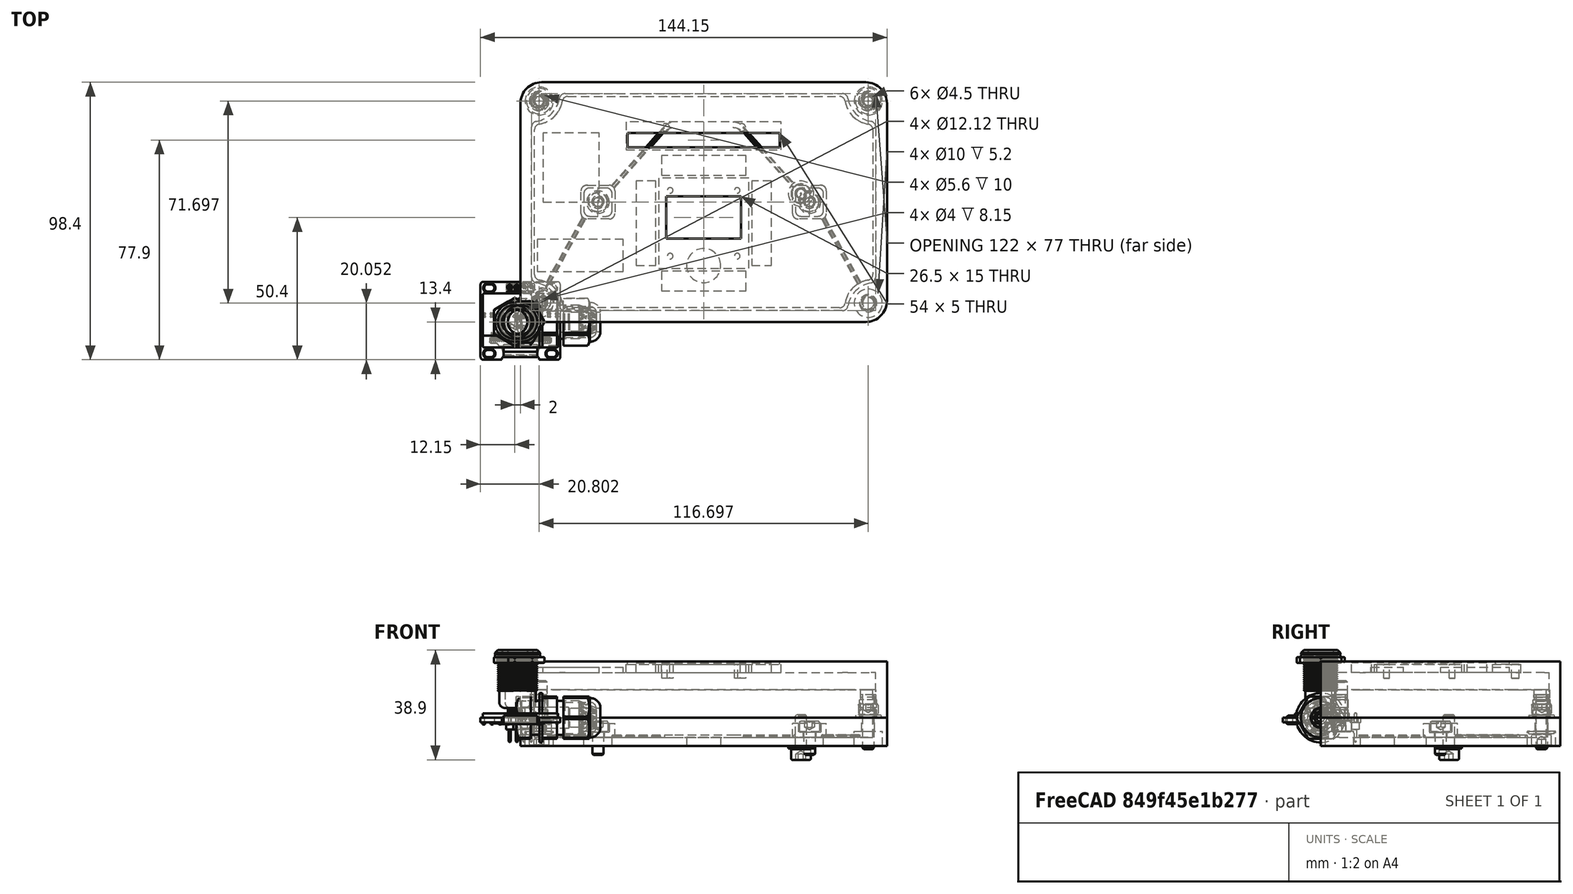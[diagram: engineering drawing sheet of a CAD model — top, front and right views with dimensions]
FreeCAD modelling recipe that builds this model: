
FCSTD DOCUMENT  (FreeCAD 0.20R27319 (Git))
Label: FirstDraft_backup
License: All rights reserved
LicenseURL: http://en.wikipedia.org/wiki/All_rights_reserved
objects: Part::Feature×54, Sketcher::SketchObject×53, PartDesign::Pocket×22, PartDesign::Pad×15, Part::FeaturePython×15, App::Part×11, PartDesign::Line×10, PartDesign::Hole×9, PartDesign::CoordinateSystem×4, App::DocumentObjectGroup×4, PartDesign::AdditiveBox×3, PartDesign::Fillet×3, PartDesign::ShapeBinder×3, App::Link×2, PartDesign::Body×2, PartDesign::AdditivePipe×2, Mesh::Feature×1, App::FeaturePython×1, PartDesign::Plane×1, PartDesign::Mirrored×1
note: 251 computed .brp shape members not serialized (recipe doc carries the construction recipe); baked Part::Feature solids carry a one-line shape summary decoded from their .brp

FEATURE [PartDesign::AdditiveBox] Box002
  AttacherType = Attacher::AttachEngine3D
  Height = 20
  Length = 130
  Width = 85
FEATURE [Sketcher::SketchObject] Sketch001
  ExternalGeometry = -> [Box002]
  FullyConstrained = true
  MapMode = 5
  Placement = pos=(0,0,0) rot=(1,0,0;3.14159rad)
  Support = -> [Box002]
  sketch-geometry (23):
    g0: LineSegment StartX=15.8322 StartY=-4 StartZ=0 EndX=114.168 EndY=-4 EndZ=0
    g1: LineSegment StartX=126 StartY=-15.8322 StartZ=0 EndX=126 EndY=-69.1678 EndZ=0
    g2: LineSegment StartX=114.168 StartY=-81 StartZ=0 EndX=15.8322 EndY=-81 EndZ=0
    g3: LineSegment StartX=4 StartY=-69.1678 StartZ=0 EndX=4 EndY=-15.8322 EndZ=0
    g4: GeomPoint X=4 Y=-4 Z=0
    g5: GeomPoint X=126 Y=-81 Z=0
    g6: GeomPoint X=65 Y=-42.5 Z=0
    g7: ArcOfCircle CenterX=4 CenterY=-81 CenterZ=0 NormalX=0 NormalY=0 NormalZ=1 AngleXU=0 Radius=10 StartAngle=0.167448 EndAngle=1.40335
    g8: ArcOfCircle CenterX=6 CenterY=-69.1678 CenterZ=0 NormalX=0 NormalY=0 NormalZ=1 AngleXU=0 Radius=2 StartAngle=3.14159 EndAngle=4.54494
    g9: ArcOfCircle CenterX=15.8322 CenterY=-79 CenterZ=0 NormalX=0 NormalY=0 NormalZ=1 AngleXU=0 Radius=2 StartAngle=3.30904 EndAngle=4.71239
    g10: ArcOfCircle CenterX=4 CenterY=-4 CenterZ=0 NormalX=0 NormalY=0 NormalZ=1 AngleXU=0 Radius=10 StartAngle=4.87984 EndAngle=6.11574
    g11: ArcOfCircle CenterX=126 CenterY=-4 CenterZ=0 NormalX=0 NormalY=0 NormalZ=1 AngleXU=0 Radius=10 StartAngle=3.30904 EndAngle=4.54494
    g12: ArcOfCircle CenterX=126 CenterY=-81 CenterZ=0 NormalX=0 NormalY=0 NormalZ=1 AngleXU=0 Radius=10 StartAngle=1.73824 EndAngle=2.97414
    g13: LineSegment StartX=4 StartY=-81 StartZ=0 EndX=126 EndY=-81 EndZ=0
    g14: LineSegment StartX=126 StartY=-81 StartZ=0 EndX=126 EndY=-4 EndZ=0
    g15: LineSegment StartX=126 StartY=-4 StartZ=0 EndX=4 EndY=-4 EndZ=0
    g16: LineSegment StartX=4 StartY=-4 StartZ=0 EndX=4 EndY=-81 EndZ=0
    g17: ArcOfCircle CenterX=6 CenterY=-15.8322 CenterZ=0 NormalX=0 NormalY=0 NormalZ=1 AngleXU=0 Radius=2 StartAngle=1.73824 EndAngle=3.14159
    g18: ArcOfCircle CenterX=124 CenterY=-15.8322 CenterZ=0 NormalX=0 NormalY=0 NormalZ=1 AngleXU=0 Radius=2 StartAngle=0 EndAngle=1.40335
    g19: ArcOfCircle CenterX=15.8322 CenterY=-6 CenterZ=0 NormalX=0 NormalY=0 NormalZ=1 AngleXU=0 Radius=2 StartAngle=1.5708 EndAngle=2.97414
    g20: ArcOfCircle CenterX=114.168 CenterY=-6 CenterZ=0 NormalX=0 NormalY=0 NormalZ=1 AngleXU=0 Radius=2 StartAngle=0.167448 EndAngle=1.5708
    g21: ArcOfCircle CenterX=124 CenterY=-69.1678 CenterZ=0 NormalX=0 NormalY=0 NormalZ=1 AngleXU=0 Radius=2 StartAngle=4.87984 EndAngle=6.28319
    g22: ArcOfCircle CenterX=114.168 CenterY=-79 CenterZ=0 NormalX=0 NormalY=0 NormalZ=1 AngleXU=0 Radius=2 StartAngle=4.71239 EndAngle=6.11574
  constraints (56):
    c: Horizontal(g0)
    c: Horizontal(g2)
    c: Vertical(g1)
    c: Vertical(g3)
    c: PointOnObject(g4,g0)
    c: PointOnObject(g4,g3)
    c: PointOnObject(g5,g1)
    c: PointOnObject(g5,g2)
    c: Symmetric(g-6,g-4,g6)
    c: Tangent(g7,g8) = 1.5708
    c: Tangent(g3,g8) = 1.5708
    c: Tangent(g2,g9) = 1.5708
    c: Tangent(g7,g9) = 1.5708
    c: Coincident(g12,g5)
    c: Coincident(g13,g14)
    c: Coincident(g14,g15)
    c: Coincident(g15,g16)
    c: Coincident(g16,g13)
    c: Horizontal(g13)
    c: Horizontal(g15)
    c: Vertical(g14)
    c: Vertical(g16)
    c: Coincident(g13,g7)
    c: Coincident(g14,g11)
    c: Coincident(g4,g10)
    c: Symmetric(g7,g11,g6)
    c: Tangent(g3,g17) = 1.5708
    c: Tangent(g10,g17) = 1.5708
    c: Tangent(g1,g18) = 1.5708
    c: Tangent(g11,g18) = 1.5708
    c: Tangent(g10,g19) = 1.5708
    c: Tangent(g0,g19) = 1.5708
    c: Tangent(g11,g20) = 1.5708
    c: Tangent(g0,g20) = 1.5708
    c: Tangent(g1,g21) = 1.5708
    c: Tangent(g12,g21) = 1.5708
    c: Tangent(g2,g22) = 1.5708
    c: Tangent(g12,g22) = 1.5708
    c: PointOnObject(g0,g15)
    c: PointOnObject(g3,g16)
    c: PointOnObject(g1,g14)
    c: DistanceX(g-6,g7) = 4
    c: DistanceY(g-6,g7) = 4
    c: PointOnObject(g2,g13)
    c: Equal(g7,g10)
    c: Equal(g10,g11)
    c: Equal(g11,g12)
    c: Radius(g7) = 10
    c: Equal(g9,g8)
    c: Equal(g8,g19)
    c: Equal(g19,g17)
    c: Equal(g17,g20)
    c: Equal(g20,g18)
    c: Equal(g18,g21)
    c: Equal(g21,g22)
    c: Radius(g9) = 2
FEATURE [PartDesign::Pocket] Pocket001
  BaseFeature = -> Box002
  Direction = (0,0,1)
  Length = 16
  Length2 = 100
  Profile = -> Sketch001
  ReferenceAxis = -> Sketch001 [N_Axis]
  Type = 0
  expr: Length = <<Box002>>.Height - 4mm
FEATURE [Sketcher::SketchObject] Sketch002
  ExternalGeometry = -> [Pocket001]
  FullyConstrained = true
  MapMode = 5
  Placement = pos=(0,0,16) rot=(1,0,0;3.14159rad)
  Support = -> [Pocket001]
  sketch-geometry (11):
    g0: LineSegment StartX=49 StartY=-19 StartZ=0 EndX=81 EndY=-19 EndZ=0
    g1: LineSegment StartX=81 StartY=-19 StartZ=0 EndX=81 EndY=-51 EndZ=0
    g2: LineSegment StartX=81 StartY=-51 StartZ=0 EndX=49 EndY=-51 EndZ=0
    g3: LineSegment StartX=49 StartY=-51 StartZ=0 EndX=49 EndY=-19 EndZ=0
    g4: GeomPoint X=65 Y=-4 Z=0
    g5: LineSegment StartX=65 StartY=-4 StartZ=0 EndX=65 EndY=-19 EndZ=0
    g6: LineSegment StartX=37.5 StartY=-61 StartZ=0 EndX=92.5 EndY=-61 EndZ=0
    g7: LineSegment StartX=92.5 StartY=-61 StartZ=0 EndX=92.5 EndY=-71 EndZ=0
    g8: LineSegment StartX=92.5 StartY=-71 StartZ=0 EndX=37.5 EndY=-71 EndZ=0
    g9: LineSegment StartX=37.5 StartY=-71 StartZ=0 EndX=37.5 EndY=-61 EndZ=0
    g10: LineSegment StartX=65 StartY=-19 StartZ=0 EndX=65 EndY=-61 EndZ=0
  constraints (29):
    c: Coincident(g0,g1)
    c: Coincident(g1,g2)
    c: Coincident(g2,g3)
    c: Coincident(g3,g0)
    c: Horizontal(g0)
    c: Horizontal(g2)
    c: Vertical(g1)
    c: Vertical(g3)
    c: Coincident(g5,g4)
    c: Vertical(g5)
    c: Symmetric(g0,g0,g5)
    c: DistanceY(g5,g5) = 15
    c: DistanceY(g1,g1) = 32
    c: Equal(g1,g0)
    c: Coincident(g6,g7)
    c: Coincident(g7,g8)
    c: Coincident(g8,g9)
    c: Coincident(g9,g6)
    c: Horizontal(g6)
    c: Horizontal(g8)
    c: Vertical(g7)
    c: Vertical(g9)
    c: DistanceX(g6,g6) = 55
    c: DistanceY(g7,g7) = 10
    c: Coincident(g10,g5)
    c: Vertical(g10)
    c: Symmetric(g6,g6,g10)
    c: DistanceY(g6,g1) = 10
    c: Symmetric(g-3,g-3,g4)
FEATURE [PartDesign::Pocket] Pocket002  label="Platz OLED und LED-Strip"
  BaseFeature = -> Pocket001
  Direction = (0,0,1)
  Length = 3
  Length2 = 100
  Profile = -> Sketch002
  Type = 0
FEATURE [Sketcher::SketchObject] Sketch003
  ExternalGeometry = -> [Sketch002,Pocket002]
  FullyConstrained = true
  MapMode = 5
  Placement = pos=(0,0,16) rot=(1,0,0;3.14159rad)
  Support = -> [Pocket002]
  sketch-geometry (10):
    g0: LineSegment StartX=51.75 StartY=-29.5 StartZ=0 EndX=78.25 EndY=-29.5 EndZ=0
    g1: LineSegment StartX=78.25 StartY=-29.5 StartZ=0 EndX=78.25 EndY=-44.5 EndZ=0
    g2: LineSegment StartX=78.25 StartY=-44.5 StartZ=0 EndX=51.75 EndY=-44.5 EndZ=0
    g3: LineSegment StartX=51.75 StartY=-44.5 StartZ=0 EndX=51.75 EndY=-29.5 EndZ=0
    g4: LineSegment StartX=38 StartY=-62 StartZ=0 EndX=92 EndY=-62 EndZ=0
    g5: LineSegment StartX=92 StartY=-62 StartZ=0 EndX=92 EndY=-67 EndZ=0
    g6: LineSegment StartX=92 StartY=-67 StartZ=0 EndX=38 EndY=-67 EndZ=0
    g7: LineSegment StartX=38 StartY=-67 StartZ=0 EndX=38 EndY=-62 EndZ=0
    g8: LineSegment StartX=65 StartY=-62 StartZ=0 EndX=65 EndY=-61 EndZ=0
    g9: LineSegment StartX=65 StartY=-29.5 StartZ=0 EndX=65 EndY=-19 EndZ=0
  constraints (28):
    c: Coincident(g0,g1)
    c: Coincident(g1,g2)
    c: Coincident(g2,g3)
    c: Coincident(g3,g0)
    c: Horizontal(g0)
    c: Horizontal(g2)
    c: Vertical(g1)
    c: Vertical(g3)
    c: DistanceX(g0,g0) = 26.5
    c: DistanceY(g1,g1) = 15
    c: Coincident(g4,g5)
    c: Coincident(g5,g6)
    c: Coincident(g6,g7)
    c: Coincident(g7,g4)
    c: Horizontal(g4)
    c: Horizontal(g6)
    c: Vertical(g5)
    c: Vertical(g7)
    c: DistanceX(g4,g-3) = 0.5
    c: Vertical(g8)
    c: Symmetric(g4,g4,g8)
    c: Symmetric(g-3,g-4,g8)
    c: DistanceY(g5,g5) = 5
    c: DistanceY(g4,g-3) = 1
    c: Vertical(g9)
    c: Symmetric(g0,g0,g9)
    c: DistanceY(g9,g9) = 10.5
    c: Symmetric(g-5,g-5,g9)
FEATURE [PartDesign::Pocket] Pocket003  label="Sichtausschnitt"
  BaseFeature = -> Pocket002
  Direction = (0,0,1)
  Length = 1.01
  Length2 = 100
  Profile = -> Sketch003
  ReferenceAxis = -> Sketch003 [N_Axis]
  Type = 1
FEATURE [Sketcher::SketchObject] Sketch004  label="Sketch Halter OLED"
  ExternalGeometry = -> [Sketch002]
  FullyConstrained = true
  MapMode = 5
  Placement = pos=(0,0,19) rot=(1,0,0;3.14159rad)
  Support = -> [Pocket003]
  sketch-geometry (9):
    g0: Circle CenterX=53.1 CenterY=-23.35 CenterZ=0 NormalX=0 NormalY=0 NormalZ=1 AngleXU=0 Radius=1
    g1: Circle CenterX=76.9 CenterY=-23.35 CenterZ=0 NormalX=0 NormalY=0 NormalZ=1 AngleXU=0 Radius=1
    g2: Circle CenterX=76.9 CenterY=-46.65 CenterZ=0 NormalX=0 NormalY=0 NormalZ=1 AngleXU=0 Radius=1
    g3: Circle CenterX=53.1 CenterY=-46.65 CenterZ=0 NormalX=0 NormalY=0 NormalZ=1 AngleXU=0 Radius=1
    g4: LineSegment StartX=53.1 StartY=-23.35 StartZ=0 EndX=76.9 EndY=-23.35 EndZ=0
    g5: LineSegment StartX=76.9 StartY=-23.35 StartZ=0 EndX=76.9 EndY=-46.65 EndZ=0
    g6: LineSegment StartX=76.9 StartY=-46.65 StartZ=0 EndX=53.1 EndY=-46.65 EndZ=0
    g7: LineSegment StartX=53.1 StartY=-46.65 StartZ=0 EndX=53.1 EndY=-23.35 EndZ=0
    g8: GeomPoint X=65 Y=-35 Z=0
  constraints (20):
    c: Coincident(g4,g5)
    c: Coincident(g5,g6)
    c: Coincident(g6,g7)
    c: Coincident(g7,g4)
    c: Horizontal(g4)
    c: Horizontal(g6)
    c: Vertical(g5)
    c: Vertical(g7)
    c: Coincident(g4,g0)
    c: Coincident(g5,g2)
    c: Coincident(g1,g4)
    c: Coincident(g3,g6)
    c: Equal(g0,g1)
    c: Equal(g1,g2)
    c: Equal(g2,g3)
    c: Diameter(g1) = 2
    c: DistanceX(g4,g4) = 23.8
    c: DistanceY(g5,g5) = 23.3
    c: Symmetric(g-4,g-6,g8)
    c: Symmetric(g3,g1,g8)
FEATURE [PartDesign::Pad] Pad  label="Halter OLED"
  BaseFeature = -> Pocket003
  Direction = (0,0,-1)
  Length = 5
  Length2 = 100
  Profile = -> Sketch004
  ReferenceAxis = -> Sketch004 [N_Axis]
  Type = 0
FEATURE [Sketcher::SketchObject] Sketch005
  ExternalGeometry = -> [Sketch002]
  FullyConstrained = true
  MapMode = 5
  Placement = pos=(0,0,16) rot=(1,0,0;3.14159rad)
  Support = -> [Pad]
  sketch-geometry (26):
    g0: LineSegment StartX=50 StartY=-11 StartZ=0 EndX=80 EndY=-11 EndZ=0
    g1: LineSegment StartX=80 StartY=-11 StartZ=0 EndX=80 EndY=-18 EndZ=0
    g2: LineSegment StartX=80 StartY=-18 StartZ=0 EndX=50 EndY=-18 EndZ=0
    g3: LineSegment StartX=50 StartY=-18 StartZ=0 EndX=50 EndY=-11 EndZ=0
    g4: LineSegment StartX=82 StartY=-20 StartZ=0 EndX=89 EndY=-20 EndZ=0
    g5: LineSegment StartX=89 StartY=-20 StartZ=0 EndX=89 EndY=-50 EndZ=0
    g6: LineSegment StartX=89 StartY=-50 StartZ=0 EndX=82 EndY=-50 EndZ=0
    g7: LineSegment StartX=82 StartY=-50 StartZ=0 EndX=82 EndY=-20 EndZ=0
    g8: LineSegment StartX=41 StartY=-20 StartZ=0 EndX=48 EndY=-20 EndZ=0
    g9: LineSegment StartX=48 StartY=-20 StartZ=0 EndX=48 EndY=-50 EndZ=0
    g10: LineSegment StartX=48 StartY=-50 StartZ=0 EndX=41 EndY=-50 EndZ=0
    g11: LineSegment StartX=41 StartY=-50 StartZ=0 EndX=41 EndY=-20 EndZ=0
    g12: LineSegment StartX=50 StartY=-52 StartZ=0 EndX=80 EndY=-52 EndZ=0
    g13: LineSegment StartX=80 StartY=-52 StartZ=0 EndX=80 EndY=-59 EndZ=0
    g14: LineSegment StartX=80 StartY=-59 StartZ=0 EndX=50 EndY=-59 EndZ=0
    g15: LineSegment StartX=50 StartY=-59 StartZ=0 EndX=50 EndY=-52 EndZ=0
    g16: LineSegment StartX=48 StartY=-18 StartZ=0 EndX=82 EndY=-18 EndZ=0
    g17: LineSegment StartX=82 StartY=-18 StartZ=0 EndX=82 EndY=-52 EndZ=0
    g18: LineSegment StartX=82 StartY=-52 StartZ=0 EndX=48 EndY=-52 EndZ=0
    g19: LineSegment StartX=48 StartY=-52 StartZ=0 EndX=48 EndY=-18 EndZ=0
    g20: GeomPoint X=65 Y=-35 Z=0
    g21: GeomPoint X=48 Y=-35 Z=0
    g22: GeomPoint X=116 Y=-18 Z=0
    g23: GeomPoint X=82 Y=-35 Z=0
    g24: GeomPoint X=65 Y=-52 Z=0
    g25: GeomPoint X=65 Y=-18 Z=0
  constraints (61):
    c: Coincident(g0,g1)
    c: Coincident(g1,g2)
    c: Coincident(g2,g3)
    c: Coincident(g3,g0)
    c: Horizontal(g0)
    c: Horizontal(g2)
    c: Vertical(g1)
    c: Vertical(g3)
    c: Coincident(g4,g5)
    c: Coincident(g5,g6)
    c: Coincident(g6,g7)
    c: Coincident(g7,g4)
    c: Horizontal(g4)
    c: Horizontal(g6)
    c: Vertical(g5)
    c: Vertical(g7)
    c: Coincident(g8,g9)
    c: Coincident(g9,g10)
    c: Coincident(g10,g11)
    c: Coincident(g11,g8)
    c: Horizontal(g8)
    c: Horizontal(g10)
    c: Vertical(g9)
    c: Vertical(g11)
    c: Coincident(g12,g13)
    c: Coincident(g13,g14)
    c: Coincident(g14,g15)
    c: Coincident(g15,g12)
    c: Horizontal(g12)
    c: Horizontal(g14)
    c: Vertical(g13)
    c: Vertical(g15)
    c: Equal(g4,g1)
    c: Equal(g1,g8)
    c: Equal(g8,g13)
    c: Coincident(g16,g17)
    c: Coincident(g17,g18)
    c: Coincident(g18,g19)
    c: Coincident(g19,g16)
    c: DistanceX(g-4,g16) = 1
    c: DistanceY(g-4,g16) = 1
    c: Symmetric(g16,g18,g20)
    c: Symmetric(g-6,g-4,g20)
    c: DistanceY(g15,g15) = 7
    c: Vertical(g19)
    c: Horizontal(g16)
    c: PointOnObject(g12,g18)
    c: Vertical(g17)
    c: Equal(g0,g11)
    c: Equal(g11,g5)
    c: Equal(g5,g14)
    c: DistanceY(g11,g11) = 30
    c: Symmetric(g18,g17,g24)
    c: Symmetric(g6,g4,g23)
    c: Symmetric(g16,g22,g16)
    c: Symmetric(g16,g18,g21)
    c: Symmetric(g8,g9,g21)
    c: Symmetric(g17,g16,g23)
    c: Symmetric(g12,g12,g24)
    c: Symmetric(g2,g1,g25)
    c: Symmetric(g16,g16,g25)
FEATURE [PartDesign::Pocket] Pocket004  label="Ausschnitte  Touch"
  BaseFeature = -> Pad
  Direction = (0,0,1)
  Length = 3.5
  Length2 = 100
  Profile = -> Sketch005
  Type = 0
FEATURE [Part::Feature] Part__Feature  label="Pantalla"
  Placement = pos=(4e-15,0.525,-1e-15) rot=(0,0,1;0rad)
  shape: bbox 26.68 x 19.2 x 1.6 mm, 12 faces (baked)
FEATURE [Part::Feature] Part__Feature001  label="PADS"
  shape: bbox 0.4 x 3 x 0.1 mm, 6 faces (baked)
FEATURE [Part::Feature] Part__Feature002  label="PADS001"
  shape: bbox 0.4 x 3 x 0.1 mm, 6 faces (baked)
FEATURE [Part::Feature] Part__Feature003  label="PADS002"
  shape: bbox 0.4 x 3 x 0.1 mm, 6 faces (baked)
FEATURE [Part::Feature] Part__Feature004  label="PADS003"
  shape: bbox 0.4 x 3 x 0.1 mm, 6 faces (baked)
FEATURE [Part::Feature] Part__Feature005  label="PADS004"
  shape: bbox 0.4 x 3 x 0.1 mm, 6 faces (baked)
FEATURE [Part::Feature] Part__Feature006  label="PADS005"
  shape: bbox 0.4 x 3 x 0.1 mm, 6 faces (baked)
FEATURE [Part::Feature] Part__Feature007  label="PADS006"
  shape: bbox 0.4 x 3 x 0.1 mm, 6 faces (baked)
FEATURE [Part::Feature] Part__Feature008  label="PADS007"
  shape: bbox 0.4 x 3 x 0.1 mm, 6 faces (baked)
FEATURE [Part::Feature] Part__Feature009  label="PADS008"
  shape: bbox 0.4 x 3 x 0.1 mm, 6 faces (baked)
FEATURE [Part::Feature] Part__Feature010  label="PADS009"
  shape: bbox 0.4 x 3 x 0.1 mm, 6 faces (baked)
FEATURE [Part::Feature] Part__Feature011  label="PADS010"
  shape: bbox 0.4 x 3 x 0.1 mm, 6 faces (baked)
FEATURE [Part::Feature] Part__Feature012  label="PADS011"
  shape: bbox 0.4 x 3 x 0.1 mm, 6 faces (baked)
FEATURE [Part::Feature] Part__Feature013  label="PADS012"
  shape: bbox 0.4 x 3 x 0.1 mm, 6 faces (baked)
FEATURE [Part::Feature] Part__Feature014  label="PADS013"
  shape: bbox 0.4 x 3 x 0.1 mm, 6 faces (baked)
FEATURE [Part::Feature] Part__Feature015  label="PADS014"
  shape: bbox 0.4 x 3 x 0.1 mm, 6 faces (baked)
FEATURE [Part::Feature] Part__Feature016  label="PADS015"
  shape: bbox 0.4 x 3 x 0.1 mm, 6 faces (baked)
FEATURE [Part::Feature] Part__Feature017  label="PADS016"
  shape: bbox 0.4 x 3 x 0.1 mm, 6 faces (baked)
FEATURE [Part::Feature] Part__Feature018  label="PADS017"
  shape: bbox 0.4 x 3 x 0.1 mm, 6 faces (baked)
FEATURE [Part::Feature] Part__Feature019  label="PADS018"
  shape: bbox 0.4 x 3 x 0.1 mm, 6 faces (baked)
FEATURE [Part::Feature] Part__Feature020  label="PADS019"
  shape: bbox 0.4 x 3 x 0.1 mm, 6 faces (baked)
FEATURE [Part::Feature] Part__Feature021  label="PADS020"
  shape: bbox 0.4 x 3 x 0.1 mm, 6 faces (baked)
FEATURE [Part::Feature] Part__Feature022  label="PADS021"
  shape: bbox 0.4 x 3 x 0.1 mm, 6 faces (baked)
FEATURE [Part::Feature] Part__Feature023  label="PADS022"
  shape: bbox 0.4 x 3 x 0.1 mm, 6 faces (baked)
FEATURE [Part::Feature] Part__Feature024  label="PADS023"
  shape: bbox 0.4 x 3 x 0.1 mm, 6 faces (baked)
FEATURE [Part::Feature] Part__Feature025  label="PADS024"
  shape: bbox 0.4 x 3 x 0.1 mm, 6 faces (baked)
FEATURE [Part::Feature] Part__Feature026  label="PADS025"
  shape: bbox 0.4 x 3 x 0.1 mm, 6 faces (baked)
FEATURE [Part::Feature] Part__Feature027  label="PADS026"
  shape: bbox 0.4 x 3 x 0.1 mm, 6 faces (baked)
FEATURE [Part::Feature] Part__Feature028  label="PADS027"
  shape: bbox 0.4 x 3 x 0.1 mm, 6 faces (baked)
FEATURE [Part::Feature] Part__Feature029  label="PADS028"
  shape: bbox 0.4 x 3 x 0.1 mm, 6 faces (baked)
FEATURE [Part::Feature] Part__Feature030  label="PADS029"
  shape: bbox 0.4 x 3 x 0.1 mm, 6 faces (baked)
FEATURE [App::Part] PADS  label="PADS030"
  Group = -> [Part__Feature001,Part__Feature002,Part__Feature003,Part__Feature004,Part__Feature005,Part__Feature006,Part__Feature007,Part__Feature008,Part__Feature009,Part__Feature010,Part__Feature011,Part__Feature012,Part__Feature013,Part__Feature014,Part__Feature015,Part__Feature016,Part__Feature017,Part__Feature018,Part__Feature019,Part__Feature020,Part__Feature021,Part__Feature022,Part__Feature023,+7 more]
  Origin = -> Origin005
FEATURE [Part::Feature] Part__Feature031  label="Base PCB"
  shape: bbox 28.3 x 27.65 x 1.7 mm, 324 faces (baked)
FEATURE [App::Part] Base_PCB  label="Base PCB001"
  Group = -> [PADS,Part__Feature031]
  Origin = -> Origin006
FEATURE [Part::Feature] Part__Feature032  label="PINOS"
  shape: bbox 2.54 x 2.54 x 10.4 mm, 28 faces (baked)
FEATURE [Part::Feature] Part__Feature033  label="PINOS001"
  shape: bbox 2.54 x 2.54 x 10.4 mm, 28 faces (baked)
FEATURE [Part::Feature] Part__Feature034  label="PINOS002"
  shape: bbox 2.54 x 2.54 x 10.4 mm, 28 faces (baked)
FEATURE [Part::Feature] Part__Feature035  label="PINOS003"
  shape: bbox 2.54 x 2.54 x 10.4 mm, 28 faces (baked)
FEATURE [App::Part] PINOS  label="PINOS004"
  Group = -> [Part__Feature032,Part__Feature033,Part__Feature034,Part__Feature035]
  Origin = -> Origin007
FEATURE [Part::Feature] Part__Feature036  label="fLEX"
  Placement = pos=(4e-15,1.525,-0.1) rot=(0,0,1;0rad)
  shape: bbox 39.56 x 36.02 x 13.34 mm, 31 faces (baked)
FEATURE [Part::Feature] Part__Feature037  label="res"
  Placement = pos=(13,2.425,-4) rot=(1,0,0;3.14159rad)
  shape: bbox 1.02 x 1.65 x 0.81 mm, 37 faces (baked)
FEATURE [Part::Feature] Part__Feature038  label="res001"
  Placement = pos=(10.1111,2.425,-4) rot=(1,0,0;3.14159rad)
  shape: bbox 1.02 x 1.65 x 0.81 mm, 37 faces (baked)
FEATURE [Part::Feature] Part__Feature039  label="res002"
  Placement = pos=(7.22222,2.425,-4) rot=(1,0,0;3.14159rad)
  shape: bbox 1.02 x 1.65 x 0.81 mm, 37 faces (baked)
FEATURE [Part::Feature] Part__Feature040  label="res003"
  Placement = pos=(4.33333,2.425,-4) rot=(1,0,0;3.14159rad)
  shape: bbox 1.02 x 1.65 x 0.81 mm, 37 faces (baked)
FEATURE [Part::Feature] Part__Feature041  label="res004"
  Placement = pos=(1.44444,2.425,-4) rot=(1,0,0;3.14159rad)
  shape: bbox 1.02 x 1.65 x 0.81 mm, 37 faces (baked)
FEATURE [Part::Feature] Part__Feature042  label="res005"
  Placement = pos=(-1.44444,2.425,-4) rot=(1,0,0;3.14159rad)
  shape: bbox 1.02 x 1.65 x 0.81 mm, 37 faces (baked)
FEATURE [Part::Feature] Part__Feature043  label="res006"
  Placement = pos=(-4.33333,2.425,-4) rot=(1,0,0;3.14159rad)
  shape: bbox 1.02 x 1.65 x 0.81 mm, 37 faces (baked)
FEATURE [Part::Feature] Part__Feature044  label="res007"
  Placement = pos=(-7.22222,2.425,-4) rot=(1,0,0;3.14159rad)
  shape: bbox 1.02 x 1.65 x 0.81 mm, 37 faces (baked)
FEATURE [Part::Feature] Part__Feature045  label="res008"
  Placement = pos=(-10.1111,2.425,-4) rot=(1,0,0;3.14159rad)
  shape: bbox 1.02 x 1.65 x 0.81 mm, 37 faces (baked)
FEATURE [Part::Feature] Part__Feature046  label="res009"
  Placement = pos=(-13,2.425,-4) rot=(1,0,0;3.14159rad)
  shape: bbox 1.02 x 1.65 x 0.81 mm, 37 faces (baked)
FEATURE [Part::Feature] Part__Feature047  label="res010"
  Placement = pos=(0,-1.575,-4) rot=(0.707107,-0.707107,0;3.14159rad)
  shape: bbox 1.65 x 1.02 x 0.81 mm, 37 faces (baked)
FEATURE [App::Part] Resistores_SMD  label="Resistores SMD"
  Group = -> [Part__Feature037,Part__Feature038,Part__Feature039,Part__Feature040,Part__Feature041,Part__Feature042,Part__Feature043,Part__Feature044,Part__Feature045,Part__Feature046,Part__Feature047]
  Origin = -> Origin008
FEATURE [App::Part] Tela_OLed_128x64_v15  label="Tela OLed 128x64 v15"
  Group = -> [Part__Feature,Base_PCB,PINOS,Part__Feature036,Resistores_SMD]
  Origin = -> Origin009
  Placement = pos=(60,29.5,22.5) rot=(0,0,1;0rad)
FEATURE [Sketcher::SketchObject] Sketch007
  ExternalGeometry = -> [Pocket004,Sketch003]
  FullyConstrained = true
  MapMode = 5
  Placement = pos=(0,0,19) rot=(1,0,0;3.14159rad)
  Support = -> [Pocket004]
  sketch-geometry (5):
    g0: Circle CenterX=51.5 CenterY=-69 CenterZ=0 NormalX=0 NormalY=0 NormalZ=1 AngleXU=0 Radius=1.35
    g1: Circle CenterX=78.5 CenterY=-69 CenterZ=0 NormalX=0 NormalY=0 NormalZ=1 AngleXU=0 Radius=1.35
    g2: LineSegment StartX=51.5 StartY=-69 StartZ=0 EndX=78.5 EndY=-69 EndZ=0
    g3: LineSegment StartX=65 StartY=-71 StartZ=0 EndX=65 EndY=-67 EndZ=0
    g4: GeomPoint X=65 Y=-69 Z=0
  constraints (11):
    c: Coincident(g2,g0)
    c: Coincident(g2,g1)
    c: Horizontal(g2)
    c: Equal(g1,g0)
    c: Diameter(g0) = 2.7
    c: DistanceX(g2,g2) = 27
    c: Vertical(g3)
    c: Symmetric(g0,g1,g4)
    c: Symmetric(g3,g3,g4)
    c: Symmetric(g-5,g-5,g3)
    c: PointOnObject(g3,g-6)
FEATURE [PartDesign::Pad] Pad001  label="Halter LED Strip"
  BaseFeature = -> Pocket004
  Direction = (0,0,-1)
  Length = 5
  Length2 = 10
  Profile = -> Sketch007
  ReferenceAxis = -> Sketch007 [N_Axis]
  Type = 0
FEATURE [Mesh::Feature] DuinoPeak_WS2812_RGB_Pixel
FEATURE [Part::Feature] Part__Feature086  label="12mm Switch"
  shape: bbox 17.01 x 15.16 x 24 mm, 165 faces, 3 solids (baked)
FEATURE [App::Part] _2mm_Switch_v5  label="12mm Switch v5"
  Group = -> [Part__Feature086]
  Origin = -> Origin012
  Placement = pos=(15,0,0) rot=(1,0,0;0rad)
FEATURE [Part::FeaturePython] Clone  label="12mm Switch v006"  # Draft clone (typed FeaturePython)
  AttacherType = Attacher::AttachEngine3D
  Fuse = false
  Objects = -> [_2mm_Switch_v5]
  Placement = pos=(-2,-1e-15,0) rot=(0,0,-1;0.523599rad)
  Scale = (1,1,1)
FEATURE [PartDesign::CoordinateSystem] LCS_Origin
  AttacherType = Attacher::AttachEngine3D
  MapMode = 2
  Support = -> [X_Axis013]
FEATURE [App::FeaturePython] Variables  # WARN: FeaturePython — macro-defined, semantics opaque (R4)
  Type = App::PropertyContainer
FEATURE [App::DocumentObjectGroup] Constraints
FEATURE [App::DocumentObjectGroup] Configurations
FEATURE [App::Part] Part  label="Double-Switch"
  Group = -> [Clone,_2mm_Switch_v5]
  Origin = -> Origin014
FEATURE [App::Part] Part001  label="LED-Strip"
  Group = -> [DuinoPeak_WS2812_RGB_Pixel]
  Origin = -> Origin015
  Placement = pos=(34,56,20.6) rot=(0,0,1;0rad)
FEATURE [App::Link] Base  label="Base001"
  AssemblyType = Part::Link
  AttachedBy = #LCS_1
  AttachedTo = Parent Assembly#LCS_Origin
  LinkedObject = -> Body
  SolverId = Asm4EE
  expr: Placement = LCS_Origin.Placement * AttachmentOffset * LCS_1.Placement ^ -1
FEATURE [Part::FeaturePython] HeatSet  label="Auto-HeatSet"  # WARN: FeaturePython — macro-defined, semantics opaque (R4)
  Placement = pos=(123.349,78.3485,0) rot=(-1,0,0;3.14159rad)
  baseObject = -> Body002 [Edge48]
  diameter = 0
  invert = false
  offset = 0
FEATURE [Part::FeaturePython] HeatSet001  label="Auto-HeatSet001"  # WARN: FeaturePython — macro-defined, semantics opaque (R4)
  Placement = pos=(6.65146,78.3485,0) rot=(-1,0,0;3.14159rad)
  baseObject = -> Body002 [Edge31]
  diameter = 0
  invert = false
  offset = 0
FEATURE [Part::FeaturePython] HeatSet002  label="Auto-HeatSet002"  # WARN: FeaturePython — macro-defined, semantics opaque (R4)
  Placement = pos=(6.65146,6.65148,0) rot=(-1,0,0;3.14159rad)
  baseObject = -> Body002 [Edge29]
  diameter = 0
  invert = false
  offset = 0
FEATURE [Part::FeaturePython] HeatSet003  label="Auto-HeatSet003"  # WARN: FeaturePython — macro-defined, semantics opaque (R4)
  Placement = pos=(123.349,6.65148,0) rot=(-1,0,0;3.14159rad)
  baseObject = -> Body002 [Edge30]
  diameter = 0
  invert = false
  offset = 0
FEATURE [App::Link] Front_inkl__Fasteners  label="Front inkl. Fasteners001"
  AssemblyType = Part::Link
  AttachedBy = #LCS_3
  AttachedTo = Base#LCS_1
  LinkedObject = -> Part002
  SolverId = Asm4EE
  expr: Placement = Base.Placement * LCS_1.Placement * AttachmentOffset * LCS_3.Placement ^ -1
FEATURE [Part::FeaturePython] Washer  label="M4-Washer"  # Fasteners workbench fastener (typed FeaturePython)
  Placement = pos=(99.5,45.5,-10) rot=(-1,0,0;3.14159rad)
  baseObject = -> Body [Edge50]
  diameter = 5
  invert = false
  matchOuter = true
  offset = 0
  type = 3
FEATURE [Part::FeaturePython] Washer001  label="M4-Washer424"  # Fasteners workbench fastener (typed FeaturePython)
  Placement = pos=(123.349,78.3485,0) rot=(0,0,1;0rad)
  baseObject = -> Body [Edge52]
  diameter = 5
  invert = false
  matchOuter = true
  offset = 0
  type = 3
FEATURE [Part::FeaturePython] Washer002  label="M4-Washer425"  # Fasteners workbench fastener (typed FeaturePython)
  Placement = pos=(6.65146,78.3485,-4.8) rot=(-1,0,0;3.14159rad)
  baseObject = -> Body [Edge88]
  diameter = 5
  invert = false
  matchOuter = true
  offset = 0
  type = 3
FEATURE [Part::FeaturePython] Washer003  label="M4-Washer426"  # Fasteners workbench fastener (typed FeaturePython)
  Placement = pos=(7.5,7.5,0) rot=(-1,0,0;3.14159rad)
  baseObject = -> Body [Edge54]
  diameter = 5
  invert = false
  matchOuter = true
  offset = 0
  type = 3
FEATURE [Part::FeaturePython] Screw  label="M4x14-Screw"  # Fasteners workbench fastener (typed FeaturePython)
  Placement = pos=(7.5,7.5,-0.9) rot=(-1,0,0;3.14159rad)
  baseObject = -> Washer003 [Edge1]
  diameter = 5
  invert = false
  length = 4
  lengthCustom = 14
  matchOuter = false
  offset = 0
  thread = false
  type = 34
FEATURE [Part::FeaturePython] Screw001  label="M4x12-Screw"  # Fasteners workbench fastener (typed FeaturePython)
  Placement = pos=(99.5,45.5,-10.9) rot=(-1,0,0;3.14159rad)
  baseObject = -> Washer [Edge1]
  diameter = 5
  invert = false
  length = 3
  lengthCustom = 12
  matchOuter = false
  offset = 0
  thread = false
  type = 34
FEATURE [Part::FeaturePython] Screw002  label="M4x12-Screw281"  # Fasteners workbench fastener (typed FeaturePython)
  Placement = pos=(123.349,78.3485,0.9) rot=(0,0,1;0rad)
  baseObject = -> Washer001 [Edge1]
  diameter = 5
  invert = false
  length = 3
  lengthCustom = 12
  matchOuter = false
  offset = 0
  thread = false
  type = 34
FEATURE [Part::FeaturePython] Screw003  label="M4x12-Screw282"  # Fasteners workbench fastener (typed FeaturePython)
  Placement = pos=(6.65146,78.3485,-5.7) rot=(-1,0,0;3.14159rad)
  baseObject = -> Washer002 [Edge1]
  diameter = 5
  invert = false
  length = 3
  lengthCustom = 12
  matchOuter = false
  offset = 0
  thread = false
  type = 34
FEATURE [App::DocumentObjectGroup] Fasteners
  Group = -> [Washer,Washer001,Washer002,Washer003,Screw,Screw001,Screw002,Screw003]
FEATURE [App::Part] Assembly
  AssemblyType = Part::Link
  Group = -> [LCS_Origin,Variables,Constraints,Configurations,Base,Front_inkl__Fasteners,Fasteners,Washer,Washer001,Washer002,Washer003,Screw,Screw001,Screw002,Screw003]
  Origin = -> Origin013
  Type = Assembly
FEATURE [PartDesign::Fillet] Fillet
  Base = -> Pad001 [Edge3,Edge19,Edge1,Edge6]
  BaseFeature = -> Pad001
  Radius = 7.5
  SupportTransform = false
FEATURE [Sketcher::SketchObject] Sketch
  ExternalGeometry = -> [Fillet]
  FullyConstrained = true
  MapMode = 5
  Placement = pos=(0,0,0) rot=(1,0,0;3.14159rad)
  Support = -> [Fillet]
  sketch-geometry (17):
    g0: LineSegment StartX=6.65146 StartY=-6.65148 StartZ=0 EndX=123.349 EndY=-6.65148 EndZ=0
    g1: LineSegment StartX=123.349 StartY=-6.65148 StartZ=0 EndX=123.349 EndY=-78.3485 EndZ=0
    g2: LineSegment StartX=123.349 StartY=-78.3485 StartZ=0 EndX=6.65146 EndY=-78.3485 EndZ=0
    g3: LineSegment StartX=6.65146 StartY=-78.3485 StartZ=0 EndX=6.65146 EndY=-6.65148 EndZ=0
    g4: GeomPoint X=65 Y=-42.5 Z=0
    g5: Circle CenterX=123.349 CenterY=-6.65148 CenterZ=0 NormalX=0 NormalY=0 NormalZ=1 AngleXU=0 Radius=2.8
    g6: Circle CenterX=123.349 CenterY=-78.3485 CenterZ=0 NormalX=0 NormalY=0 NormalZ=1 AngleXU=0 Radius=2.8
    g7: Circle CenterX=6.65146 CenterY=-78.3485 CenterZ=0 NormalX=0 NormalY=0 NormalZ=1 AngleXU=0 Radius=2.8
    g8: Circle CenterX=6.65146 CenterY=-6.65148 CenterZ=0 NormalX=0 NormalY=0 NormalZ=1 AngleXU=0 Radius=2.8
    g9: LineSegment StartX=3.85146 StartY=-5.49168 StartZ=0 EndX=3.85146 EndY=-6.65148 EndZ=0
    g10: LineSegment StartX=3.85146 StartY=-5.49168 StartZ=0 EndX=9.34315 EndY=0 EndZ=0
    g11: LineSegment StartX=0 StartY=-4.3934 StartZ=0 EndX=4.3934 EndY=0 EndZ=0
    g12: LineSegment StartX=4.67157 StartY=-4.67157 StartZ=0 EndX=2.1967 EndY=-2.1967 EndZ=0
    g13: GeomPoint X=4.67157 Y=-4.67157 Z=0
    g14: GeomPoint X=2.1967 Y=-2.1967 Z=0
    g15: LineSegment StartX=11.0711 StartY=-11.0711 StartZ=0 EndX=22.1421 EndY=0 EndZ=0
    g16: LineSegment StartX=8.63137 StartY=-8.63137 StartZ=0 EndX=17.2627 EndY=0 EndZ=0
  constraints (45):
    c: Coincident(g0,g1)
    c: Coincident(g1,g2)
    c: Coincident(g2,g3)
    c: Coincident(g3,g0)
    c: Horizontal(g0)
    c: Horizontal(g2)
    c: Vertical(g1)
    c: Vertical(g3)
    c: Symmetric(g-3,g-4,g4)
    c: Symmetric(g2,g0,g4)
    c: Coincident(g5,g0)
    c: Coincident(g6,g1)
    c: Coincident(g7,g2)
    c: Diameter(g7) = 5.6
    c: Coincident(g8,g0)
    c: Equal(g5,g6)
    c: Equal(g6,g7)
    c: Equal(g7,g8)
    c: Vertical(g9)
    c: DistanceX(g-4,g9) = 3.85146
    c: Coincident(g10,g9)
    c: PointOnObject(g11,g-1)
    c: Parallel(g10,g11)
    c: Tangent(g-5,g11)
    c: Angle(g9,g10) = 2.35619
    c: PointOnObject(g11,g-2)
    c: Tangent(g10,g8)
    c: PointOnObject(g12,g10)
    c: PointOnObject(g12,g11)
    c: Perpendicular(g10,g12)
    c: Distance(g12) = 3.5
    c: PointOnObject(g10,g-1)
    c: PointOnObject(g13,g8)
    c: Coincident(g13,g12)
    c: PointOnObject(g14,g-5)
    c: Coincident(g12,g14)
    c: Tangent(g9,g8) = -1.5708
    c: PointOnObject(g15,g-1)
    c: Parallel(g15,g10)
    c: PointOnObject(g16,g8)
    c: PointOnObject(g16,g-1)
    c: Tangent(g16,g8)
    c: Parallel(g15,g16)
    c: Distance(g16,g15) = 3.45025
    c: Tangent(g15,g-6) = -1.5708
FEATURE [PartDesign::Pocket] Pocket
  BaseFeature = -> Fillet
  Direction = (0,0,1)
  Length = 10
  Length2 = 5
  Profile = -> Sketch
  ReferenceAxis = -> Sketch [N_Axis]
  Type = 0
FEATURE [PartDesign::ShapeBinder] ShapeBinder
  Support = -> [Pocket]
  TraceSupport = true
FEATURE [Sketcher::SketchObject] Sketch010
  ExternalGeometry = -> [ShapeBinder]
  FullyConstrained = true
  MapMode = 5
  Placement = pos=(0,0,0) rot=(1,0,0;3.14159rad)
  Support = -> [ShapeBinder]
  sketch-geometry (23):
    g0: GeomPoint X=5 Y=-5 Z=0
    g1: GeomPoint X=125 Y=-80 Z=0
    g2: GeomPoint X=65 Y=-42.5 Z=0
    g3: ArcOfCircle CenterX=5 CenterY=-80 CenterZ=0 NormalX=0 NormalY=0 NormalZ=1 AngleXU=0 Radius=10 StartAngle=0.167448 EndAngle=1.40335
    g4: ArcOfCircle CenterX=7 CenterY=-68.1678 CenterZ=0 NormalX=0 NormalY=0 NormalZ=1 AngleXU=0 Radius=2 StartAngle=3.14159 EndAngle=4.54494
    g5: ArcOfCircle CenterX=5 CenterY=-5 CenterZ=0 NormalX=0 NormalY=0 NormalZ=1 AngleXU=0 Radius=10 StartAngle=4.87984 EndAngle=6.11574
    g6: ArcOfCircle CenterX=125 CenterY=-5 CenterZ=0 NormalX=0 NormalY=0 NormalZ=1 AngleXU=0 Radius=10 StartAngle=3.30904 EndAngle=4.54494
    g7: ArcOfCircle CenterX=125 CenterY=-80 CenterZ=0 NormalX=0 NormalY=0 NormalZ=1 AngleXU=0 Radius=10 StartAngle=1.73824 EndAngle=2.97414
    g8: LineSegment StartX=5 StartY=-80 StartZ=0 EndX=125 EndY=-80 EndZ=0
    g9: LineSegment StartX=125 StartY=-80 StartZ=0 EndX=125 EndY=-5 EndZ=0
    g10: LineSegment StartX=5 StartY=-5 StartZ=0 EndX=5 EndY=-80 EndZ=0
    g11: ArcOfCircle CenterX=7 CenterY=-16.8322 CenterZ=0 NormalX=0 NormalY=0 NormalZ=1 AngleXU=0 Radius=2 StartAngle=1.73824 EndAngle=3.14159
    g12: ArcOfCircle CenterX=123 CenterY=-16.8322 CenterZ=0 NormalX=0 NormalY=0 NormalZ=1 AngleXU=0 Radius=2 StartAngle=9e-16 EndAngle=1.40335
    g13: ArcOfCircle CenterX=16.8322 CenterY=-7 CenterZ=0 NormalX=0 NormalY=0 NormalZ=1 AngleXU=0 Radius=2 StartAngle=1.5708 EndAngle=2.97414
    g14: ArcOfCircle CenterX=113.168 CenterY=-7 CenterZ=0 NormalX=0 NormalY=0 NormalZ=1 AngleXU=0 Radius=2 StartAngle=0.167448 EndAngle=1.5708
    g15: ArcOfCircle CenterX=123 CenterY=-68.1678 CenterZ=0 NormalX=0 NormalY=0 NormalZ=1 AngleXU=0 Radius=2 StartAngle=4.87984 EndAngle=6.28319
    g16: ArcOfCircle CenterX=113.168 CenterY=-78 CenterZ=0 NormalX=0 NormalY=0 NormalZ=1 AngleXU=0 Radius=2 StartAngle=4.71239 EndAngle=6.11574
    g17: ArcOfCircle CenterX=16.8322 CenterY=-78 CenterZ=0 NormalX=0 NormalY=0 NormalZ=1 AngleXU=0 Radius=2 StartAngle=3.30904 EndAngle=4.71239
    g18: LineSegment StartX=5 StartY=-5 StartZ=0 EndX=125 EndY=-5 EndZ=0
    g19: LineSegment StartX=5 StartY=-16.8322 StartZ=0 EndX=5 EndY=-68.1678 EndZ=0
    g20: LineSegment StartX=125 StartY=-68.1678 StartZ=0 EndX=125 EndY=-16.8322 EndZ=0
    g21: LineSegment StartX=113.168 StartY=-5 StartZ=0 EndX=16.8322 EndY=-5 EndZ=0
    g22: LineSegment StartX=16.8322 StartY=-80 StartZ=0 EndX=113.168 EndY=-80 EndZ=0
  constraints (54):
    c: Tangent(g3,g4) = 1.5708
    c: Coincident(g7,g1)
    c: Coincident(g8,g9)
    c: Coincident(g10,g8)
    c: Horizontal(g8)
    c: Vertical(g9)
    c: Vertical(g10)
    c: Coincident(g8,g3)
    c: Coincident(g9,g6)
    c: Coincident(g0,g5)
    c: Symmetric(g3,g6,g2)
    c: Tangent(g5,g11) = 1.5708
    c: Tangent(g6,g12) = 1.5708
    c: Tangent(g5,g13) = 1.5708
    c: Tangent(g6,g14) = 1.5708
    c: Tangent(g7,g15) = 1.5708
    c: Tangent(g7,g16) = 1.5708
    c: Equal(g3,g5)
    c: Equal(g5,g6)
    c: Equal(g6,g7)
    c: Radius(g3) = 10
    c: Equal(g4,g13)
    c: Equal(g13,g11)
    c: Equal(g11,g14)
    c: Equal(g12,g15)
    c: Tangent(g16,g8) = -1.5708
    c: Tangent(g4,g10) = -1.5708
    c: Coincident(g8,g7)
    c: Tangent(g17,g8) = -1.5708
    c: Tangent(g17,g3) = 1.5708
    c: Radius(g17) = 2
    c: Tangent(g12,g9) = -1.5708
    c: Tangent(g15,g9) = -1.5708
    c: Tangent(g11,g10) = -1.5708
    c: Coincident(g18,g5)
    c: Horizontal(g18)
    c: Coincident(g18,g6)
    c: Coincident(g10,g5)
    c: Tangent(g13,g18) = 1.5708
    c: Tangent(g14,g18) = 1.5708
    c: Equal(g11,g12)
    c: Equal(g14,g17)
    c: Equal(g17,g16)
    c: Symmetric(g-3,g-5,g2)
    c: Coincident(g19,g11)
    c: Coincident(g19,g4)
    c: Coincident(g20,g15)
    c: Coincident(g20,g12)
    c: Coincident(g21,g14)
    c: Coincident(g21,g13)
    c: DistanceY(g5,g-4) = 1
    c: DistanceX(g-5,g11) = 1
    c: Coincident(g22,g17)
    c: Coincident(g22,g16)
FEATURE [Sketcher::SketchObject] Sketch011
  ExternalGeometry = -> [ShapeBinder]
  FullyConstrained = true
  MapMode = 5
  Placement = pos=(0,0,0) rot=(1,0,0;3.14159rad)
  Support = -> [ShapeBinder]
  sketch-geometry (12):
    g0: LineSegment StartX=7.5 StartY=0 StartZ=0 EndX=122.5 EndY=0 EndZ=0
    g1: LineSegment StartX=130 StartY=-7.5 StartZ=0 EndX=130 EndY=-77.5 EndZ=0
    g2: LineSegment StartX=122.5 StartY=-85 StartZ=0 EndX=7.5 EndY=-85 EndZ=0
    g3: LineSegment StartX=0 StartY=-77.5 StartZ=0 EndX=0 EndY=-7.5 EndZ=0
    g4: ArcOfCircle CenterX=7.5 CenterY=-7.5 CenterZ=0 NormalX=0 NormalY=0 NormalZ=1 AngleXU=0 Radius=7.5 StartAngle=1.5708 EndAngle=3.14159
    g5: GeomPoint X=0 Y=0 Z=0
    g6: ArcOfCircle CenterX=122.5 CenterY=-7.5 CenterZ=0 NormalX=0 NormalY=0 NormalZ=1 AngleXU=0 Radius=7.5 StartAngle=0 EndAngle=1.5708
    g7: GeomPoint X=130 Y=0 Z=0
    g8: ArcOfCircle CenterX=122.5 CenterY=-77.5 CenterZ=0 NormalX=0 NormalY=0 NormalZ=1 AngleXU=0 Radius=7.5 StartAngle=4.71239 EndAngle=6.28319
    g9: GeomPoint X=130 Y=-85 Z=0
    g10: ArcOfCircle CenterX=7.5 CenterY=-77.5 CenterZ=0 NormalX=0 NormalY=0 NormalZ=1 AngleXU=0 Radius=7.5 StartAngle=3.14159 EndAngle=4.71239
    g11: GeomPoint X=0 Y=-85 Z=0
  constraints (23):
    c: Horizontal(g0)
    c: Vertical(g1)
    c: Vertical(g3)
    c: Coincident(g5,g-1)
    c: PointOnObject(g5,g3)
    c: Tangent(g0,g4) = 1.5708
    c: Tangent(g3,g4) = 1.5708
    c: PointOnObject(g7,g1)
    c: PointOnObject(g7,g0)
    c: Tangent(g1,g6) = 1.5708
    c: Tangent(g0,g6) = 1.5708
    c: PointOnObject(g9,g1)
    c: PointOnObject(g9,g2)
    c: Tangent(g1,g8) = 1.5708
    c: Tangent(g2,g8) = 1.5708
    c: PointOnObject(g11,g2)
    c: PointOnObject(g11,g3)
    c: Tangent(g2,g10) = 1.5708
    c: Tangent(g3,g10) = 1.5708
    c: Coincident(g2,g-4)
    c: Coincident(g2,g-4)
    c: Coincident(g-3,g1)
    c: Coincident(g0,g-5)
FEATURE [PartDesign::Pad] Pad003
  Direction = (0,0,-1)
  Length = 10
  Length2 = 10
  Profile = -> Sketch011
  ReferenceAxis = -> Sketch011 [N_Axis]
  Type = 0
FEATURE [PartDesign::Pocket] Pocket005
  BaseFeature = -> Pad003
  Direction = (0,0,1)
  Length = 7
  Length2 = 5
  Profile = -> Sketch010
  ReferenceAxis = -> Sketch010 [N_Axis]
  Reversed = true
  Type = 0
FEATURE [Sketcher::SketchObject] Sketch012
  ExternalGeometry = -> [ShapeBinder]
  FullyConstrained = true
  MapMode = 5
  Placement = pos=(0,0,-10) rot=(1,0,0;3.14159rad)
  Support = -> [Pocket005]
  sketch-geometry (4):
    g0: Circle CenterX=6.65146 CenterY=-6.65148 CenterZ=0 NormalX=0 NormalY=0 NormalZ=1 AngleXU=0 Radius=2.8
    g1: Circle CenterX=123.349 CenterY=-6.65148 CenterZ=0 NormalX=0 NormalY=0 NormalZ=1 AngleXU=0 Radius=2.8
    g2: Circle CenterX=123.349 CenterY=-78.3485 CenterZ=0 NormalX=0 NormalY=0 NormalZ=1 AngleXU=0 Radius=2.8
    g3: Circle CenterX=6.65146 CenterY=-78.3485 CenterZ=0 NormalX=0 NormalY=0 NormalZ=1 AngleXU=0 Radius=2.8
  constraints (8):
    c: Coincident(g1,g-4)
    c: Coincident(g2,g-5)
    c: Coincident(g3,g-6)
    c: Coincident(g0,g-3)
    c: Equal(g0,g-3)
    c: Equal(g0,g1)
    c: Equal(g1,g2)
    c: Equal(g2,g3)
FEATURE [PartDesign::Hole] Hole
  BaseFeature = -> Pocket005
  CustomThreadClearance = 0
  Depth = 314.401
  DepthType = 1
  Diameter = 4.5
  DrillForDepth = false
  DrillPoint = 1
  DrillPointAngle = 118
  HoleCutCountersinkAngle = 90
  HoleCutCustomValues = false
  HoleCutDepth = 5.2
  HoleCutDiameter = 10
  HoleCutType = 12
  ModelThread = false
  Profile = -> Sketch012
  Tapered = false
  TaperedAngle = 90
  ThreadClass = 0
  ThreadDepth = 314.401
  ThreadDepthType = 0
  ThreadDirection = 0
  ThreadFit = 0
  ThreadSize = 11
  ThreadType = 1
  Threaded = false
  UseCustomThreadClearance = false
FEATURE [Sketcher::SketchObject] Sketch013
  ExternalGeometry = -> [ShapeBinder]
  FullyConstrained = true
  MapMode = 5
  Placement = pos=(0,0,0) rot=(1,0,0;3.14159rad)
  Support = -> [ShapeBinder]
  sketch-geometry (46):
    g0: GeomPoint X=5 Y=-5 Z=0
    g1: GeomPoint X=125 Y=-80 Z=0
    g2: GeomPoint X=65 Y=-42.5 Z=0
    g3: ArcOfCircle CenterX=5 CenterY=-80 CenterZ=0 NormalX=0 NormalY=0 NormalZ=1 AngleXU=0 Radius=10 StartAngle=0.167448 EndAngle=1.40335
    g4: ArcOfCircle CenterX=7 CenterY=-68.1678 CenterZ=0 NormalX=0 NormalY=0 NormalZ=1 AngleXU=0 Radius=2 StartAngle=3.14159 EndAngle=4.54494
    g5: ArcOfCircle CenterX=5 CenterY=-5 CenterZ=0 NormalX=0 NormalY=0 NormalZ=1 AngleXU=0 Radius=10 StartAngle=4.87984 EndAngle=6.11574
    g6: ArcOfCircle CenterX=125 CenterY=-5 CenterZ=0 NormalX=0 NormalY=0 NormalZ=1 AngleXU=0 Radius=10 StartAngle=3.30904 EndAngle=4.54494
    g7: ArcOfCircle CenterX=125 CenterY=-80 CenterZ=0 NormalX=0 NormalY=0 NormalZ=1 AngleXU=0 Radius=10 StartAngle=1.73824 EndAngle=2.97414
    g8: LineSegment StartX=5 StartY=-80 StartZ=0 EndX=125 EndY=-80 EndZ=0
    g9: LineSegment StartX=125 StartY=-80 StartZ=0 EndX=125 EndY=-5 EndZ=0
    g10: LineSegment StartX=5 StartY=-5 StartZ=0 EndX=5 EndY=-80 EndZ=0
    g11: ArcOfCircle CenterX=7 CenterY=-16.8322 CenterZ=0 NormalX=0 NormalY=0 NormalZ=1 AngleXU=0 Radius=2 StartAngle=1.73824 EndAngle=3.14159
    g12: ArcOfCircle CenterX=123 CenterY=-16.8322 CenterZ=0 NormalX=0 NormalY=0 NormalZ=1 AngleXU=0 Radius=2 StartAngle=-9e-16 EndAngle=1.40335
    g13: ArcOfCircle CenterX=16.8322 CenterY=-7 CenterZ=0 NormalX=0 NormalY=0 NormalZ=1 AngleXU=0 Radius=2 StartAngle=1.5708 EndAngle=2.97414
    g14: ArcOfCircle CenterX=113.168 CenterY=-7 CenterZ=0 NormalX=0 NormalY=0 NormalZ=1 AngleXU=0 Radius=2 StartAngle=0.167448 EndAngle=1.5708
    g15: ArcOfCircle CenterX=123 CenterY=-68.1678 CenterZ=0 NormalX=0 NormalY=0 NormalZ=1 AngleXU=0 Radius=2 StartAngle=4.87984 EndAngle=6.28319
    g16: ArcOfCircle CenterX=113.168 CenterY=-78 CenterZ=0 NormalX=0 NormalY=0 NormalZ=1 AngleXU=0 Radius=2 StartAngle=4.71239 EndAngle=6.11574
    g17: ArcOfCircle CenterX=16.8322 CenterY=-78 CenterZ=0 NormalX=0 NormalY=0 NormalZ=1 AngleXU=0 Radius=2 StartAngle=3.30904 EndAngle=4.71239
    g18: LineSegment StartX=5 StartY=-5 StartZ=0 EndX=125 EndY=-5 EndZ=0
    g19: LineSegment StartX=5 StartY=-16.8322 StartZ=0 EndX=5 EndY=-68.1678 EndZ=0
    g20: LineSegment StartX=125 StartY=-68.1678 StartZ=0 EndX=125 EndY=-16.8322 EndZ=0
    g21: LineSegment StartX=113.168 StartY=-5 StartZ=0 EndX=16.8322 EndY=-5 EndZ=0
    g22: LineSegment StartX=16.8322 StartY=-80 StartZ=0 EndX=113.168 EndY=-80 EndZ=0
    g23: GeomPoint X=4 Y=-4 Z=0
    g24: GeomPoint X=126 Y=-81 Z=0
    g25: GeomPoint X=65 Y=-42.5 Z=0
    g26: ArcOfCircle CenterX=4 CenterY=-81 CenterZ=0 NormalX=0 NormalY=0 NormalZ=1 AngleXU=0 Radius=10 StartAngle=0.167448 EndAngle=1.40335
    g27: ArcOfCircle CenterX=6 CenterY=-69.1678 CenterZ=0 NormalX=0 NormalY=0 NormalZ=1 AngleXU=0 Radius=2 StartAngle=3.14159 EndAngle=4.54494
    g28: ArcOfCircle CenterX=4 CenterY=-4 CenterZ=0 NormalX=0 NormalY=0 NormalZ=1 AngleXU=0 Radius=10 StartAngle=4.87984 EndAngle=6.11574
    g29: ArcOfCircle CenterX=126 CenterY=-4 CenterZ=0 NormalX=0 NormalY=0 NormalZ=1 AngleXU=0 Radius=10 StartAngle=3.30904 EndAngle=4.54494
    g30: ArcOfCircle CenterX=126 CenterY=-81 CenterZ=0 NormalX=0 NormalY=0 NormalZ=1 AngleXU=0 Radius=10 StartAngle=1.73824 EndAngle=2.97414
    g31: LineSegment StartX=4 StartY=-81 StartZ=0 EndX=126 EndY=-81 EndZ=0
    g32: LineSegment StartX=126 StartY=-81 StartZ=0 EndX=126 EndY=-4 EndZ=0
    g33: LineSegment StartX=4 StartY=-4 StartZ=0 EndX=4 EndY=-81 EndZ=0
    g34: ArcOfCircle CenterX=6 CenterY=-15.8322 CenterZ=0 NormalX=0 NormalY=0 NormalZ=1 AngleXU=0 Radius=2 StartAngle=1.73824 EndAngle=3.14159
    g35: ArcOfCircle CenterX=124 CenterY=-15.8322 CenterZ=0 NormalX=0 NormalY=0 NormalZ=1 AngleXU=0 Radius=2 StartAngle=3e-16 EndAngle=1.40335
    g36: ArcOfCircle CenterX=15.8322 CenterY=-6 CenterZ=0 NormalX=0 NormalY=0 NormalZ=1 AngleXU=0 Radius=2 StartAngle=1.5708 EndAngle=2.97414
    g37: ArcOfCircle CenterX=114.168 CenterY=-6 CenterZ=0 NormalX=0 NormalY=0 NormalZ=1 AngleXU=0 Radius=2 StartAngle=0.167448 EndAngle=1.5708
    g38: ArcOfCircle CenterX=124 CenterY=-69.1678 CenterZ=0 NormalX=0 NormalY=0 NormalZ=1 AngleXU=0 Radius=2 StartAngle=4.87984 EndAngle=6.28319
    g39: ArcOfCircle CenterX=114.168 CenterY=-79 CenterZ=0 NormalX=0 NormalY=0 NormalZ=1 AngleXU=0 Radius=2 StartAngle=4.71239 EndAngle=6.11574
    g40: ArcOfCircle CenterX=15.8322 CenterY=-79 CenterZ=0 NormalX=0 NormalY=0 NormalZ=1 AngleXU=0 Radius=2 StartAngle=3.30904 EndAngle=4.71239
    g41: LineSegment StartX=4 StartY=-4 StartZ=0 EndX=126 EndY=-4 EndZ=0
    g42: LineSegment StartX=4 StartY=-15.8322 StartZ=0 EndX=4 EndY=-69.1678 EndZ=0
    g43: LineSegment StartX=126 StartY=-69.1678 StartZ=0 EndX=126 EndY=-15.8322 EndZ=0
    g44: LineSegment StartX=114.168 StartY=-4 StartZ=0 EndX=15.8322 EndY=-4 EndZ=0
    g45: LineSegment StartX=15.8322 StartY=-81 StartZ=0 EndX=114.168 EndY=-81 EndZ=0
  constraints (107):
    c: Tangent(g3,g4) = 1.5708
    c: Coincident(g7,g1)
    c: Coincident(g8,g9)
    c: Coincident(g10,g8)
    c: Horizontal(g8)
    c: Vertical(g9)
    c: Vertical(g10)
    c: Coincident(g8,g3)
    c: Coincident(g9,g6)
    c: Coincident(g0,g5)
    c: Symmetric(g3,g6,g2)
    c: Tangent(g5,g11) = 1.5708
    c: Tangent(g6,g12) = 1.5708
    c: Tangent(g5,g13) = 1.5708
    c: Tangent(g6,g14) = 1.5708
    c: Tangent(g7,g15) = 1.5708
    c: Tangent(g7,g16) = 1.5708
    c: Equal(g3,g5)
    c: Equal(g5,g6)
    c: Equal(g6,g7)
    c: Radius(g3) = 10
    c: Equal(g4,g13)
    c: Equal(g13,g11)
    c: Equal(g11,g14)
    c: Equal(g12,g15)
    c: Tangent(g16,g8) = -1.5708
    c: Tangent(g4,g10) = -1.5708
    c: Coincident(g8,g7)
    c: Tangent(g17,g8) = -1.5708
    c: Tangent(g17,g3) = 1.5708
    c: Radius(g17) = 2
    c: Tangent(g12,g9) = -1.5708
    c: Tangent(g15,g9) = -1.5708
    c: Tangent(g11,g10) = -1.5708
    c: Coincident(g18,g5)
    c: Horizontal(g18)
    c: Coincident(g18,g6)
    c: Coincident(g10,g5)
    c: Tangent(g13,g18) = 1.5708
    c: Tangent(g14,g18) = 1.5708
    c: Equal(g11,g12)
    c: Equal(g14,g17)
    c: Equal(g17,g16)
    c: Coincident(g19,g11)
    c: Coincident(g19,g4)
    c: Coincident(g20,g15)
    c: Coincident(g20,g12)
    c: Coincident(g21,g14)
    c: Coincident(g21,g13)
    c: Coincident(g22,g17)
    c: Coincident(g22,g16)
    c: Tangent(g26,g27) = 1.5708
    c: Coincident(g30,g24)
    c: Coincident(g31,g32)
    c: Coincident(g33,g31)
    c: Horizontal(g31)
    c: Vertical(g32)
    c: Vertical(g33)
    c: Coincident(g31,g26)
    c: Coincident(g32,g29)
    c: Coincident(g23,g28)
    c: Symmetric(g26,g29,g25)
    c: Tangent(g28,g34) = 1.5708
    c: Tangent(g29,g35) = 1.5708
    c: Tangent(g28,g36) = 1.5708
    c: Tangent(g29,g37) = 1.5708
    c: Tangent(g30,g38) = 1.5708
    c: Tangent(g30,g39) = 1.5708
    c: Equal(g26,g28)
    c: Equal(g28,g29)
    c: Equal(g29,g30)
    c: Radius(g26) = 10
    c: Equal(g27,g36)
    c: Equal(g36,g34)
    c: Equal(g34,g37)
    c: Equal(g35,g38)
    c: Tangent(g39,g31) = -1.5708
    c: Tangent(g27,g33) = -1.5708
    c: Coincident(g31,g30)
    c: Tangent(g40,g31) = -1.5708
    c: Tangent(g40,g26) = 1.5708
    c: Radius(g40) = 2
    c: Tangent(g35,g32) = -1.5708
    c: Tangent(g38,g32) = -1.5708
    c: Tangent(g34,g33) = -1.5708
    c: Coincident(g41,g28)
    c: Horizontal(g41)
    c: Coincident(g41,g29)
    c: Coincident(g33,g28)
    c: Tangent(g36,g41) = 1.5708
    c: Tangent(g37,g41) = 1.5708
    c: Equal(g34,g35)
    c: Equal(g37,g40)
    c: Equal(g40,g39)
    c: Coincident(g42,g34)
    c: Coincident(g42,g27)
    c: Coincident(g43,g38)
    c: Coincident(g43,g35)
    c: Coincident(g44,g37)
    c: Coincident(g44,g36)
    c: Coincident(g45,g40)
    c: Coincident(g45,g39)
    c: Symmetric(g28,g30,g2)
    c: Coincident(g34,g-3)
    c: Coincident(g38,g-4)
    c: DistanceX(g27,g4) = 1
    c: DistanceY(g40,g17) = 1
FEATURE [PartDesign::Pad] Pad004
  BaseFeature = -> Hole
  Direction = (0,0,-1)
  Length = 10
  Length2 = 10
  Profile = -> Sketch013
  ReferenceAxis = -> Sketch013 [N_Axis]
  Reversed = true
  Type = 0
FEATURE [PartDesign::CoordinateSystem] LCS_1
  AttacherType = Attacher::AttachEngine3D
  MapMode = 5
  Support = -> [Pad004]
FEATURE [PartDesign::CoordinateSystem] LCS_2
  AttacherType = Attacher::AttachEngine3D
  AttachmentOffset = pos=(0,0,0) rot=(1,0,0;3.14159rad)
  MapMode = 5
  Support = -> [Pocket]
FEATURE [PartDesign::CoordinateSystem] LCS_3
  AttacherType = Attacher::AttachEngine3D
  MapMode = 2
  Support = -> [Pocket]
FEATURE [PartDesign::Line] HoleAxis_1
  AttacherType = Attacher::AttachEngineLine
  Length = 4.79083
  MapMode = 19
  Placement = pos=(123.349,6.65148,-4.8) rot=(0,1,0;3.14159rad)
  ResizeMode = 1
  Support = -> [Pad004]
FEATURE [PartDesign::Line] HoleAxis_2
  AttacherType = Attacher::AttachEngineLine
  Length = 4.79083
  MapMode = 19
  Placement = pos=(123.349,78.3485,-4.8) rot=(0,1,0;3.14159rad)
  ResizeMode = 1
  Support = -> [Pad004]
FEATURE [PartDesign::Line] HoleAxis_3
  AttacherType = Attacher::AttachEngineLine
  Length = 4.79083
  MapMode = 19
  Placement = pos=(6.65146,78.3485,-4.8) rot=(0,1,0;3.14159rad)
  ResizeMode = 1
  Support = -> [Pad004]
FEATURE [PartDesign::Line] HoleAxis_4
  AttacherType = Attacher::AttachEngineLine
  Length = 4.79083
  MapMode = 19
  Placement = pos=(6.65146,6.65148,-4.8) rot=(0,1,0;3.14159rad)
  ResizeMode = 1
  Support = -> [Pad004]
FEATURE [Sketcher::SketchObject] Sketch008
  ExternalGeometry = -> [Pad001]
  FullyConstrained = true
  MapMode = 5
  Placement = pos=(0,0,16) rot=(1,0,0;3.14159rad)
  Support = -> [Pad001]
  sketch-geometry (11):
    g0: LineSegment StartX=8 StartY=-42.5 StartZ=0 EndX=28 EndY=-42.5 EndZ=0
    g1: LineSegment StartX=28 StartY=-42.5 StartZ=0 EndX=28 EndY=-67 EndZ=0
    g2: LineSegment StartX=28 StartY=-67 StartZ=0 EndX=8 EndY=-67 EndZ=0
    g3: LineSegment StartX=8 StartY=-67 StartZ=0 EndX=8 EndY=-42.5 EndZ=0
    g4: GeomPoint X=8 Y=-42.5 Z=0
    g5: GeomPoint X=4 Y=-42.5 Z=0
    g6: LineSegment StartX=4 StartY=-42.5 StartZ=0 EndX=8 EndY=-42.5 EndZ=0
    g7: LineSegment StartX=6 StartY=-17.8322 StartZ=0 EndX=36.5 EndY=-17.8322 EndZ=0
    g8: LineSegment StartX=36.5 StartY=-17.8322 StartZ=0 EndX=36.5 EndY=-29.3322 EndZ=0
    g9: LineSegment StartX=36.5 StartY=-29.3322 StartZ=0 EndX=6 EndY=-29.3322 EndZ=0
    g10: LineSegment StartX=6 StartY=-29.3322 StartZ=0 EndX=6 EndY=-17.8322 EndZ=0
  constraints (28):
    c: Coincident(g0,g1)
    c: Coincident(g1,g2)
    c: Coincident(g2,g3)
    c: Coincident(g3,g0)
    c: Horizontal(g0)
    c: Horizontal(g2)
    c: Vertical(g1)
    c: Vertical(g3)
    c: DistanceX(g0,g0) = 20
    c: Symmetric(g-3,g-3,g5)
    c: Coincident(g6,g5)
    c: Coincident(g6,g4)
    c: Horizontal(g6)
    c: DistanceX(g6,g6) = 4
    c: DistanceY(g3,g3) = 24.5
    c: Coincident(g0,g4)
    c: Coincident(g7,g8)
    c: Coincident(g8,g9)
    c: Coincident(g9,g10)
    c: Coincident(g10,g7)
    c: Horizontal(g7)
    c: Horizontal(g9)
    c: Vertical(g8)
    c: Vertical(g10)
    c: DistanceY(g8,g8) = 11.5
    c: DistanceX(g7,g7) = 30.5
    c: DistanceX(g-3,g7) = 2
    c: DistanceY(g7,g-3) = 2
FEATURE [PartDesign::Pocket] Pocket006
  BaseFeature = -> Pocket
  Direction = (0,0,1)
  Length = 2
  Length2 = 5
  Profile = -> Sketch008
  ReferenceAxis = -> Sketch008 [N_Axis]
  Refine = true
  Type = 0
FEATURE [PartDesign::Body] Body002  label="Front"
  Group = -> [Box002,Sketch001,Pocket001,Sketch002,Pocket002,Sketch003,Pocket003,Sketch004,Pad,Sketch005,Pocket004,Sketch007,Pad001,Sketch008,Fillet,Sketch,Pocket,LCS_2,Pocket006]
  Origin = -> Origin002
  Tip = -> Pocket006
FEATURE [App::Part] Part002  label="Front inkl. Fasteners"
  Group = -> [Body002,HeatSet,HeatSet001,HeatSet002,HeatSet003,LCS_3]
  Origin = -> Origin016
FEATURE [Part::Feature] Part__Feature087  label="PG7"
  shape: bbox 26.9 x 16.8 x 15 mm, 69 faces (baked)
FEATURE [Part::Feature] Part__Feature088  label="PG008"
  shape: bbox 6.1 x 9.4 x 9.4 mm, 6 faces (baked)
FEATURE [Part::Feature] Part__Feature089  label="PG009"
  shape: bbox 1 x 17.5 x 17.5 mm, 6 faces (baked)
FEATURE [Part::Feature] Part__Feature090  label="PG010"
  shape: bbox 13.2 x 22.56 x 16.8 mm, 27 faces (baked)
FEATURE [Part::Feature] Part__Feature091  label="PG011"
  Placement = pos=(-1,0,0) rot=(0,0,1;0rad)
  shape: bbox 5.2 x 16.8 x 16.8 mm, 23 faces (baked)
FEATURE [Sketcher::SketchObject] Sketch014
  ExternalGeometry = -> [Pad004]
  FullyConstrained = true
  MapMode = 5
  Placement = pos=(0,0,-7) rot=(0,0,1;0rad)
  Support = -> [Pad004]
  sketch-geometry (3):
    g0: Circle CenterX=65 CenterY=20 CenterZ=0 NormalX=0 NormalY=0 NormalZ=1 AngleXU=0 Radius=6
    g1: GeomPoint X=65 Y=0 Z=0
    g2: LineSegment StartX=65 StartY=0 StartZ=0 EndX=65 EndY=20 EndZ=0
  constraints (6):
    c: Diameter(g0) = 12
    c: Symmetric(g-3,g-3,g1)
    c: Coincident(g2,g1)
    c: Coincident(g2,g0)
    c: Vertical(g2)
    c: DistanceY(g2,g2) = 20
FEATURE [PartDesign::Hole] Hole001
  BaseFeature = -> Pad004
  CustomThreadClearance = 0
  Depth = 25
  DepthType = 0
  Diameter = 12.1
  DrillForDepth = false
  DrillPoint = 1
  DrillPointAngle = 118
  HoleCutCountersinkAngle = 90
  HoleCutCustomValues = false
  HoleCutDepth = 0
  HoleCutDiameter = 13.6
  HoleCutType = 0
  ModelThread = false
  Profile = -> Sketch014
  Refine = true
  Tapered = false
  TaperedAngle = 90
  ThreadClass = 0
  ThreadDepth = 25
  ThreadDepthType = 0
  ThreadDirection = 0
  ThreadFit = 0
  ThreadSize = 19
  ThreadType = 1
  Threaded = false
  UseCustomThreadClearance = false
FEATURE [Sketcher::SketchObject] Sketch015
  ExternalGeometry = -> [HoleAxis_2,HoleAxis_4]
  FullyConstrained = true
  MapMode = 5
  Placement = pos=(0,0,-7) rot=(0,0,1;0rad)
  Support = -> [Hole001]
  sketch-geometry (24):
    g0: ArcOfCircle CenterX=23.5 CenterY=46.5 CenterZ=0 NormalX=0 NormalY=0 NormalZ=1 AngleXU=0 Radius=2 StartAngle=1.5708 EndAngle=3.14159
    g1: LineSegment StartX=23.5 StartY=48.5 StartZ=0 EndX=31.5 EndY=48.5 EndZ=0
    g2: ArcOfCircle CenterX=31.5 CenterY=46.5 CenterZ=0 NormalX=0 NormalY=0 NormalZ=1 AngleXU=0 Radius=2 StartAngle=0 EndAngle=1.5708
    g3: LineSegment StartX=33.5 StartY=46.5 StartZ=0 EndX=33.5 EndY=38.5 EndZ=0
    g4: ArcOfCircle CenterX=31.5 CenterY=38.5 CenterZ=0 NormalX=0 NormalY=0 NormalZ=1 AngleXU=0 Radius=2 StartAngle=4.71239 EndAngle=6.28319
    g5: LineSegment StartX=31.5 StartY=36.5 StartZ=0 EndX=23.5 EndY=36.5 EndZ=0
    g6: ArcOfCircle CenterX=23.5 CenterY=38.5 CenterZ=0 NormalX=0 NormalY=0 NormalZ=1 AngleXU=0 Radius=2 StartAngle=3.14159 EndAngle=4.71239
    g7: LineSegment StartX=21.5 StartY=38.5 StartZ=0 EndX=21.5 EndY=46.5 EndZ=0
    g8: GeomPoint X=21.5 Y=48.5 Z=0
    g9: GeomPoint X=33.5 Y=36.5 Z=0
    g10: ArcOfCircle CenterX=98.5 CenterY=46.5 CenterZ=0 NormalX=0 NormalY=0 NormalZ=1 AngleXU=0 Radius=2 StartAngle=1.5708 EndAngle=3.14159
    g11: LineSegment StartX=98.5 StartY=48.5 StartZ=0 EndX=106.5 EndY=48.5 EndZ=0
    g12: ArcOfCircle CenterX=106.5 CenterY=46.5 CenterZ=0 NormalX=0 NormalY=0 NormalZ=1 AngleXU=0 Radius=2 StartAngle=6e-16 EndAngle=1.5708
    g13: LineSegment StartX=108.5 StartY=46.5 StartZ=0 EndX=108.5 EndY=38.5 EndZ=0
    g14: ArcOfCircle CenterX=106.5 CenterY=38.5 CenterZ=0 NormalX=0 NormalY=0 NormalZ=1 AngleXU=0 Radius=2 StartAngle=4.71239 EndAngle=6.28319
    g15: LineSegment StartX=106.5 StartY=36.5 StartZ=0 EndX=98.5 EndY=36.5 EndZ=0
    g16: ArcOfCircle CenterX=98.5 CenterY=38.5 CenterZ=0 NormalX=0 NormalY=0 NormalZ=1 AngleXU=0 Radius=2 StartAngle=3.14159 EndAngle=4.71239
    g17: LineSegment StartX=96.5 StartY=38.5 StartZ=0 EndX=96.5 EndY=46.5 EndZ=0
    g18: GeomPoint X=96.5 Y=48.5 Z=0
    g19: GeomPoint X=108.5 Y=36.5 Z=0
    g20: GeomPoint X=27.5 Y=42.5 Z=0
    g21: GeomPoint X=102.5 Y=42.5 Z=0
    g22: GeomPoint X=65 Y=42.5 Z=0
    g23: LineSegment StartX=27.5 StartY=42.5 StartZ=0 EndX=102.5 EndY=42.5 EndZ=0
  constraints (53):
    c: Tangent(g0,g1) = 1.5708
    c: Tangent(g1,g2) = 1.5708
    c: Tangent(g2,g3) = 1.5708
    c: Tangent(g3,g4) = 1.5708
    c: Tangent(g4,g5) = 1.5708
    c: Tangent(g5,g6) = 1.5708
    c: Tangent(g6,g7) = 1.5708
    c: Tangent(g7,g0) = 1.5708
    c: Horizontal(g1)
    c: Horizontal(g5)
    c: Vertical(g3)
    c: Vertical(g7)
    c: Equal(g2,g4)
    c: Equal(g4,g6)
    c: PointOnObject(g8,g1)
    c: PointOnObject(g8,g7)
    c: PointOnObject(g9,g3)
    c: PointOnObject(g9,g5)
    c: Tangent(g10,g11) = 1.5708
    c: Tangent(g11,g12) = 1.5708
    c: Tangent(g12,g13) = 1.5708
    c: Tangent(g13,g14) = 1.5708
    c: Tangent(g14,g15) = 1.5708
    c: Tangent(g15,g16) = 1.5708
    c: Tangent(g16,g17) = 1.5708
    c: Tangent(g17,g10) = 1.5708
    c: Horizontal(g11)
    c: Horizontal(g15)
    c: Vertical(g13)
    c: Vertical(g17)
    c: Equal(g10,g12)
    c: Equal(g12,g14)
    c: Equal(g14,g16)
    c: PointOnObject(g18,g11)
    c: PointOnObject(g18,g17)
    c: PointOnObject(g19,g13)
    c: PointOnObject(g19,g15)
    c: Symmetric(g16,g12,g21)
    c: Symmetric(g2,g6,g20)
    c: Equal(g1,g11)
    c: Equal(g3,g13)
    c: Symmetric(g-4,g-3,g22)
    c: Symmetric(g21,g20,g22)
    c: Coincident(g23,g20)
    c: Coincident(g23,g21)
    c: Horizontal(g23)
    c: Equal(g2,g0)
    c: Equal(g6,g16)
    c: Radius(g4) = 2
    c: DistanceX(g8,g9) = 12  'Breite Klickfixadapter'
    c: DistanceY(g9,g8) = 12
    c: DistanceX(g23,g23) = 75
    c: DistanceX(g8,g19) = 87
FEATURE [PartDesign::Pad] Pad005
  BaseFeature = -> Hole001
  Direction = (0,0,1)
  Length = 5
  Length2 = 10
  Profile = -> Sketch015
  ReferenceAxis = -> Sketch015 [N_Axis]
  Refine = true
  Type = 0
FEATURE [Sketcher::SketchObject] Sketch017
  ExternalGeometry = -> [Pad005]
  FullyConstrained = true
  MapMode = 5
  Placement = pos=(0,0,-10) rot=(1,0,0;3.14159rad)
  Support = -> [Pad005]
  sketch-geometry (22):
    g0: ArcOfCircle CenterX=24.5 CenterY=-39.5 CenterZ=0 NormalX=0 NormalY=0 NormalZ=1 AngleXU=0 Radius=2 StartAngle=1.5708 EndAngle=3.14159
    g1: LineSegment StartX=24.5 StartY=-37.5 StartZ=0 EndX=30.5 EndY=-37.5 EndZ=0
    g2: ArcOfCircle CenterX=30.5 CenterY=-39.5 CenterZ=0 NormalX=0 NormalY=0 NormalZ=1 AngleXU=0 Radius=2 StartAngle=-2.7e-15 EndAngle=1.5708
    g3: LineSegment StartX=32.5 StartY=-39.5 StartZ=0 EndX=32.5 EndY=-45.5 EndZ=0
    g4: ArcOfCircle CenterX=30.5 CenterY=-45.5 CenterZ=0 NormalX=0 NormalY=0 NormalZ=1 AngleXU=0 Radius=2 StartAngle=4.71239 EndAngle=6.28319
    g5: LineSegment StartX=30.5 StartY=-47.5 StartZ=0 EndX=24.5 EndY=-47.5 EndZ=0
    g6: ArcOfCircle CenterX=24.5 CenterY=-45.5 CenterZ=0 NormalX=0 NormalY=0 NormalZ=1 AngleXU=0 Radius=2 StartAngle=3.14159 EndAngle=4.71239
    g7: LineSegment StartX=22.5 StartY=-45.5 StartZ=0 EndX=22.5 EndY=-39.5 EndZ=0
    g8: GeomPoint X=22.5 Y=-37.5 Z=0
    g9: GeomPoint X=32.5 Y=-47.5 Z=0
    g10: ArcOfCircle CenterX=99.5 CenterY=-39.5 CenterZ=0 NormalX=0 NormalY=0 NormalZ=1 AngleXU=0 Radius=2 StartAngle=1.5708 EndAngle=3.14159
    g11: LineSegment StartX=99.5 StartY=-37.5 StartZ=0 EndX=105.5 EndY=-37.5 EndZ=0
    g12: ArcOfCircle CenterX=105.5 CenterY=-39.5 CenterZ=0 NormalX=0 NormalY=0 NormalZ=1 AngleXU=0 Radius=2 StartAngle=-7.1e-15 EndAngle=1.5708
    g13: LineSegment StartX=107.5 StartY=-39.5 StartZ=0 EndX=107.5 EndY=-45.5 EndZ=0
    g14: ArcOfCircle CenterX=105.5 CenterY=-45.5 CenterZ=0 NormalX=0 NormalY=0 NormalZ=1 AngleXU=0 Radius=2 StartAngle=4.71239 EndAngle=6.28319
    g15: LineSegment StartX=105.5 StartY=-47.5 StartZ=0 EndX=99.5 EndY=-47.5 EndZ=0
    g16: ArcOfCircle CenterX=99.5 CenterY=-45.5 CenterZ=0 NormalX=0 NormalY=0 NormalZ=1 AngleXU=0 Radius=2 StartAngle=3.14159 EndAngle=4.71239
    g17: LineSegment StartX=97.5 StartY=-45.5 StartZ=0 EndX=97.5 EndY=-39.5 EndZ=0
    g18: GeomPoint X=97.5 Y=-37.5 Z=0
    g19: GeomPoint X=107.5 Y=-47.5 Z=0
    g20: GeomPoint X=27.5 Y=-42.5 Z=0
    g21: GeomPoint X=102.5 Y=-42.5 Z=0
  constraints (49):
    c: Equal(g4,g6)
    c: PointOnObject(g8,g1)
    c: PointOnObject(g8,g7)
    c: PointOnObject(g9,g3)
    c: PointOnObject(g9,g5)
    c: Tangent(g10,g11) = 1.5708
    c: Tangent(g11,g12) = 1.5708
    c: Tangent(g12,g13) = 1.5708
    c: Tangent(g13,g14) = 1.5708
    c: Tangent(g14,g15) = 1.5708
    c: Tangent(g15,g16) = 1.5708
    c: Tangent(g16,g17) = 1.5708
    c: Tangent(g17,g10) = 1.5708
    c: Horizontal(g11)
    c: Horizontal(g15)
    c: Vertical(g13)
    c: Vertical(g17)
    c: Equal(g10,g12)
    c: Equal(g12,g14)
    c: Equal(g14,g16)
    c: PointOnObject(g18,g11)
    c: PointOnObject(g18,g17)
    c: PointOnObject(g19,g13)
    c: PointOnObject(g19,g15)
    c: Equal(g10,g4)
    c: Horizontal(g1)
    c: Vertical(g3)
    c: Vertical(g7)
    c: Horizontal(g5)
    c: Tangent(g6,g7) = 1.5708
    c: Tangent(g3,g4) = 1.5708
    c: Tangent(g1,g2) = 1.5708
    c: Tangent(g0,g7) = 1.5708
    c: Tangent(g0,g1) = 1.5708
    c: Tangent(g3,g2) = 1.5708
    c: Tangent(g5,g4) = 1.5708
    c: Tangent(g5,g6) = 1.5708
    c: Equal(g6,g0)
    c: Equal(g0,g2)
    c: Radius(g0) = 2
    c: DistanceX(g0,g2) = 10
    c: DistanceY(g4,g1) = 10
    c: Symmetric(g6,g2,g20)
    c: Symmetric(g-4,g-3,g20)
    c: Equal(g3,g13)
    c: Symmetric(g16,g12,g21)
    c: Symmetric(g-5,g-6,g21)
    c: Equal(g13,g11)
    c: DistanceX(g6,g13) = 85
FEATURE [PartDesign::Pocket] Pocket007
  BaseFeature = -> Pad005
  Direction = (0,0,1)
  Length = 3
  Length2 = 5
  Profile = -> Sketch017
  ReferenceAxis = -> Sketch017 [N_Axis]
  Refine = true
  Type = 0
FEATURE [Sketcher::SketchObject] Sketch016
  ExternalGeometry = -> [Pad005]
  FullyConstrained = true
  MapMode = 5
  Placement = pos=(0,0,-2) rot=(0,0,1;0rad)
  Support = -> [Pocket007]
  sketch-geometry (2):
    g0: Circle CenterX=27.5 CenterY=42.5 CenterZ=0 NormalX=0 NormalY=0 NormalZ=1 AngleXU=0 Radius=2
    g1: Circle CenterX=102.5 CenterY=42.5 CenterZ=0 NormalX=0 NormalY=0 NormalZ=1 AngleXU=0 Radius=2
  constraints (4):
    c: Equal(g0,g1)
    c: Symmetric(g-5,g-6,g0)
    c: Symmetric(g-4,g-3,g1)
    c: Diameter(g0) = 4
FEATURE [PartDesign::Hole] Hole002
  BaseFeature = -> Pocket007
  CustomThreadClearance = 0
  Depth = 8
  DepthType = 0
  Diameter = 4.5
  DrillForDepth = false
  DrillPoint = 1
  DrillPointAngle = 118
  HoleCutCountersinkAngle = 90
  HoleCutCustomValues = false
  HoleCutDepth = 3.2
  HoleCutDiameter = 8
  HoleCutType = 6
  ModelThread = false
  Profile = -> Sketch016
  Refine = true
  Tapered = false
  TaperedAngle = 90
  ThreadClass = 0
  ThreadDepth = 8
  ThreadDepthType = 0
  ThreadDirection = 0
  ThreadFit = 0
  ThreadSize = 11
  ThreadType = 1
  Threaded = false
  UseCustomThreadClearance = false
FEATURE [Part::FeaturePython] Screw004  label="M4x8-Screw"  # Fasteners workbench fastener (typed FeaturePython)
  Placement = pos=(27.5,42.5,-5.2) rot=(0,0,1;0rad)
  baseObject = -> Body [Edge249]
  diameter = 5
  invert = false
  length = 1
  lengthCustom = 8
  matchOuter = true
  offset = 0
  thread = false
  type = 34
FEATURE [Part::FeaturePython] Screw005  label="M4x8-Screw001"  # Fasteners workbench fastener (typed FeaturePython)
  Placement = pos=(102.5,42.5,-5.2) rot=(0,0,1;0rad)
  baseObject = -> AdditivePipe [Edge274]
  diameter = 5
  invert = false
  length = 1
  lengthCustom = 8
  matchOuter = true
  offset = 0
  thread = false
  type = 34
FEATURE [PartDesign::Line] HoleAxis_5  label="HoleAxis_PG7"
  AttacherType = Attacher::AttachEngineLine
  Length = 8.37306
  MapMode = 19
  Placement = pos=(0,0,0) rot=(-0.707107,0,0.707107;3.14159rad)
  ResizeMode = 1
  Support = -> [Part__Feature087]
FEATURE [App::Part] PG7  label="PG012"
  Group = -> [Part__Feature087,Part__Feature088,Part__Feature089,Part__Feature090,Part__Feature091,HoleAxis_5]
  Origin = -> Origin017
  Placement = pos=(65.009,20.454,-3.304) rot=(0,-1,0;4.71239rad)
FEATURE [Sketcher::SketchObject] Sketch020  label="Stabilisierung - Pfad"
  ExternalGeometry = -> [Hole002]
  FullyConstrained = true
  MapMode = 5
  Placement = pos=(0,0,-7) rot=(0,0,1;0rad)
  Support = -> [Hole002]
  sketch-geometry (13):
    g0: LineSegment StartX=14.6316 StartY=70.3684 StartZ=0 EndX=10.7634 EndY=74.2366 EndZ=0
    g1: LineSegment StartX=15.0973 StartY=69.6369 StartZ=0 EndX=22.9672 EndY=47.9672 EndZ=0
    g2: LineSegment StartX=12.0711 StartY=72.9289 StartZ=0 EndX=14.8601 EndY=78.3333 EndZ=0
    g3: LineSegment StartX=12.0711 StartY=72.9289 StartZ=0 EndX=6.66667 EndY=70.1399 EndZ=0
    g4: ArcOfCircle CenterX=13.2174 CenterY=68.9542 CenterZ=0 NormalX=0 NormalY=0 NormalZ=1 AngleXU=0 Radius=2 StartAngle=0.348363 EndAngle=0.785398
    g5: GeomPoint X=14.9457 Y=70.0543 Z=0
    g6: LineSegment StartX=10.7634 StartY=74.2366 StartZ=0 EndX=22.9672 EndY=47.9672 EndZ=0
    g7: LineSegment StartX=21.5 StartY=46.5 StartZ=0 EndX=23.5 EndY=48.5 EndZ=0
    g8: LineSegment StartX=6.66667 StartY=70.1399 StartZ=0 EndX=14.8601 EndY=78.3333 EndZ=0
    g9: LineSegment StartX=22.7885 StartY=37.2115 StartZ=0 EndX=9.10088 EndY=12.4259 EndZ=0
    g10: LineSegment StartX=6.66667 StartY=14.8601 StartZ=0 EndX=14.8601 EndY=6.66667 EndZ=0
    g11: LineSegment StartX=22.7885 StartY=37.2115 StartZ=0 EndX=22.9672 EndY=47.9672 EndZ=0
    g12: LineSegment StartX=21.5 StartY=38.5 StartZ=0 EndX=23.5 EndY=36.5 EndZ=0
  constraints (32):
    c: Perpendicular(g-4,g1)
    c: Coincident(g2,g-3)
    c: Coincident(g3,g-3)
    c: Equal(g3,g2)
    c: PointOnObject(g5,g0)
    c: PointOnObject(g5,g1)
    c: Tangent(g0,g4) = -1.5708
    c: Tangent(g1,g4) = 1.5708
    c: Radius(g4) = 2
    c: PointOnObject(g4,g6)
    c: Coincident(g6,g1)
    c: Coincident(g8,g3)
    c: Coincident(g8,g2)
    c: Coincident(g6,g0)
    c: PointOnObject(g0,g8)
    c: Coincident(g2,g3)
    c: PointOnObject(g2,g0)
    c: PointOnObject(g2,g-3)
    c: Perpendicular(g0,g-3,g2) = 4.71239
    c: PointOnObject(g1,g7)
    c: Coincident(g7,g-4)
    c: Coincident(g7,g-4)
    c: Coincident(g10,g-5)
    c: Coincident(g10,g-5)
    c: PointOnObject(g9,g10)
    c: Perpendicular(g-5,g9)
    c: Coincident(g11,g9)
    c: Coincident(g11,g1)
    c: Perpendicular(g-6,g9)
    c: Coincident(g12,g-6)
    c: Coincident(g12,g-6)
    c: PointOnObject(g9,g12)
FEATURE [Sketcher::SketchObject] Sketch019  label="Stabilisierung - Profil"
  FullyConstrained = true
  MapMode = 7
  Placement = pos=(15.0973,69.6369,-7) rot=(-0.123474,0.701696,0.701696;3.3873rad)
  Support = -> [Sketch020]
  sketch-geometry (7):
    g0: LineSegment StartX=-1 StartY=0 StartZ=0 EndX=1 EndY=0 EndZ=0
    g1: ArcOfCircle CenterX=0 CenterY=0.522986 CenterZ=0 NormalX=0 NormalY=0 NormalZ=1 AngleXU=0 Radius=0.477014 StartAngle=0.261799 EndAngle=2.87979
    g2: ArcOfCircle CenterX=1 CenterY=0.477014 CenterZ=0 NormalX=0 NormalY=0 NormalZ=1 AngleXU=0 Radius=0.477014 StartAngle=3.40339 EndAngle=4.71239
    g3: LineSegment StartX=0.53924 StartY=0.353553 StartZ=0 EndX=0.46076 EndY=0.646447 EndZ=0
    g4: LineSegment StartX=-0.53924 StartY=0.353553 StartZ=0 EndX=-0.46076 EndY=0.646447 EndZ=0
    g5: ArcOfCircle CenterX=-1 CenterY=0.477014 CenterZ=0 NormalX=0 NormalY=0 NormalZ=1 AngleXU=0 Radius=0.477014 StartAngle=4.71239 EndAngle=6.02139
    g6: GeomPoint X=0 Y=1 Z=0
  constraints (16):
    c: PointOnObject(g0,g-1)
    c: Symmetric(g0,g0,g-1)
    c: PointOnObject(g1,g-2)
    c: Tangent(g3,g1) = -1.5708
    c: Tangent(g3,g2) = 1.5708
    c: Tangent(g2,g0) = -1.5708
    c: Tangent(g4,g5) = -1.5708
    c: Tangent(g1,g4) = 1.5708
    c: Equal(g4,g3)
    c: PointOnObject(g6,g-2)
    c: PointOnObject(g6,g1)
    c: DistanceY(g-1,g6) = 1
    c: DistanceX(g0,g0) = 2
    c: Tangent(g0,g5) = -1.5708
    c: Angle(g-2,g3) = 0.261799
    c: Equal(g1,g5)
FEATURE [PartDesign::AdditivePipe] AdditivePipe
  AuxilleryCurvelinear = true
  AuxillerySpineTangent = false
  BaseFeature = -> Hole002
  Binormal = (0,0,0)
  Mode = 0
  Profile = -> Sketch019
  Refine = true
  Spine = -> Sketch020
  SpineTangent = false
  Transformation = 0
  Transition = 0
FEATURE [PartDesign::Line] DatumLine
  AttacherType = Attacher::AttachEngineLine
  Length = 20
  MapMode = 43
  Placement = pos=(65,0,0) rot=(0,0.707107,0.707107;3.14159rad)
  ResizeMode = 0
  Support = -> [Pad003]
FEATURE [PartDesign::Plane] DatumPlane
  Length = 64.8324
  MapMode = 4
  Placement = pos=(65,0,0) rot=(0,-1,0;1.5708rad)
  ResizeMode = 0
  Support = -> [DatumLine]
  Width = 124.832
FEATURE [PartDesign::Mirrored] Mirrored
  BaseFeature = -> AdditivePipe
  MirrorPlane = -> DatumPlane
  Originals = -> [AdditivePipe]
  Overlap = 1
  Refine = true
FEATURE [Sketcher::SketchObject] Sketch021
  ExternalGeometry = -> [Mirrored,DatumPlane]
  FullyConstrained = true
  MapMode = 5
  Placement = pos=(0,0,-7) rot=(0,0,1;0rad)
  Support = -> [Mirrored]
  sketch-geometry (21):
    g0: LineSegment StartX=31.5 StartY=46.5 StartZ=0 EndX=51.0091 EndY=68.3317 EndZ=0
    g1: LineSegment StartX=54.7374 StartY=70 StartZ=0 EndX=75.2626 EndY=70 EndZ=0
    g2: LineSegment StartX=78.9909 StartY=68.3317 StartZ=0 EndX=98.5 EndY=46.5 EndZ=0
    g3: LineSegment StartX=98.5 StartY=46.5 StartZ=0 EndX=98.5 EndY=38.5 EndZ=0
    g4: LineSegment StartX=98.5 StartY=38.5 StartZ=0 EndX=77.5 EndY=20 EndZ=0
    g5: LineSegment StartX=77.5 StartY=20 StartZ=0 EndX=52.5 EndY=20 EndZ=0
    g6: LineSegment StartX=52.5 StartY=20 StartZ=0 EndX=31.5 EndY=38.5 EndZ=0
    g7: LineSegment StartX=31.5 StartY=38.5 StartZ=0 EndX=31.5 EndY=46.5 EndZ=0
    g8-g12: Circle x5 (B-spline internal-alignment scaffolding for g13; pole/knot coordinates omitted)
    g13: BSplineCurve PolesCount=5 KnotsCount=3 Degree=3 IsPeriodic=0
    g14: GeomPoint X=31.5 Y=38.5 Z=0
    g15: GeomPoint X=65 Y=32.5 Z=0
    g16: GeomPoint X=98.5 Y=38.5 Z=0
    g17: ArcOfCircle CenterX=54.7374 CenterY=65 CenterZ=0 NormalX=0 NormalY=0 NormalZ=1 AngleXU=0 Radius=5 StartAngle=1.5708 EndAngle=2.41232
    g18: GeomPoint X=52.5 Y=70 Z=0
    g19: ArcOfCircle CenterX=75.2626 CenterY=65 CenterZ=0 NormalX=0 NormalY=0 NormalZ=1 AngleXU=0 Radius=5 StartAngle=0.729277 EndAngle=1.5708
    g20: GeomPoint X=77.5 Y=70 Z=0
  constraints (41):
    c: Coincident(g6,g5)
    c: Coincident(g7,g0)
    c: Coincident(g2,g-5)
    c: Coincident(g3,g2)
    c: Coincident(g3,g4)
    c: Coincident(g6,g7)
    c: Coincident(g6,g-4)
    c: Coincident(g0,g-3)
    c: Coincident(g5,g4)
    c: Symmetric(g20,g18,g-6)
    c: Symmetric(g5,g4,g-6)
    c: Coincident(g13,g7)
    c: Weight(g8) = 1
    c: Equal(g8,g9)
    c: Coincident(g9,g5)
    c: Equal(g8,g10)
    c: Equal(g8,g11)
    c: Equal(g8,g12)
    c: Coincident(g13,g3)
    c: InternalAlignment(g8-g12 -> g13) x5
    c: InternalAlignment(g14,g13)
    c: InternalAlignment(g15,g13)
    c: InternalAlignment(g16,g13)
    c: PointOnObject(g10,g-6)
    c: PointOnObject(g-7,g5)
    c: DistanceX(g18,g20) = 25
    c: DistanceY(g-7,g10) = 25
    c: Coincident(g3,g-8)
    c: Coincident(g11,g4)
    c: DistanceY(g10,g20) = 25
    c: PointOnObject(g18,g0)
    c: PointOnObject(g18,g1)
    c: Tangent(g0,g17) = 1.5708
    c: Tangent(g1,g17) = 1.5708
    c: PointOnObject(g20,g1)
    c: PointOnObject(g20,g2)
    c: Tangent(g1,g19) = 1.5708
    c: Tangent(g2,g19) = 1.5708
    c: Equal(g19,g17)
    c: Radius(g17) = 5
    c: DistanceX(g5,g5) = 25
FEATURE [PartDesign::AdditiveBox] Box003
  AttacherType = Attacher::AttachEngine3D
  Height = 20
  Length = 130
  Width = 85
FEATURE [Sketcher::SketchObject] Sketch022
  ExternalGeometry = -> [Box003]
  FullyConstrained = true
  MapMode = 5
  Placement = pos=(0,0,0) rot=(1,0,0;3.14159rad)
  Support = -> [Box003]
  sketch-geometry (23):
    g0: LineSegment StartX=15.8322 StartY=-4 StartZ=0 EndX=114.168 EndY=-4 EndZ=0
    g1: LineSegment StartX=126 StartY=-15.8322 StartZ=0 EndX=126 EndY=-69.1678 EndZ=0
    g2: LineSegment StartX=114.168 StartY=-81 StartZ=0 EndX=15.8322 EndY=-81 EndZ=0
    g3: LineSegment StartX=4 StartY=-69.1678 StartZ=0 EndX=4 EndY=-15.8322 EndZ=0
    g4: GeomPoint X=4 Y=-4 Z=0
    g5: GeomPoint X=126 Y=-81 Z=0
    g6: GeomPoint X=65 Y=-42.5 Z=0
    g7: ArcOfCircle CenterX=4 CenterY=-81 CenterZ=0 NormalX=0 NormalY=0 NormalZ=1 AngleXU=0 Radius=10 StartAngle=0.167448 EndAngle=1.40335
    g8: ArcOfCircle CenterX=6 CenterY=-69.1678 CenterZ=0 NormalX=0 NormalY=0 NormalZ=1 AngleXU=0 Radius=2 StartAngle=3.14159 EndAngle=4.54494
    g9: ArcOfCircle CenterX=15.8322 CenterY=-79 CenterZ=0 NormalX=0 NormalY=0 NormalZ=1 AngleXU=0 Radius=2 StartAngle=3.30904 EndAngle=4.71239
    g10: ArcOfCircle CenterX=4 CenterY=-4 CenterZ=0 NormalX=0 NormalY=0 NormalZ=1 AngleXU=0 Radius=10 StartAngle=4.87984 EndAngle=6.11574
    g11: ArcOfCircle CenterX=126 CenterY=-4 CenterZ=0 NormalX=0 NormalY=0 NormalZ=1 AngleXU=0 Radius=10 StartAngle=3.30904 EndAngle=4.54494
    g12: ArcOfCircle CenterX=126 CenterY=-81 CenterZ=0 NormalX=0 NormalY=0 NormalZ=1 AngleXU=0 Radius=10 StartAngle=1.73824 EndAngle=2.97414
    g13: LineSegment StartX=4 StartY=-81 StartZ=0 EndX=126 EndY=-81 EndZ=0
    g14: LineSegment StartX=126 StartY=-81 StartZ=0 EndX=126 EndY=-4 EndZ=0
    g15: LineSegment StartX=126 StartY=-4 StartZ=0 EndX=4 EndY=-4 EndZ=0
    g16: LineSegment StartX=4 StartY=-4 StartZ=0 EndX=4 EndY=-81 EndZ=0
    g17: ArcOfCircle CenterX=6 CenterY=-15.8322 CenterZ=0 NormalX=0 NormalY=0 NormalZ=1 AngleXU=0 Radius=2 StartAngle=1.73824 EndAngle=3.14159
    g18: ArcOfCircle CenterX=124 CenterY=-15.8322 CenterZ=0 NormalX=0 NormalY=0 NormalZ=1 AngleXU=0 Radius=2 StartAngle=0 EndAngle=1.40335
    g19: ArcOfCircle CenterX=15.8322 CenterY=-6 CenterZ=0 NormalX=0 NormalY=0 NormalZ=1 AngleXU=0 Radius=2 StartAngle=1.5708 EndAngle=2.97414
    g20: ArcOfCircle CenterX=114.168 CenterY=-6 CenterZ=0 NormalX=0 NormalY=0 NormalZ=1 AngleXU=0 Radius=2 StartAngle=0.167448 EndAngle=1.5708
    g21: ArcOfCircle CenterX=124 CenterY=-69.1678 CenterZ=0 NormalX=0 NormalY=0 NormalZ=1 AngleXU=0 Radius=2 StartAngle=4.87984 EndAngle=6.28319
    g22: ArcOfCircle CenterX=114.168 CenterY=-79 CenterZ=0 NormalX=0 NormalY=0 NormalZ=1 AngleXU=0 Radius=2 StartAngle=4.71239 EndAngle=6.11574
  constraints (56):
    c: Horizontal(g0)
    c: Horizontal(g2)
    c: Vertical(g1)
    c: Vertical(g3)
    c: PointOnObject(g4,g0)
    c: PointOnObject(g4,g3)
    c: PointOnObject(g5,g1)
    c: PointOnObject(g5,g2)
    c: Symmetric(g-6,g-4,g6)
    c: Tangent(g7,g8) = 1.5708
    c: Tangent(g3,g8) = 1.5708
    c: Tangent(g2,g9) = 1.5708
    c: Tangent(g7,g9) = 1.5708
    c: Coincident(g12,g5)
    c: Coincident(g13,g14)
    c: Coincident(g14,g15)
    c: Coincident(g15,g16)
    c: Coincident(g16,g13)
    c: Horizontal(g13)
    c: Horizontal(g15)
    c: Vertical(g14)
    c: Vertical(g16)
    c: Coincident(g13,g7)
    c: Coincident(g14,g11)
    c: Coincident(g4,g10)
    c: Symmetric(g7,g11,g6)
    c: Tangent(g3,g17) = 1.5708
    c: Tangent(g10,g17) = 1.5708
    c: Tangent(g1,g18) = 1.5708
    c: Tangent(g11,g18) = 1.5708
    c: Tangent(g10,g19) = 1.5708
    c: Tangent(g0,g19) = 1.5708
    c: Tangent(g11,g20) = 1.5708
    c: Tangent(g0,g20) = 1.5708
    c: Tangent(g1,g21) = 1.5708
    c: Tangent(g12,g21) = 1.5708
    c: Tangent(g2,g22) = 1.5708
    c: Tangent(g12,g22) = 1.5708
    c: PointOnObject(g0,g15)
    c: PointOnObject(g3,g16)
    c: PointOnObject(g1,g14)
    c: DistanceX(g-6,g7) = 4
    c: DistanceY(g-6,g7) = 4
    c: PointOnObject(g2,g13)
    c: Equal(g7,g10)
    c: Equal(g10,g11)
    c: Equal(g11,g12)
    c: Radius(g7) = 10
    c: Equal(g9,g8)
    c: Equal(g8,g19)
    c: Equal(g19,g17)
    c: Equal(g17,g20)
    c: Equal(g20,g18)
    c: Equal(g18,g21)
    c: Equal(g21,g22)
    c: Radius(g9) = 2
FEATURE [PartDesign::Pocket] Pocket009
  BaseFeature = -> Box003
  Direction = (0,0,1)
  Length = 16
  Length2 = 100
  Profile = -> Sketch022
  ReferenceAxis = -> Sketch022 [N_Axis]
  Type = 0
  expr: Length = <<Box003>>.Height - 4mm
FEATURE [Sketcher::SketchObject] Sketch025
  ExternalGeometry = -> [Pocket009]
  FullyConstrained = true
  MapMode = 5
  Placement = pos=(0,0,16) rot=(1,0,0;3.14159rad)
  Support = -> [Pocket009]
  sketch-geometry (11):
    g0: LineSegment StartX=49 StartY=-19 StartZ=0 EndX=81 EndY=-19 EndZ=0
    g1: LineSegment StartX=81 StartY=-19 StartZ=0 EndX=81 EndY=-51 EndZ=0
    g2: LineSegment StartX=81 StartY=-51 StartZ=0 EndX=49 EndY=-51 EndZ=0
    g3: LineSegment StartX=49 StartY=-51 StartZ=0 EndX=49 EndY=-19 EndZ=0
    g4: GeomPoint X=65 Y=-4 Z=0
    g5: LineSegment StartX=65 StartY=-4 StartZ=0 EndX=65 EndY=-19 EndZ=0
    g6: LineSegment StartX=37.5 StartY=-61 StartZ=0 EndX=92.5 EndY=-61 EndZ=0
    g7: LineSegment StartX=92.5 StartY=-61 StartZ=0 EndX=92.5 EndY=-71 EndZ=0
    g8: LineSegment StartX=92.5 StartY=-71 StartZ=0 EndX=37.5 EndY=-71 EndZ=0
    g9: LineSegment StartX=37.5 StartY=-71 StartZ=0 EndX=37.5 EndY=-61 EndZ=0
    g10: LineSegment StartX=65 StartY=-19 StartZ=0 EndX=65 EndY=-61 EndZ=0
  constraints (29):
    c: Coincident(g0,g1)
    c: Coincident(g1,g2)
    c: Coincident(g2,g3)
    c: Coincident(g3,g0)
    c: Horizontal(g0)
    c: Horizontal(g2)
    c: Vertical(g1)
    c: Vertical(g3)
    c: Coincident(g5,g4)
    c: Vertical(g5)
    c: Symmetric(g0,g0,g5)
    c: DistanceY(g5,g5) = 15
    c: DistanceY(g1,g1) = 32
    c: Equal(g1,g0)
    c: Coincident(g6,g7)
    c: Coincident(g7,g8)
    c: Coincident(g8,g9)
    c: Coincident(g9,g6)
    c: Horizontal(g6)
    c: Horizontal(g8)
    c: Vertical(g7)
    c: Vertical(g9)
    c: DistanceX(g6,g6) = 55
    c: DistanceY(g7,g7) = 10
    c: Coincident(g10,g5)
    c: Vertical(g10)
    c: Symmetric(g6,g6,g10)
    c: DistanceY(g6,g1) = 10
    c: Symmetric(g-3,g-3,g4)
FEATURE [PartDesign::Pocket] Pocket010  label="Platz OLED und LED-Strip001"
  BaseFeature = -> Pocket009
  Direction = (0,0,1)
  Length = 3
  Length2 = 100
  Profile = -> Sketch025
  Type = 0
FEATURE [Sketcher::SketchObject] Sketch024
  ExternalGeometry = -> [Sketch025,Pocket010]
  FullyConstrained = true
  MapMode = 5
  Placement = pos=(0,0,16) rot=(1,0,0;3.14159rad)
  Support = -> [Pocket010]
  sketch-geometry (10):
    g0: LineSegment StartX=51.75 StartY=-29.5 StartZ=0 EndX=78.25 EndY=-29.5 EndZ=0
    g1: LineSegment StartX=78.25 StartY=-29.5 StartZ=0 EndX=78.25 EndY=-44.5 EndZ=0
    g2: LineSegment StartX=78.25 StartY=-44.5 StartZ=0 EndX=51.75 EndY=-44.5 EndZ=0
    g3: LineSegment StartX=51.75 StartY=-44.5 StartZ=0 EndX=51.75 EndY=-29.5 EndZ=0
    g4: LineSegment StartX=38 StartY=-62 StartZ=0 EndX=92 EndY=-62 EndZ=0
    g5: LineSegment StartX=92 StartY=-62 StartZ=0 EndX=92 EndY=-67 EndZ=0
    g6: LineSegment StartX=92 StartY=-67 StartZ=0 EndX=38 EndY=-67 EndZ=0
    g7: LineSegment StartX=38 StartY=-67 StartZ=0 EndX=38 EndY=-62 EndZ=0
    g8: LineSegment StartX=65 StartY=-62 StartZ=0 EndX=65 EndY=-61 EndZ=0
    g9: LineSegment StartX=65 StartY=-29.5 StartZ=0 EndX=65 EndY=-19 EndZ=0
  constraints (28):
    c: Coincident(g0,g1)
    c: Coincident(g1,g2)
    c: Coincident(g2,g3)
    c: Coincident(g3,g0)
    c: Horizontal(g0)
    c: Horizontal(g2)
    c: Vertical(g1)
    c: Vertical(g3)
    c: DistanceX(g0,g0) = 26.5
    c: DistanceY(g1,g1) = 15
    c: Coincident(g4,g5)
    c: Coincident(g5,g6)
    c: Coincident(g6,g7)
    c: Coincident(g7,g4)
    c: Horizontal(g4)
    c: Horizontal(g6)
    c: Vertical(g5)
    c: Vertical(g7)
    c: DistanceX(g4,g-3) = 0.5
    c: Vertical(g8)
    c: Symmetric(g4,g4,g8)
    c: Symmetric(g-3,g-4,g8)
    c: DistanceY(g5,g5) = 5
    c: DistanceY(g4,g-3) = 1
    c: Vertical(g9)
    c: Symmetric(g0,g0,g9)
    c: DistanceY(g9,g9) = 10.5
    c: Symmetric(g-5,g-5,g9)
FEATURE [PartDesign::Pocket] Pocket011  label="Sichtausschnitt001"
  BaseFeature = -> Pocket010
  Direction = (0,0,1)
  Length = 1.01
  Length2 = 100
  Profile = -> Sketch024
  ReferenceAxis = -> Sketch024 [N_Axis]
  Type = 1
FEATURE [Sketcher::SketchObject] Sketch026  label="Sketch Halter OLED001"
  ExternalGeometry = -> [Sketch025]
  FullyConstrained = true
  MapMode = 5
  Placement = pos=(0,0,19) rot=(1,0,0;3.14159rad)
  Support = -> [Pocket011]
  sketch-geometry (9):
    g0: Circle CenterX=53.1 CenterY=-23.35 CenterZ=0 NormalX=0 NormalY=0 NormalZ=1 AngleXU=0 Radius=1
    g1: Circle CenterX=76.9 CenterY=-23.35 CenterZ=0 NormalX=0 NormalY=0 NormalZ=1 AngleXU=0 Radius=1
    g2: Circle CenterX=76.9 CenterY=-46.65 CenterZ=0 NormalX=0 NormalY=0 NormalZ=1 AngleXU=0 Radius=1
    g3: Circle CenterX=53.1 CenterY=-46.65 CenterZ=0 NormalX=0 NormalY=0 NormalZ=1 AngleXU=0 Radius=1
    g4: LineSegment StartX=53.1 StartY=-23.35 StartZ=0 EndX=76.9 EndY=-23.35 EndZ=0
    g5: LineSegment StartX=76.9 StartY=-23.35 StartZ=0 EndX=76.9 EndY=-46.65 EndZ=0
    g6: LineSegment StartX=76.9 StartY=-46.65 StartZ=0 EndX=53.1 EndY=-46.65 EndZ=0
    g7: LineSegment StartX=53.1 StartY=-46.65 StartZ=0 EndX=53.1 EndY=-23.35 EndZ=0
    g8: GeomPoint X=65 Y=-35 Z=0
  constraints (20):
    c: Coincident(g4,g5)
    c: Coincident(g5,g6)
    c: Coincident(g6,g7)
    c: Coincident(g7,g4)
    c: Horizontal(g4)
    c: Horizontal(g6)
    c: Vertical(g5)
    c: Vertical(g7)
    c: Coincident(g4,g0)
    c: Coincident(g5,g2)
    c: Coincident(g1,g4)
    c: Coincident(g3,g6)
    c: Equal(g0,g1)
    c: Equal(g1,g2)
    c: Equal(g2,g3)
    c: Diameter(g1) = 2
    c: DistanceX(g4,g4) = 23.8
    c: DistanceY(g5,g5) = 23.3
    c: Symmetric(g-4,g-6,g8)
    c: Symmetric(g3,g1,g8)
FEATURE [PartDesign::Pad] Pad006  label="Halter OLED001"
  BaseFeature = -> Pocket011
  Direction = (0,0,-1)
  Length = 5
  Length2 = 100
  Profile = -> Sketch026
  ReferenceAxis = -> Sketch026 [N_Axis]
  Type = 0
FEATURE [Sketcher::SketchObject] Sketch023
  ExternalGeometry = -> [Sketch025]
  FullyConstrained = true
  MapMode = 5
  Placement = pos=(0,0,16) rot=(1,0,0;3.14159rad)
  Support = -> [Pad006]
  sketch-geometry (26):
    g0: LineSegment StartX=50 StartY=-11 StartZ=0 EndX=80 EndY=-11 EndZ=0
    g1: LineSegment StartX=80 StartY=-11 StartZ=0 EndX=80 EndY=-18 EndZ=0
    g2: LineSegment StartX=80 StartY=-18 StartZ=0 EndX=50 EndY=-18 EndZ=0
    g3: LineSegment StartX=50 StartY=-18 StartZ=0 EndX=50 EndY=-11 EndZ=0
    g4: LineSegment StartX=82 StartY=-20 StartZ=0 EndX=89 EndY=-20 EndZ=0
    g5: LineSegment StartX=89 StartY=-20 StartZ=0 EndX=89 EndY=-50 EndZ=0
    g6: LineSegment StartX=89 StartY=-50 StartZ=0 EndX=82 EndY=-50 EndZ=0
    g7: LineSegment StartX=82 StartY=-50 StartZ=0 EndX=82 EndY=-20 EndZ=0
    g8: LineSegment StartX=41 StartY=-20 StartZ=0 EndX=48 EndY=-20 EndZ=0
    g9: LineSegment StartX=48 StartY=-20 StartZ=0 EndX=48 EndY=-50 EndZ=0
    g10: LineSegment StartX=48 StartY=-50 StartZ=0 EndX=41 EndY=-50 EndZ=0
    g11: LineSegment StartX=41 StartY=-50 StartZ=0 EndX=41 EndY=-20 EndZ=0
    g12: LineSegment StartX=50 StartY=-52 StartZ=0 EndX=80 EndY=-52 EndZ=0
    g13: LineSegment StartX=80 StartY=-52 StartZ=0 EndX=80 EndY=-59 EndZ=0
    g14: LineSegment StartX=80 StartY=-59 StartZ=0 EndX=50 EndY=-59 EndZ=0
    g15: LineSegment StartX=50 StartY=-59 StartZ=0 EndX=50 EndY=-52 EndZ=0
    g16: LineSegment StartX=48 StartY=-18 StartZ=0 EndX=82 EndY=-18 EndZ=0
    g17: LineSegment StartX=82 StartY=-18 StartZ=0 EndX=82 EndY=-52 EndZ=0
    g18: LineSegment StartX=82 StartY=-52 StartZ=0 EndX=48 EndY=-52 EndZ=0
    g19: LineSegment StartX=48 StartY=-52 StartZ=0 EndX=48 EndY=-18 EndZ=0
    g20: GeomPoint X=65 Y=-35 Z=0
    g21: GeomPoint X=48 Y=-35 Z=0
    g22: GeomPoint X=116 Y=-18 Z=0
    g23: GeomPoint X=82 Y=-35 Z=0
    g24: GeomPoint X=65 Y=-52 Z=0
    g25: GeomPoint X=65 Y=-18 Z=0
  constraints (61):
    c: Coincident(g0,g1)
    c: Coincident(g1,g2)
    c: Coincident(g2,g3)
    c: Coincident(g3,g0)
    c: Horizontal(g0)
    c: Horizontal(g2)
    c: Vertical(g1)
    c: Vertical(g3)
    c: Coincident(g4,g5)
    c: Coincident(g5,g6)
    c: Coincident(g6,g7)
    c: Coincident(g7,g4)
    c: Horizontal(g4)
    c: Horizontal(g6)
    c: Vertical(g5)
    c: Vertical(g7)
    c: Coincident(g8,g9)
    c: Coincident(g9,g10)
    c: Coincident(g10,g11)
    c: Coincident(g11,g8)
    c: Horizontal(g8)
    c: Horizontal(g10)
    c: Vertical(g9)
    c: Vertical(g11)
    c: Coincident(g12,g13)
    c: Coincident(g13,g14)
    c: Coincident(g14,g15)
    c: Coincident(g15,g12)
    c: Horizontal(g12)
    c: Horizontal(g14)
    c: Vertical(g13)
    c: Vertical(g15)
    c: Equal(g4,g1)
    c: Equal(g1,g8)
    c: Equal(g8,g13)
    c: Coincident(g16,g17)
    c: Coincident(g17,g18)
    c: Coincident(g18,g19)
    c: Coincident(g19,g16)
    c: DistanceX(g-4,g16) = 1
    c: DistanceY(g-4,g16) = 1
    c: Symmetric(g16,g18,g20)
    c: Symmetric(g-6,g-4,g20)
    c: DistanceY(g15,g15) = 7
    c: Vertical(g19)
    c: Horizontal(g16)
    c: PointOnObject(g12,g18)
    c: Vertical(g17)
    c: Equal(g0,g11)
    c: Equal(g11,g5)
    c: Equal(g5,g14)
    c: DistanceY(g11,g11) = 30
    c: Symmetric(g18,g17,g24)
    c: Symmetric(g6,g4,g23)
    c: Symmetric(g16,g22,g16)
    c: Symmetric(g16,g18,g21)
    c: Symmetric(g8,g9,g21)
    c: Symmetric(g17,g16,g23)
    c: Symmetric(g12,g12,g24)
    c: Symmetric(g2,g1,g25)
    c: Symmetric(g16,g16,g25)
FEATURE [PartDesign::Pocket] Pocket008  label="Ausschnitte  Touch001"
  BaseFeature = -> Pad006
  Direction = (0,0,1)
  Length = 3.5
  Length2 = 100
  Profile = -> Sketch023
  Type = 0
FEATURE [Sketcher::SketchObject] Sketch027
  ExternalGeometry = -> [Pocket008,Sketch024]
  FullyConstrained = true
  MapMode = 5
  Placement = pos=(0,0,19) rot=(1,0,0;3.14159rad)
  Support = -> [Pocket008]
  sketch-geometry (5):
    g0: Circle CenterX=51.5 CenterY=-69 CenterZ=0 NormalX=0 NormalY=0 NormalZ=1 AngleXU=0 Radius=1.35
    g1: Circle CenterX=78.5 CenterY=-69 CenterZ=0 NormalX=0 NormalY=0 NormalZ=1 AngleXU=0 Radius=1.35
    g2: LineSegment StartX=51.5 StartY=-69 StartZ=0 EndX=78.5 EndY=-69 EndZ=0
    g3: LineSegment StartX=65 StartY=-71 StartZ=0 EndX=65 EndY=-67 EndZ=0
    g4: GeomPoint X=65 Y=-69 Z=0
  constraints (11):
    c: Coincident(g2,g0)
    c: Coincident(g2,g1)
    c: Horizontal(g2)
    c: Equal(g1,g0)
    c: Diameter(g0) = 2.7
    c: DistanceX(g2,g2) = 27
    c: Vertical(g3)
    c: Symmetric(g0,g1,g4)
    c: Symmetric(g3,g3,g4)
    c: Symmetric(g-5,g-5,g3)
    c: PointOnObject(g3,g-6)
FEATURE [PartDesign::Pad] Pad007  label="Halter LED Strip001"
  BaseFeature = -> Pocket008
  Direction = (0,0,-1)
  Length = 5
  Length2 = 10
  Profile = -> Sketch027
  ReferenceAxis = -> Sketch027 [N_Axis]
  Type = 0
FEATURE [PartDesign::Fillet] Fillet001
  Base = -> Pad007 [Edge3,Edge19,Edge1,Edge6]
  BaseFeature = -> Pad007
  Radius = 7.5
  SupportTransform = false
FEATURE [Sketcher::SketchObject] Sketch028
  ExternalGeometry = -> [Fillet001]
  FullyConstrained = true
  MapMode = 5
  Placement = pos=(0,0,0) rot=(1,0,0;3.14159rad)
  Support = -> [Fillet001]
  sketch-geometry (17):
    g0: LineSegment StartX=6.65146 StartY=-6.65148 StartZ=0 EndX=123.349 EndY=-6.65148 EndZ=0
    g1: LineSegment StartX=123.349 StartY=-6.65148 StartZ=0 EndX=123.349 EndY=-78.3485 EndZ=0
    g2: LineSegment StartX=123.349 StartY=-78.3485 StartZ=0 EndX=6.65146 EndY=-78.3485 EndZ=0
    g3: LineSegment StartX=6.65146 StartY=-78.3485 StartZ=0 EndX=6.65146 EndY=-6.65148 EndZ=0
    g4: GeomPoint X=65 Y=-42.5 Z=0
    g5: Circle CenterX=123.349 CenterY=-6.65148 CenterZ=0 NormalX=0 NormalY=0 NormalZ=1 AngleXU=0 Radius=2.8
    g6: Circle CenterX=123.349 CenterY=-78.3485 CenterZ=0 NormalX=0 NormalY=0 NormalZ=1 AngleXU=0 Radius=2.8
    g7: Circle CenterX=6.65146 CenterY=-78.3485 CenterZ=0 NormalX=0 NormalY=0 NormalZ=1 AngleXU=0 Radius=2.8
    g8: Circle CenterX=6.65146 CenterY=-6.65148 CenterZ=0 NormalX=0 NormalY=0 NormalZ=1 AngleXU=0 Radius=2.8
    g9: LineSegment StartX=3.85146 StartY=-5.49168 StartZ=0 EndX=3.85146 EndY=-6.65148 EndZ=0
    g10: LineSegment StartX=3.85146 StartY=-5.49168 StartZ=0 EndX=9.34315 EndY=0 EndZ=0
    g11: LineSegment StartX=0 StartY=-4.3934 StartZ=0 EndX=4.3934 EndY=0 EndZ=0
    g12: LineSegment StartX=4.67157 StartY=-4.67157 StartZ=0 EndX=2.1967 EndY=-2.1967 EndZ=0
    g13: GeomPoint X=4.67157 Y=-4.67157 Z=0
    g14: GeomPoint X=2.1967 Y=-2.1967 Z=0
    g15: LineSegment StartX=11.0711 StartY=-11.0711 StartZ=0 EndX=22.1421 EndY=0 EndZ=0
    g16: LineSegment StartX=8.63137 StartY=-8.63137 StartZ=0 EndX=17.2627 EndY=0 EndZ=0
  constraints (45):
    c: Coincident(g0,g1)
    c: Coincident(g1,g2)
    c: Coincident(g2,g3)
    c: Coincident(g3,g0)
    c: Horizontal(g0)
    c: Horizontal(g2)
    c: Vertical(g1)
    c: Vertical(g3)
    c: Symmetric(g-3,g-4,g4)
    c: Symmetric(g2,g0,g4)
    c: Coincident(g5,g0)
    c: Coincident(g6,g1)
    c: Coincident(g7,g2)
    c: Diameter(g7) = 5.6
    c: Coincident(g8,g0)
    c: Equal(g5,g6)
    c: Equal(g6,g7)
    c: Equal(g7,g8)
    c: Vertical(g9)
    c: DistanceX(g-4,g9) = 3.85146
    c: Coincident(g10,g9)
    c: PointOnObject(g11,g-1)
    c: Parallel(g10,g11)
    c: Tangent(g-5,g11)
    c: Angle(g9,g10) = 2.35619
    c: PointOnObject(g11,g-2)
    c: Tangent(g10,g8)
    c: PointOnObject(g12,g10)
    c: PointOnObject(g12,g11)
    c: Perpendicular(g10,g12)
    c: Distance(g12) = 3.5
    c: PointOnObject(g10,g-1)
    c: PointOnObject(g13,g8)
    c: Coincident(g13,g12)
    c: PointOnObject(g14,g-5)
    c: Coincident(g12,g14)
    c: Tangent(g9,g8) = -1.5708
    c: PointOnObject(g15,g-1)
    c: Parallel(g15,g10)
    c: PointOnObject(g16,g8)
    c: PointOnObject(g16,g-1)
    c: Tangent(g16,g8)
    c: Parallel(g15,g16)
    c: Distance(g16,g15) = 3.45025
    c: Tangent(g15,g-6) = -1.5708
FEATURE [PartDesign::Pocket] Pocket013
  BaseFeature = -> Fillet001
  Direction = (0,0,1)
  Length = 10
  Length2 = 5
  Profile = -> Sketch028
  ReferenceAxis = -> Sketch028 [N_Axis]
  Type = 0
FEATURE [PartDesign::ShapeBinder] ShapeBinder001
  Support = -> [Pocket013]
  TraceSupport = true
FEATURE [Sketcher::SketchObject] Sketch029
  ExternalGeometry = -> [ShapeBinder001]
  FullyConstrained = true
  MapMode = 5
  Placement = pos=(0,0,0) rot=(1,0,0;3.14159rad)
  Support = -> [ShapeBinder001]
  sketch-geometry (23):
    g0: GeomPoint X=5 Y=-5 Z=0
    g1: GeomPoint X=125 Y=-80 Z=0
    g2: GeomPoint X=65 Y=-42.5 Z=0
    g3: ArcOfCircle CenterX=5 CenterY=-80 CenterZ=0 NormalX=0 NormalY=0 NormalZ=1 AngleXU=0 Radius=10 StartAngle=0.167448 EndAngle=1.40335
    g4: ArcOfCircle CenterX=7 CenterY=-68.1678 CenterZ=0 NormalX=0 NormalY=0 NormalZ=1 AngleXU=0 Radius=2 StartAngle=3.14159 EndAngle=4.54494
    g5: ArcOfCircle CenterX=5 CenterY=-5 CenterZ=0 NormalX=0 NormalY=0 NormalZ=1 AngleXU=0 Radius=10 StartAngle=4.87984 EndAngle=6.11574
    g6: ArcOfCircle CenterX=125 CenterY=-5 CenterZ=0 NormalX=0 NormalY=0 NormalZ=1 AngleXU=0 Radius=10 StartAngle=3.30904 EndAngle=4.54494
    g7: ArcOfCircle CenterX=125 CenterY=-80 CenterZ=0 NormalX=0 NormalY=0 NormalZ=1 AngleXU=0 Radius=10 StartAngle=1.73824 EndAngle=2.97414
    g8: LineSegment StartX=5 StartY=-80 StartZ=0 EndX=125 EndY=-80 EndZ=0
    g9: LineSegment StartX=125 StartY=-80 StartZ=0 EndX=125 EndY=-5 EndZ=0
    g10: LineSegment StartX=5 StartY=-5 StartZ=0 EndX=5 EndY=-80 EndZ=0
    g11: ArcOfCircle CenterX=7 CenterY=-16.8322 CenterZ=0 NormalX=0 NormalY=0 NormalZ=1 AngleXU=0 Radius=2 StartAngle=1.73824 EndAngle=3.14159
    g12: ArcOfCircle CenterX=123 CenterY=-16.8322 CenterZ=0 NormalX=0 NormalY=0 NormalZ=1 AngleXU=0 Radius=2 StartAngle=9e-16 EndAngle=1.40335
    g13: ArcOfCircle CenterX=16.8322 CenterY=-7 CenterZ=0 NormalX=0 NormalY=0 NormalZ=1 AngleXU=0 Radius=2 StartAngle=1.5708 EndAngle=2.97414
    g14: ArcOfCircle CenterX=113.168 CenterY=-7 CenterZ=0 NormalX=0 NormalY=0 NormalZ=1 AngleXU=0 Radius=2 StartAngle=0.167448 EndAngle=1.5708
    g15: ArcOfCircle CenterX=123 CenterY=-68.1678 CenterZ=0 NormalX=0 NormalY=0 NormalZ=1 AngleXU=0 Radius=2 StartAngle=4.87984 EndAngle=6.28319
    g16: ArcOfCircle CenterX=113.168 CenterY=-78 CenterZ=0 NormalX=0 NormalY=0 NormalZ=1 AngleXU=0 Radius=2 StartAngle=4.71239 EndAngle=6.11574
    g17: ArcOfCircle CenterX=16.8322 CenterY=-78 CenterZ=0 NormalX=0 NormalY=0 NormalZ=1 AngleXU=0 Radius=2 StartAngle=3.30904 EndAngle=4.71239
    g18: LineSegment StartX=5 StartY=-5 StartZ=0 EndX=125 EndY=-5 EndZ=0
    g19: LineSegment StartX=5 StartY=-16.8322 StartZ=0 EndX=5 EndY=-68.1678 EndZ=0
    g20: LineSegment StartX=125 StartY=-68.1678 StartZ=0 EndX=125 EndY=-16.8322 EndZ=0
    g21: LineSegment StartX=113.168 StartY=-5 StartZ=0 EndX=16.8322 EndY=-5 EndZ=0
    g22: LineSegment StartX=16.8322 StartY=-80 StartZ=0 EndX=113.168 EndY=-80 EndZ=0
  constraints (54):
    c: Tangent(g3,g4) = 1.5708
    c: Coincident(g7,g1)
    c: Coincident(g8,g9)
    c: Coincident(g10,g8)
    c: Horizontal(g8)
    c: Vertical(g9)
    c: Vertical(g10)
    c: Coincident(g8,g3)
    c: Coincident(g9,g6)
    c: Coincident(g0,g5)
    c: Symmetric(g3,g6,g2)
    c: Tangent(g5,g11) = 1.5708
    c: Tangent(g6,g12) = 1.5708
    c: Tangent(g5,g13) = 1.5708
    c: Tangent(g6,g14) = 1.5708
    c: Tangent(g7,g15) = 1.5708
    c: Tangent(g7,g16) = 1.5708
    c: Equal(g3,g5)
    c: Equal(g5,g6)
    c: Equal(g6,g7)
    c: Radius(g3) = 10
    c: Equal(g4,g13)
    c: Equal(g13,g11)
    c: Equal(g11,g14)
    c: Equal(g12,g15)
    c: Tangent(g16,g8) = -1.5708
    c: Tangent(g4,g10) = -1.5708
    c: Coincident(g8,g7)
    c: Tangent(g17,g8) = -1.5708
    c: Tangent(g17,g3) = 1.5708
    c: Radius(g17) = 2
    c: Tangent(g12,g9) = -1.5708
    c: Tangent(g15,g9) = -1.5708
    c: Tangent(g11,g10) = -1.5708
    c: Coincident(g18,g5)
    c: Horizontal(g18)
    c: Coincident(g18,g6)
    c: Coincident(g10,g5)
    c: Tangent(g13,g18) = 1.5708
    c: Tangent(g14,g18) = 1.5708
    c: Equal(g11,g12)
    c: Equal(g14,g17)
    c: Equal(g17,g16)
    c: Symmetric(g-3,g-5,g2)
    c: Coincident(g19,g11)
    c: Coincident(g19,g4)
    c: Coincident(g20,g15)
    c: Coincident(g20,g12)
    c: Coincident(g21,g14)
    c: Coincident(g21,g13)
    c: DistanceY(g5,g-4) = 1
    c: DistanceX(g-5,g11) = 1
    c: Coincident(g22,g17)
    c: Coincident(g22,g16)
FEATURE [Sketcher::SketchObject] Sketch030
  ExternalGeometry = -> [ShapeBinder001]
  FullyConstrained = true
  MapMode = 5
  Placement = pos=(0,0,0) rot=(1,0,0;3.14159rad)
  Support = -> [ShapeBinder001]
  sketch-geometry (12):
    g0: LineSegment StartX=7.5 StartY=0 StartZ=0 EndX=122.5 EndY=0 EndZ=0
    g1: LineSegment StartX=130 StartY=-7.5 StartZ=0 EndX=130 EndY=-77.5 EndZ=0
    g2: LineSegment StartX=122.5 StartY=-85 StartZ=0 EndX=7.5 EndY=-85 EndZ=0
    g3: LineSegment StartX=0 StartY=-77.5 StartZ=0 EndX=0 EndY=-7.5 EndZ=0
    g4: ArcOfCircle CenterX=7.5 CenterY=-7.5 CenterZ=0 NormalX=0 NormalY=0 NormalZ=1 AngleXU=0 Radius=7.5 StartAngle=1.5708 EndAngle=3.14159
    g5: GeomPoint X=0 Y=0 Z=0
    g6: ArcOfCircle CenterX=122.5 CenterY=-7.5 CenterZ=0 NormalX=0 NormalY=0 NormalZ=1 AngleXU=0 Radius=7.5 StartAngle=0 EndAngle=1.5708
    g7: GeomPoint X=130 Y=0 Z=0
    g8: ArcOfCircle CenterX=122.5 CenterY=-77.5 CenterZ=0 NormalX=0 NormalY=0 NormalZ=1 AngleXU=0 Radius=7.5 StartAngle=4.71239 EndAngle=6.28319
    g9: GeomPoint X=130 Y=-85 Z=0
    g10: ArcOfCircle CenterX=7.5 CenterY=-77.5 CenterZ=0 NormalX=0 NormalY=0 NormalZ=1 AngleXU=0 Radius=7.5 StartAngle=3.14159 EndAngle=4.71239
    g11: GeomPoint X=0 Y=-85 Z=0
  constraints (23):
    c: Horizontal(g0)
    c: Vertical(g1)
    c: Vertical(g3)
    c: Coincident(g5,g-1)
    c: PointOnObject(g5,g3)
    c: Tangent(g0,g4) = 1.5708
    c: Tangent(g3,g4) = 1.5708
    c: PointOnObject(g7,g1)
    c: PointOnObject(g7,g0)
    c: Tangent(g1,g6) = 1.5708
    c: Tangent(g0,g6) = 1.5708
    c: PointOnObject(g9,g1)
    c: PointOnObject(g9,g2)
    c: Tangent(g1,g8) = 1.5708
    c: Tangent(g2,g8) = 1.5708
    c: PointOnObject(g11,g2)
    c: PointOnObject(g11,g3)
    c: Tangent(g2,g10) = 1.5708
    c: Tangent(g3,g10) = 1.5708
    c: Coincident(g2,g-4)
    c: Coincident(g2,g-4)
    c: Coincident(g-3,g1)
    c: Coincident(g0,g-5)
FEATURE [PartDesign::Pad] Pad008
  Direction = (0,0,-1)
  Length = 10
  Length2 = 10
  Profile = -> Sketch030
  ReferenceAxis = -> Sketch030 [N_Axis]
  Type = 0
FEATURE [PartDesign::Pocket] Pocket014
  BaseFeature = -> Pad008
  Direction = (0,0,1)
  Length = 7
  Length2 = 5
  Profile = -> Sketch029
  ReferenceAxis = -> Sketch029 [N_Axis]
  Reversed = true
  Type = 0
FEATURE [Sketcher::SketchObject] Sketch031
  ExternalGeometry = -> [ShapeBinder001]
  FullyConstrained = true
  MapMode = 5
  Placement = pos=(0,0,-10) rot=(1,0,0;3.14159rad)
  Support = -> [Pocket014]
  sketch-geometry (4):
    g0: Circle CenterX=6.65146 CenterY=-6.65148 CenterZ=0 NormalX=0 NormalY=0 NormalZ=1 AngleXU=0 Radius=2.8
    g1: Circle CenterX=123.349 CenterY=-6.65148 CenterZ=0 NormalX=0 NormalY=0 NormalZ=1 AngleXU=0 Radius=2.8
    g2: Circle CenterX=123.349 CenterY=-78.3485 CenterZ=0 NormalX=0 NormalY=0 NormalZ=1 AngleXU=0 Radius=2.8
    g3: Circle CenterX=6.65146 CenterY=-78.3485 CenterZ=0 NormalX=0 NormalY=0 NormalZ=1 AngleXU=0 Radius=2.8
  constraints (8):
    c: Coincident(g1,g-4)
    c: Coincident(g2,g-5)
    c: Coincident(g3,g-6)
    c: Coincident(g0,g-3)
    c: Equal(g0,g-3)
    c: Equal(g0,g1)
    c: Equal(g1,g2)
    c: Equal(g2,g3)
FEATURE [PartDesign::Hole] Hole003
  BaseFeature = -> Pocket014
  CustomThreadClearance = 0
  Depth = 314.401
  DepthType = 1
  Diameter = 4.5
  DrillForDepth = false
  DrillPoint = 1
  DrillPointAngle = 118
  HoleCutCountersinkAngle = 90
  HoleCutCustomValues = false
  HoleCutDepth = 5.2
  HoleCutDiameter = 10
  HoleCutType = 12
  ModelThread = false
  Profile = -> Sketch031
  Tapered = false
  TaperedAngle = 90
  ThreadClass = 0
  ThreadDepth = 314.401
  ThreadDepthType = 0
  ThreadDirection = 0
  ThreadFit = 0
  ThreadSize = 11
  ThreadType = 1
  Threaded = false
  UseCustomThreadClearance = false
FEATURE [Sketcher::SketchObject] Sketch032
  ExternalGeometry = -> [ShapeBinder001]
  FullyConstrained = true
  MapMode = 5
  Placement = pos=(0,0,0) rot=(1,0,0;3.14159rad)
  Support = -> [ShapeBinder001]
  sketch-geometry (46):
    g0: GeomPoint X=5 Y=-5 Z=0
    g1: GeomPoint X=125 Y=-80 Z=0
    g2: GeomPoint X=65 Y=-42.5 Z=0
    g3: ArcOfCircle CenterX=5 CenterY=-80 CenterZ=0 NormalX=0 NormalY=0 NormalZ=1 AngleXU=0 Radius=10 StartAngle=0.167448 EndAngle=1.40335
    g4: ArcOfCircle CenterX=7 CenterY=-68.1678 CenterZ=0 NormalX=0 NormalY=0 NormalZ=1 AngleXU=0 Radius=2 StartAngle=3.14159 EndAngle=4.54494
    g5: ArcOfCircle CenterX=5 CenterY=-5 CenterZ=0 NormalX=0 NormalY=0 NormalZ=1 AngleXU=0 Radius=10 StartAngle=4.87984 EndAngle=6.11574
    g6: ArcOfCircle CenterX=125 CenterY=-5 CenterZ=0 NormalX=0 NormalY=0 NormalZ=1 AngleXU=0 Radius=10 StartAngle=3.30904 EndAngle=4.54494
    g7: ArcOfCircle CenterX=125 CenterY=-80 CenterZ=0 NormalX=0 NormalY=0 NormalZ=1 AngleXU=0 Radius=10 StartAngle=1.73824 EndAngle=2.97414
    g8: LineSegment StartX=5 StartY=-80 StartZ=0 EndX=125 EndY=-80 EndZ=0
    g9: LineSegment StartX=125 StartY=-80 StartZ=0 EndX=125 EndY=-5 EndZ=0
    g10: LineSegment StartX=5 StartY=-5 StartZ=0 EndX=5 EndY=-80 EndZ=0
    g11: ArcOfCircle CenterX=7 CenterY=-16.8322 CenterZ=0 NormalX=0 NormalY=0 NormalZ=1 AngleXU=0 Radius=2 StartAngle=1.73824 EndAngle=3.14159
    g12: ArcOfCircle CenterX=123 CenterY=-16.8322 CenterZ=0 NormalX=0 NormalY=0 NormalZ=1 AngleXU=0 Radius=2 StartAngle=-9e-16 EndAngle=1.40335
    g13: ArcOfCircle CenterX=16.8322 CenterY=-7 CenterZ=0 NormalX=0 NormalY=0 NormalZ=1 AngleXU=0 Radius=2 StartAngle=1.5708 EndAngle=2.97414
    g14: ArcOfCircle CenterX=113.168 CenterY=-7 CenterZ=0 NormalX=0 NormalY=0 NormalZ=1 AngleXU=0 Radius=2 StartAngle=0.167448 EndAngle=1.5708
    g15: ArcOfCircle CenterX=123 CenterY=-68.1678 CenterZ=0 NormalX=0 NormalY=0 NormalZ=1 AngleXU=0 Radius=2 StartAngle=4.87984 EndAngle=6.28319
    g16: ArcOfCircle CenterX=113.168 CenterY=-78 CenterZ=0 NormalX=0 NormalY=0 NormalZ=1 AngleXU=0 Radius=2 StartAngle=4.71239 EndAngle=6.11574
    g17: ArcOfCircle CenterX=16.8322 CenterY=-78 CenterZ=0 NormalX=0 NormalY=0 NormalZ=1 AngleXU=0 Radius=2 StartAngle=3.30904 EndAngle=4.71239
    g18: LineSegment StartX=5 StartY=-5 StartZ=0 EndX=125 EndY=-5 EndZ=0
    g19: LineSegment StartX=5 StartY=-16.8322 StartZ=0 EndX=5 EndY=-68.1678 EndZ=0
    g20: LineSegment StartX=125 StartY=-68.1678 StartZ=0 EndX=125 EndY=-16.8322 EndZ=0
    g21: LineSegment StartX=113.168 StartY=-5 StartZ=0 EndX=16.8322 EndY=-5 EndZ=0
    g22: LineSegment StartX=16.8322 StartY=-80 StartZ=0 EndX=113.168 EndY=-80 EndZ=0
    g23: GeomPoint X=4 Y=-4 Z=0
    g24: GeomPoint X=126 Y=-81 Z=0
    g25: GeomPoint X=65 Y=-42.5 Z=0
    g26: ArcOfCircle CenterX=4 CenterY=-81 CenterZ=0 NormalX=0 NormalY=0 NormalZ=1 AngleXU=0 Radius=10 StartAngle=0.167448 EndAngle=1.40335
    g27: ArcOfCircle CenterX=6 CenterY=-69.1678 CenterZ=0 NormalX=0 NormalY=0 NormalZ=1 AngleXU=0 Radius=2 StartAngle=3.14159 EndAngle=4.54494
    g28: ArcOfCircle CenterX=4 CenterY=-4 CenterZ=0 NormalX=0 NormalY=0 NormalZ=1 AngleXU=0 Radius=10 StartAngle=4.87984 EndAngle=6.11574
    g29: ArcOfCircle CenterX=126 CenterY=-4 CenterZ=0 NormalX=0 NormalY=0 NormalZ=1 AngleXU=0 Radius=10 StartAngle=3.30904 EndAngle=4.54494
    g30: ArcOfCircle CenterX=126 CenterY=-81 CenterZ=0 NormalX=0 NormalY=0 NormalZ=1 AngleXU=0 Radius=10 StartAngle=1.73824 EndAngle=2.97414
    g31: LineSegment StartX=4 StartY=-81 StartZ=0 EndX=126 EndY=-81 EndZ=0
    g32: LineSegment StartX=126 StartY=-81 StartZ=0 EndX=126 EndY=-4 EndZ=0
    g33: LineSegment StartX=4 StartY=-4 StartZ=0 EndX=4 EndY=-81 EndZ=0
    g34: ArcOfCircle CenterX=6 CenterY=-15.8322 CenterZ=0 NormalX=0 NormalY=0 NormalZ=1 AngleXU=0 Radius=2 StartAngle=1.73824 EndAngle=3.14159
    g35: ArcOfCircle CenterX=124 CenterY=-15.8322 CenterZ=0 NormalX=0 NormalY=0 NormalZ=1 AngleXU=0 Radius=2 StartAngle=3e-16 EndAngle=1.40335
    g36: ArcOfCircle CenterX=15.8322 CenterY=-6 CenterZ=0 NormalX=0 NormalY=0 NormalZ=1 AngleXU=0 Radius=2 StartAngle=1.5708 EndAngle=2.97414
    g37: ArcOfCircle CenterX=114.168 CenterY=-6 CenterZ=0 NormalX=0 NormalY=0 NormalZ=1 AngleXU=0 Radius=2 StartAngle=0.167448 EndAngle=1.5708
    g38: ArcOfCircle CenterX=124 CenterY=-69.1678 CenterZ=0 NormalX=0 NormalY=0 NormalZ=1 AngleXU=0 Radius=2 StartAngle=4.87984 EndAngle=6.28319
    g39: ArcOfCircle CenterX=114.168 CenterY=-79 CenterZ=0 NormalX=0 NormalY=0 NormalZ=1 AngleXU=0 Radius=2 StartAngle=4.71239 EndAngle=6.11574
    g40: ArcOfCircle CenterX=15.8322 CenterY=-79 CenterZ=0 NormalX=0 NormalY=0 NormalZ=1 AngleXU=0 Radius=2 StartAngle=3.30904 EndAngle=4.71239
    g41: LineSegment StartX=4 StartY=-4 StartZ=0 EndX=126 EndY=-4 EndZ=0
    g42: LineSegment StartX=4 StartY=-15.8322 StartZ=0 EndX=4 EndY=-69.1678 EndZ=0
    g43: LineSegment StartX=126 StartY=-69.1678 StartZ=0 EndX=126 EndY=-15.8322 EndZ=0
    g44: LineSegment StartX=114.168 StartY=-4 StartZ=0 EndX=15.8322 EndY=-4 EndZ=0
    g45: LineSegment StartX=15.8322 StartY=-81 StartZ=0 EndX=114.168 EndY=-81 EndZ=0
  constraints (107):
    c: Tangent(g3,g4) = 1.5708
    c: Coincident(g7,g1)
    c: Coincident(g8,g9)
    c: Coincident(g10,g8)
    c: Horizontal(g8)
    c: Vertical(g9)
    c: Vertical(g10)
    c: Coincident(g8,g3)
    c: Coincident(g9,g6)
    c: Coincident(g0,g5)
    c: Symmetric(g3,g6,g2)
    c: Tangent(g5,g11) = 1.5708
    c: Tangent(g6,g12) = 1.5708
    c: Tangent(g5,g13) = 1.5708
    c: Tangent(g6,g14) = 1.5708
    c: Tangent(g7,g15) = 1.5708
    c: Tangent(g7,g16) = 1.5708
    c: Equal(g3,g5)
    c: Equal(g5,g6)
    c: Equal(g6,g7)
    c: Radius(g3) = 10
    c: Equal(g4,g13)
    c: Equal(g13,g11)
    c: Equal(g11,g14)
    c: Equal(g12,g15)
    c: Tangent(g16,g8) = -1.5708
    c: Tangent(g4,g10) = -1.5708
    c: Coincident(g8,g7)
    c: Tangent(g17,g8) = -1.5708
    c: Tangent(g17,g3) = 1.5708
    c: Radius(g17) = 2
    c: Tangent(g12,g9) = -1.5708
    c: Tangent(g15,g9) = -1.5708
    c: Tangent(g11,g10) = -1.5708
    c: Coincident(g18,g5)
    c: Horizontal(g18)
    c: Coincident(g18,g6)
    c: Coincident(g10,g5)
    c: Tangent(g13,g18) = 1.5708
    c: Tangent(g14,g18) = 1.5708
    c: Equal(g11,g12)
    c: Equal(g14,g17)
    c: Equal(g17,g16)
    c: Coincident(g19,g11)
    c: Coincident(g19,g4)
    c: Coincident(g20,g15)
    c: Coincident(g20,g12)
    c: Coincident(g21,g14)
    c: Coincident(g21,g13)
    c: Coincident(g22,g17)
    c: Coincident(g22,g16)
    c: Tangent(g26,g27) = 1.5708
    c: Coincident(g30,g24)
    c: Coincident(g31,g32)
    c: Coincident(g33,g31)
    c: Horizontal(g31)
    c: Vertical(g32)
    c: Vertical(g33)
    c: Coincident(g31,g26)
    c: Coincident(g32,g29)
    c: Coincident(g23,g28)
    c: Symmetric(g26,g29,g25)
    c: Tangent(g28,g34) = 1.5708
    c: Tangent(g29,g35) = 1.5708
    c: Tangent(g28,g36) = 1.5708
    c: Tangent(g29,g37) = 1.5708
    c: Tangent(g30,g38) = 1.5708
    c: Tangent(g30,g39) = 1.5708
    c: Equal(g26,g28)
    c: Equal(g28,g29)
    c: Equal(g29,g30)
    c: Radius(g26) = 10
    c: Equal(g27,g36)
    c: Equal(g36,g34)
    c: Equal(g34,g37)
    c: Equal(g35,g38)
    c: Tangent(g39,g31) = -1.5708
    c: Tangent(g27,g33) = -1.5708
    c: Coincident(g31,g30)
    c: Tangent(g40,g31) = -1.5708
    c: Tangent(g40,g26) = 1.5708
    c: Radius(g40) = 2
    c: Tangent(g35,g32) = -1.5708
    c: Tangent(g38,g32) = -1.5708
    c: Tangent(g34,g33) = -1.5708
    c: Coincident(g41,g28)
    c: Horizontal(g41)
    c: Coincident(g41,g29)
    c: Coincident(g33,g28)
    c: Tangent(g36,g41) = 1.5708
    c: Tangent(g37,g41) = 1.5708
    c: Equal(g34,g35)
    c: Equal(g37,g40)
    c: Equal(g40,g39)
    c: Coincident(g42,g34)
    c: Coincident(g42,g27)
    c: Coincident(g43,g38)
    c: Coincident(g43,g35)
    c: Coincident(g44,g37)
    c: Coincident(g44,g36)
    c: Coincident(g45,g40)
    c: Coincident(g45,g39)
    c: Symmetric(g28,g30,g2)
    c: Coincident(g34,g-3)
    c: Coincident(g38,g-4)
    c: DistanceX(g27,g4) = 1
    c: DistanceY(g40,g17) = 1
FEATURE [PartDesign::Pad] Pad009
  BaseFeature = -> Hole003
  Direction = (0,0,-1)
  Length = 10
  Length2 = 10
  Profile = -> Sketch032
  ReferenceAxis = -> Sketch032 [N_Axis]
  Reversed = true
  Type = 0
FEATURE [PartDesign::Line] HoleAxis_006
  AttacherType = Attacher::AttachEngineLine
  Length = 4.79083
  MapMode = 19
  Placement = pos=(123.349,78.3485,-4.8) rot=(0,1,0;3.14159rad)
  ResizeMode = 1
  Support = -> [Pad009]
FEATURE [PartDesign::Line] HoleAxis_007
  AttacherType = Attacher::AttachEngineLine
  Length = 4.79083
  MapMode = 19
  Placement = pos=(6.65146,6.65148,-4.8) rot=(0,1,0;3.14159rad)
  ResizeMode = 1
  Support = -> [Pad009]
FEATURE [Sketcher::SketchObject] Sketch035
  ExternalGeometry = -> [Pad009]
  FullyConstrained = true
  MapMode = 5
  Placement = pos=(0,0,-7) rot=(0,0,1;0rad)
  Support = -> [Pad009]
  sketch-geometry (3):
    g0: Circle CenterX=65 CenterY=20 CenterZ=0 NormalX=0 NormalY=0 NormalZ=1 AngleXU=0 Radius=6
    g1: GeomPoint X=65 Y=0 Z=0
    g2: LineSegment StartX=65 StartY=0 StartZ=0 EndX=65 EndY=20 EndZ=0
  constraints (6):
    c: Diameter(g0) = 12
    c: Symmetric(g-3,g-3,g1)
    c: Coincident(g2,g1)
    c: Coincident(g2,g0)
    c: Vertical(g2)
    c: DistanceY(g2,g2) = 20
FEATURE [PartDesign::Hole] Hole005
  BaseFeature = -> Pad009
  CustomThreadClearance = 0
  Depth = 25
  DepthType = 0
  Diameter = 12.1
  DrillForDepth = false
  DrillPoint = 1
  DrillPointAngle = 118
  HoleCutCountersinkAngle = 90
  HoleCutCustomValues = false
  HoleCutDepth = 0
  HoleCutDiameter = 13.6
  HoleCutType = 0
  ModelThread = false
  Profile = -> Sketch035
  Refine = true
  Tapered = false
  TaperedAngle = 90
  ThreadClass = 0
  ThreadDepth = 25
  ThreadDepthType = 0
  ThreadDirection = 0
  ThreadFit = 0
  ThreadSize = 19
  ThreadType = 1
  Threaded = false
  UseCustomThreadClearance = false
FEATURE [Sketcher::SketchObject] Sketch036
  ExternalGeometry = -> [HoleAxis_006,HoleAxis_007]
  FullyConstrained = true
  MapMode = 5
  Placement = pos=(0,0,-7) rot=(0,0,1;0rad)
  Support = -> [Hole005]
  sketch-geometry (24):
    g0: ArcOfCircle CenterX=23.5 CenterY=46.5 CenterZ=0 NormalX=0 NormalY=0 NormalZ=1 AngleXU=0 Radius=2 StartAngle=1.5708 EndAngle=3.14159
    g1: LineSegment StartX=23.5 StartY=48.5 StartZ=0 EndX=31.5 EndY=48.5 EndZ=0
    g2: ArcOfCircle CenterX=31.5 CenterY=46.5 CenterZ=0 NormalX=0 NormalY=0 NormalZ=1 AngleXU=0 Radius=2 StartAngle=0 EndAngle=1.5708
    g3: LineSegment StartX=33.5 StartY=46.5 StartZ=0 EndX=33.5 EndY=38.5 EndZ=0
    g4: ArcOfCircle CenterX=31.5 CenterY=38.5 CenterZ=0 NormalX=0 NormalY=0 NormalZ=1 AngleXU=0 Radius=2 StartAngle=4.71239 EndAngle=6.28319
    g5: LineSegment StartX=31.5 StartY=36.5 StartZ=0 EndX=23.5 EndY=36.5 EndZ=0
    g6: ArcOfCircle CenterX=23.5 CenterY=38.5 CenterZ=0 NormalX=0 NormalY=0 NormalZ=1 AngleXU=0 Radius=2 StartAngle=3.14159 EndAngle=4.71239
    g7: LineSegment StartX=21.5 StartY=38.5 StartZ=0 EndX=21.5 EndY=46.5 EndZ=0
    g8: GeomPoint X=21.5 Y=48.5 Z=0
    g9: GeomPoint X=33.5 Y=36.5 Z=0
    g10: ArcOfCircle CenterX=98.5 CenterY=46.5 CenterZ=0 NormalX=0 NormalY=0 NormalZ=1 AngleXU=0 Radius=2 StartAngle=1.5708 EndAngle=3.14159
    g11: LineSegment StartX=98.5 StartY=48.5 StartZ=0 EndX=106.5 EndY=48.5 EndZ=0
    g12: ArcOfCircle CenterX=106.5 CenterY=46.5 CenterZ=0 NormalX=0 NormalY=0 NormalZ=1 AngleXU=0 Radius=2 StartAngle=6e-16 EndAngle=1.5708
    g13: LineSegment StartX=108.5 StartY=46.5 StartZ=0 EndX=108.5 EndY=38.5 EndZ=0
    g14: ArcOfCircle CenterX=106.5 CenterY=38.5 CenterZ=0 NormalX=0 NormalY=0 NormalZ=1 AngleXU=0 Radius=2 StartAngle=4.71239 EndAngle=6.28319
    g15: LineSegment StartX=106.5 StartY=36.5 StartZ=0 EndX=98.5 EndY=36.5 EndZ=0
    g16: ArcOfCircle CenterX=98.5 CenterY=38.5 CenterZ=0 NormalX=0 NormalY=0 NormalZ=1 AngleXU=0 Radius=2 StartAngle=3.14159 EndAngle=4.71239
    g17: LineSegment StartX=96.5 StartY=38.5 StartZ=0 EndX=96.5 EndY=46.5 EndZ=0
    g18: GeomPoint X=96.5 Y=48.5 Z=0
    g19: GeomPoint X=108.5 Y=36.5 Z=0
    g20: GeomPoint X=27.5 Y=42.5 Z=0
    g21: GeomPoint X=102.5 Y=42.5 Z=0
    g22: GeomPoint X=65 Y=42.5 Z=0
    g23: LineSegment StartX=27.5 StartY=42.5 StartZ=0 EndX=102.5 EndY=42.5 EndZ=0
  constraints (53):
    c: Tangent(g0,g1) = 1.5708
    c: Tangent(g1,g2) = 1.5708
    c: Tangent(g2,g3) = 1.5708
    c: Tangent(g3,g4) = 1.5708
    c: Tangent(g4,g5) = 1.5708
    c: Tangent(g5,g6) = 1.5708
    c: Tangent(g6,g7) = 1.5708
    c: Tangent(g7,g0) = 1.5708
    c: Horizontal(g1)
    c: Horizontal(g5)
    c: Vertical(g3)
    c: Vertical(g7)
    c: Equal(g2,g4)
    c: Equal(g4,g6)
    c: PointOnObject(g8,g1)
    c: PointOnObject(g8,g7)
    c: PointOnObject(g9,g3)
    c: PointOnObject(g9,g5)
    c: Tangent(g10,g11) = 1.5708
    c: Tangent(g11,g12) = 1.5708
    c: Tangent(g12,g13) = 1.5708
    c: Tangent(g13,g14) = 1.5708
    c: Tangent(g14,g15) = 1.5708
    c: Tangent(g15,g16) = 1.5708
    c: Tangent(g16,g17) = 1.5708
    c: Tangent(g17,g10) = 1.5708
    c: Horizontal(g11)
    c: Horizontal(g15)
    c: Vertical(g13)
    c: Vertical(g17)
    c: Equal(g10,g12)
    c: Equal(g12,g14)
    c: Equal(g14,g16)
    c: PointOnObject(g18,g11)
    c: PointOnObject(g18,g17)
    c: PointOnObject(g19,g13)
    c: PointOnObject(g19,g15)
    c: Symmetric(g16,g12,g21)
    c: Symmetric(g2,g6,g20)
    c: Equal(g1,g11)
    c: Equal(g3,g13)
    c: Symmetric(g-4,g-3,g22)
    c: Symmetric(g21,g20,g22)
    c: Coincident(g23,g20)
    c: Coincident(g23,g21)
    c: Horizontal(g23)
    c: Equal(g2,g0)
    c: Equal(g6,g16)
    c: Radius(g4) = 2
    c: DistanceX(g8,g9) = 12  'Breite Klickfixadapter'
    c: DistanceY(g9,g8) = 12
    c: DistanceX(g23,g23) = 75
    c: DistanceX(g8,g19) = 87
FEATURE [PartDesign::Pad] Pad010
  BaseFeature = -> Hole005
  Direction = (0,0,1)
  Length = 5
  Length2 = 10
  Profile = -> Sketch036
  ReferenceAxis = -> Sketch036 [N_Axis]
  Refine = true
  Type = 0
FEATURE [Sketcher::SketchObject] Sketch037
  ExternalGeometry = -> [Pad010]
  FullyConstrained = true
  MapMode = 5
  Placement = pos=(0,0,-10) rot=(1,0,0;3.14159rad)
  Support = -> [Pad010]
  sketch-geometry (22):
    g0: ArcOfCircle CenterX=24.5 CenterY=-39.5 CenterZ=0 NormalX=0 NormalY=0 NormalZ=1 AngleXU=0 Radius=2 StartAngle=1.5708 EndAngle=3.14159
    g1: LineSegment StartX=24.5 StartY=-37.5 StartZ=0 EndX=30.5 EndY=-37.5 EndZ=0
    g2: ArcOfCircle CenterX=30.5 CenterY=-39.5 CenterZ=0 NormalX=0 NormalY=0 NormalZ=1 AngleXU=0 Radius=2 StartAngle=-2.7e-15 EndAngle=1.5708
    g3: LineSegment StartX=32.5 StartY=-39.5 StartZ=0 EndX=32.5 EndY=-45.5 EndZ=0
    g4: ArcOfCircle CenterX=30.5 CenterY=-45.5 CenterZ=0 NormalX=0 NormalY=0 NormalZ=1 AngleXU=0 Radius=2 StartAngle=4.71239 EndAngle=6.28319
    g5: LineSegment StartX=30.5 StartY=-47.5 StartZ=0 EndX=24.5 EndY=-47.5 EndZ=0
    g6: ArcOfCircle CenterX=24.5 CenterY=-45.5 CenterZ=0 NormalX=0 NormalY=0 NormalZ=1 AngleXU=0 Radius=2 StartAngle=3.14159 EndAngle=4.71239
    g7: LineSegment StartX=22.5 StartY=-45.5 StartZ=0 EndX=22.5 EndY=-39.5 EndZ=0
    g8: GeomPoint X=22.5 Y=-37.5 Z=0
    g9: GeomPoint X=32.5 Y=-47.5 Z=0
    g10: ArcOfCircle CenterX=99.5 CenterY=-39.5 CenterZ=0 NormalX=0 NormalY=0 NormalZ=1 AngleXU=0 Radius=2 StartAngle=1.5708 EndAngle=3.14159
    g11: LineSegment StartX=99.5 StartY=-37.5 StartZ=0 EndX=105.5 EndY=-37.5 EndZ=0
    g12: ArcOfCircle CenterX=105.5 CenterY=-39.5 CenterZ=0 NormalX=0 NormalY=0 NormalZ=1 AngleXU=0 Radius=2 StartAngle=-7.1e-15 EndAngle=1.5708
    g13: LineSegment StartX=107.5 StartY=-39.5 StartZ=0 EndX=107.5 EndY=-45.5 EndZ=0
    g14: ArcOfCircle CenterX=105.5 CenterY=-45.5 CenterZ=0 NormalX=0 NormalY=0 NormalZ=1 AngleXU=0 Radius=2 StartAngle=4.71239 EndAngle=6.28319
    g15: LineSegment StartX=105.5 StartY=-47.5 StartZ=0 EndX=99.5 EndY=-47.5 EndZ=0
    g16: ArcOfCircle CenterX=99.5 CenterY=-45.5 CenterZ=0 NormalX=0 NormalY=0 NormalZ=1 AngleXU=0 Radius=2 StartAngle=3.14159 EndAngle=4.71239
    g17: LineSegment StartX=97.5 StartY=-45.5 StartZ=0 EndX=97.5 EndY=-39.5 EndZ=0
    g18: GeomPoint X=97.5 Y=-37.5 Z=0
    g19: GeomPoint X=107.5 Y=-47.5 Z=0
    g20: GeomPoint X=27.5 Y=-42.5 Z=0
    g21: GeomPoint X=102.5 Y=-42.5 Z=0
  constraints (49):
    c: Equal(g4,g6)
    c: PointOnObject(g8,g1)
    c: PointOnObject(g8,g7)
    c: PointOnObject(g9,g3)
    c: PointOnObject(g9,g5)
    c: Tangent(g10,g11) = 1.5708
    c: Tangent(g11,g12) = 1.5708
    c: Tangent(g12,g13) = 1.5708
    c: Tangent(g13,g14) = 1.5708
    c: Tangent(g14,g15) = 1.5708
    c: Tangent(g15,g16) = 1.5708
    c: Tangent(g16,g17) = 1.5708
    c: Tangent(g17,g10) = 1.5708
    c: Horizontal(g11)
    c: Horizontal(g15)
    c: Vertical(g13)
    c: Vertical(g17)
    c: Equal(g10,g12)
    c: Equal(g12,g14)
    c: Equal(g14,g16)
    c: PointOnObject(g18,g11)
    c: PointOnObject(g18,g17)
    c: PointOnObject(g19,g13)
    c: PointOnObject(g19,g15)
    c: Equal(g10,g4)
    c: Horizontal(g1)
    c: Vertical(g3)
    c: Vertical(g7)
    c: Horizontal(g5)
    c: Tangent(g6,g7) = 1.5708
    c: Tangent(g3,g4) = 1.5708
    c: Tangent(g1,g2) = 1.5708
    c: Tangent(g0,g7) = 1.5708
    c: Tangent(g0,g1) = 1.5708
    c: Tangent(g3,g2) = 1.5708
    c: Tangent(g5,g4) = 1.5708
    c: Tangent(g5,g6) = 1.5708
    c: Equal(g6,g0)
    c: Equal(g0,g2)
    c: Radius(g0) = 2
    c: DistanceX(g0,g2) = 10
    c: DistanceY(g4,g1) = 10
    c: Symmetric(g6,g2,g20)
    c: Symmetric(g-4,g-3,g20)
    c: Equal(g3,g13)
    c: Symmetric(g16,g12,g21)
    c: Symmetric(g-5,g-6,g21)
    c: Equal(g13,g11)
    c: DistanceX(g6,g13) = 85
FEATURE [PartDesign::Pocket] Pocket012
  BaseFeature = -> Pad010
  Direction = (0,0,1)
  Length = 3
  Length2 = 5
  Profile = -> Sketch037
  ReferenceAxis = -> Sketch037 [N_Axis]
  Refine = true
  Type = 0
FEATURE [Sketcher::SketchObject] Sketch033
  ExternalGeometry = -> [Pad010]
  FullyConstrained = true
  MapMode = 5
  Placement = pos=(0,0,-2) rot=(0,0,1;0rad)
  Support = -> [Pocket012]
  sketch-geometry (2):
    g0: Circle CenterX=27.5 CenterY=42.5 CenterZ=0 NormalX=0 NormalY=0 NormalZ=1 AngleXU=0 Radius=2
    g1: Circle CenterX=102.5 CenterY=42.5 CenterZ=0 NormalX=0 NormalY=0 NormalZ=1 AngleXU=0 Radius=2
  constraints (4):
    c: Equal(g0,g1)
    c: Symmetric(g-5,g-6,g0)
    c: Symmetric(g-4,g-3,g1)
    c: Diameter(g0) = 4
FEATURE [PartDesign::Hole] Hole004
  BaseFeature = -> Pocket012
  CustomThreadClearance = 0
  Depth = 8
  DepthType = 0
  Diameter = 4.5
  DrillForDepth = false
  DrillPoint = 1
  DrillPointAngle = 118
  HoleCutCountersinkAngle = 90
  HoleCutCustomValues = false
  HoleCutDepth = 3.2
  HoleCutDiameter = 8
  HoleCutType = 6
  ModelThread = false
  Profile = -> Sketch033
  Refine = true
  Tapered = false
  TaperedAngle = 90
  ThreadClass = 0
  ThreadDepth = 8
  ThreadDepthType = 0
  ThreadDirection = 0
  ThreadFit = 0
  ThreadSize = 11
  ThreadType = 1
  Threaded = false
  UseCustomThreadClearance = false
FEATURE [Sketcher::SketchObject] Sketch034  label="Stabilisierung - Pfad001"
  ExternalGeometry = -> [Hole004]
  FullyConstrained = true
  MapMode = 5
  Placement = pos=(0,0,-7) rot=(0,0,1;0rad)
  Support = -> [Hole004]
  sketch-geometry (13):
    g0: LineSegment StartX=14.6316 StartY=70.3684 StartZ=0 EndX=10.7634 EndY=74.2366 EndZ=0
    g1: LineSegment StartX=15.0973 StartY=69.6369 StartZ=0 EndX=22.9672 EndY=47.9672 EndZ=0
    g2: LineSegment StartX=12.0711 StartY=72.9289 StartZ=0 EndX=14.8601 EndY=78.3333 EndZ=0
    g3: LineSegment StartX=12.0711 StartY=72.9289 StartZ=0 EndX=6.66667 EndY=70.1399 EndZ=0
    g4: ArcOfCircle CenterX=13.2174 CenterY=68.9542 CenterZ=0 NormalX=0 NormalY=0 NormalZ=1 AngleXU=0 Radius=2 StartAngle=0.348363 EndAngle=0.785398
    g5: GeomPoint X=14.9457 Y=70.0543 Z=0
    g6: LineSegment StartX=10.7634 StartY=74.2366 StartZ=0 EndX=22.9672 EndY=47.9672 EndZ=0
    g7: LineSegment StartX=21.5 StartY=46.5 StartZ=0 EndX=23.5 EndY=48.5 EndZ=0
    g8: LineSegment StartX=6.66667 StartY=70.1399 StartZ=0 EndX=14.8601 EndY=78.3333 EndZ=0
    g9: LineSegment StartX=22.7885 StartY=37.2115 StartZ=0 EndX=9.10088 EndY=12.4259 EndZ=0
    g10: LineSegment StartX=6.66667 StartY=14.8601 StartZ=0 EndX=14.8601 EndY=6.66667 EndZ=0
    g11: LineSegment StartX=22.7885 StartY=37.2115 StartZ=0 EndX=22.9672 EndY=47.9672 EndZ=0
    g12: LineSegment StartX=21.5 StartY=38.5 StartZ=0 EndX=23.5 EndY=36.5 EndZ=0
  constraints (32):
    c: Perpendicular(g-4,g1)
    c: Coincident(g2,g-3)
    c: Coincident(g3,g-3)
    c: Equal(g3,g2)
    c: PointOnObject(g5,g0)
    c: PointOnObject(g5,g1)
    c: Tangent(g0,g4) = -1.5708
    c: Tangent(g1,g4) = 1.5708
    c: Radius(g4) = 2
    c: PointOnObject(g4,g6)
    c: Coincident(g6,g1)
    c: Coincident(g8,g3)
    c: Coincident(g8,g2)
    c: Coincident(g6,g0)
    c: PointOnObject(g0,g8)
    c: Coincident(g2,g3)
    c: PointOnObject(g2,g0)
    c: PointOnObject(g2,g-3)
    c: Perpendicular(g0,g-3,g2) = 4.71239
    c: PointOnObject(g1,g7)
    c: Coincident(g7,g-4)
    c: Coincident(g7,g-4)
    c: Coincident(g10,g-5)
    c: Coincident(g10,g-5)
    c: PointOnObject(g9,g10)
    c: Perpendicular(g-5,g9)
    c: Coincident(g11,g9)
    c: Coincident(g11,g1)
    c: Perpendicular(g-6,g9)
    c: Coincident(g12,g-6)
    c: Coincident(g12,g-6)
    c: PointOnObject(g9,g12)
FEATURE [Sketcher::SketchObject] Sketch038  label="Stabilisierung - Profil001"
  FullyConstrained = true
  MapMode = 7
  Placement = pos=(15.0973,69.6369,-7) rot=(-0.123474,0.701696,0.701696;3.3873rad)
  Support = -> [Sketch034]
  sketch-geometry (7):
    g0: LineSegment StartX=-1 StartY=0 StartZ=0 EndX=1 EndY=0 EndZ=0
    g1: ArcOfCircle CenterX=0 CenterY=0.522986 CenterZ=0 NormalX=0 NormalY=0 NormalZ=1 AngleXU=0 Radius=0.477014 StartAngle=0.261799 EndAngle=2.87979
    g2: ArcOfCircle CenterX=1 CenterY=0.477014 CenterZ=0 NormalX=0 NormalY=0 NormalZ=1 AngleXU=0 Radius=0.477014 StartAngle=3.40339 EndAngle=4.71239
    g3: LineSegment StartX=0.53924 StartY=0.353553 StartZ=0 EndX=0.46076 EndY=0.646447 EndZ=0
    g4: LineSegment StartX=-0.53924 StartY=0.353553 StartZ=0 EndX=-0.46076 EndY=0.646447 EndZ=0
    g5: ArcOfCircle CenterX=-1 CenterY=0.477014 CenterZ=0 NormalX=0 NormalY=0 NormalZ=1 AngleXU=0 Radius=0.477014 StartAngle=4.71239 EndAngle=6.02139
    g6: GeomPoint X=0 Y=1 Z=0
  constraints (16):
    c: PointOnObject(g0,g-1)
    c: Symmetric(g0,g0,g-1)
    c: PointOnObject(g1,g-2)
    c: Tangent(g3,g1) = -1.5708
    c: Tangent(g3,g2) = 1.5708
    c: Tangent(g2,g0) = -1.5708
    c: Tangent(g4,g5) = -1.5708
    c: Tangent(g1,g4) = 1.5708
    c: Equal(g4,g3)
    c: PointOnObject(g6,g-2)
    c: PointOnObject(g6,g1)
    c: DistanceY(g-1,g6) = 1
    c: DistanceX(g0,g0) = 2
    c: Tangent(g0,g5) = -1.5708
    c: Angle(g-2,g3) = 0.261799
    c: Equal(g1,g5)
FEATURE [PartDesign::AdditiveBox] Box004
  AttacherType = Attacher::AttachEngine3D
  Height = 20
  Length = 130
  Width = 85
FEATURE [Sketcher::SketchObject] Sketch039
  ExternalGeometry = -> [Box004]
  FullyConstrained = true
  MapMode = 5
  Placement = pos=(0,0,0) rot=(1,0,0;3.14159rad)
  Support = -> [Box004]
  sketch-geometry (23):
    g0: LineSegment StartX=15.8322 StartY=-4 StartZ=0 EndX=114.168 EndY=-4 EndZ=0
    g1: LineSegment StartX=126 StartY=-15.8322 StartZ=0 EndX=126 EndY=-69.1678 EndZ=0
    g2: LineSegment StartX=114.168 StartY=-81 StartZ=0 EndX=15.8322 EndY=-81 EndZ=0
    g3: LineSegment StartX=4 StartY=-69.1678 StartZ=0 EndX=4 EndY=-15.8322 EndZ=0
    g4: GeomPoint X=4 Y=-4 Z=0
    g5: GeomPoint X=126 Y=-81 Z=0
    g6: GeomPoint X=65 Y=-42.5 Z=0
    g7: ArcOfCircle CenterX=4 CenterY=-81 CenterZ=0 NormalX=0 NormalY=0 NormalZ=1 AngleXU=0 Radius=10 StartAngle=0.167448 EndAngle=1.40335
    g8: ArcOfCircle CenterX=6 CenterY=-69.1678 CenterZ=0 NormalX=0 NormalY=0 NormalZ=1 AngleXU=0 Radius=2 StartAngle=3.14159 EndAngle=4.54494
    g9: ArcOfCircle CenterX=15.8322 CenterY=-79 CenterZ=0 NormalX=0 NormalY=0 NormalZ=1 AngleXU=0 Radius=2 StartAngle=3.30904 EndAngle=4.71239
    g10: ArcOfCircle CenterX=4 CenterY=-4 CenterZ=0 NormalX=0 NormalY=0 NormalZ=1 AngleXU=0 Radius=10 StartAngle=4.87984 EndAngle=6.11574
    g11: ArcOfCircle CenterX=126 CenterY=-4 CenterZ=0 NormalX=0 NormalY=0 NormalZ=1 AngleXU=0 Radius=10 StartAngle=3.30904 EndAngle=4.54494
    g12: ArcOfCircle CenterX=126 CenterY=-81 CenterZ=0 NormalX=0 NormalY=0 NormalZ=1 AngleXU=0 Radius=10 StartAngle=1.73824 EndAngle=2.97414
    g13: LineSegment StartX=4 StartY=-81 StartZ=0 EndX=126 EndY=-81 EndZ=0
    g14: LineSegment StartX=126 StartY=-81 StartZ=0 EndX=126 EndY=-4 EndZ=0
    g15: LineSegment StartX=126 StartY=-4 StartZ=0 EndX=4 EndY=-4 EndZ=0
    g16: LineSegment StartX=4 StartY=-4 StartZ=0 EndX=4 EndY=-81 EndZ=0
    g17: ArcOfCircle CenterX=6 CenterY=-15.8322 CenterZ=0 NormalX=0 NormalY=0 NormalZ=1 AngleXU=0 Radius=2 StartAngle=1.73824 EndAngle=3.14159
    g18: ArcOfCircle CenterX=124 CenterY=-15.8322 CenterZ=0 NormalX=0 NormalY=0 NormalZ=1 AngleXU=0 Radius=2 StartAngle=0 EndAngle=1.40335
    g19: ArcOfCircle CenterX=15.8322 CenterY=-6 CenterZ=0 NormalX=0 NormalY=0 NormalZ=1 AngleXU=0 Radius=2 StartAngle=1.5708 EndAngle=2.97414
    g20: ArcOfCircle CenterX=114.168 CenterY=-6 CenterZ=0 NormalX=0 NormalY=0 NormalZ=1 AngleXU=0 Radius=2 StartAngle=0.167448 EndAngle=1.5708
    g21: ArcOfCircle CenterX=124 CenterY=-69.1678 CenterZ=0 NormalX=0 NormalY=0 NormalZ=1 AngleXU=0 Radius=2 StartAngle=4.87984 EndAngle=6.28319
    g22: ArcOfCircle CenterX=114.168 CenterY=-79 CenterZ=0 NormalX=0 NormalY=0 NormalZ=1 AngleXU=0 Radius=2 StartAngle=4.71239 EndAngle=6.11574
  constraints (56):
    c: Horizontal(g0)
    c: Horizontal(g2)
    c: Vertical(g1)
    c: Vertical(g3)
    c: PointOnObject(g4,g0)
    c: PointOnObject(g4,g3)
    c: PointOnObject(g5,g1)
    c: PointOnObject(g5,g2)
    c: Symmetric(g-6,g-4,g6)
    c: Tangent(g7,g8) = 1.5708
    c: Tangent(g3,g8) = 1.5708
    c: Tangent(g2,g9) = 1.5708
    c: Tangent(g7,g9) = 1.5708
    c: Coincident(g12,g5)
    c: Coincident(g13,g14)
    c: Coincident(g14,g15)
    c: Coincident(g15,g16)
    c: Coincident(g16,g13)
    c: Horizontal(g13)
    c: Horizontal(g15)
    c: Vertical(g14)
    c: Vertical(g16)
    c: Coincident(g13,g7)
    c: Coincident(g14,g11)
    c: Coincident(g4,g10)
    c: Symmetric(g7,g11,g6)
    c: Tangent(g3,g17) = 1.5708
    c: Tangent(g10,g17) = 1.5708
    c: Tangent(g1,g18) = 1.5708
    c: Tangent(g11,g18) = 1.5708
    c: Tangent(g10,g19) = 1.5708
    c: Tangent(g0,g19) = 1.5708
    c: Tangent(g11,g20) = 1.5708
    c: Tangent(g0,g20) = 1.5708
    c: Tangent(g1,g21) = 1.5708
    c: Tangent(g12,g21) = 1.5708
    c: Tangent(g2,g22) = 1.5708
    c: Tangent(g12,g22) = 1.5708
    c: PointOnObject(g0,g15)
    c: PointOnObject(g3,g16)
    c: PointOnObject(g1,g14)
    c: DistanceX(g-6,g7) = 4
    c: DistanceY(g-6,g7) = 4
    c: PointOnObject(g2,g13)
    c: Equal(g7,g10)
    c: Equal(g10,g11)
    c: Equal(g11,g12)
    c: Radius(g7) = 10
    c: Equal(g9,g8)
    c: Equal(g8,g19)
    c: Equal(g19,g17)
    c: Equal(g17,g20)
    c: Equal(g20,g18)
    c: Equal(g18,g21)
    c: Equal(g21,g22)
    c: Radius(g9) = 2
FEATURE [PartDesign::Pocket] Pocket016
  BaseFeature = -> Box004
  Direction = (0,0,1)
  Length = 16
  Length2 = 100
  Profile = -> Sketch039
  ReferenceAxis = -> Sketch039 [N_Axis]
  Type = 0
  expr: Length = <<Box004>>.Height - 4mm
FEATURE [Sketcher::SketchObject] Sketch042
  ExternalGeometry = -> [Pocket016]
  FullyConstrained = true
  MapMode = 5
  Placement = pos=(0,0,16) rot=(1,0,0;3.14159rad)
  Support = -> [Pocket016]
  sketch-geometry (11):
    g0: LineSegment StartX=49 StartY=-19 StartZ=0 EndX=81 EndY=-19 EndZ=0
    g1: LineSegment StartX=81 StartY=-19 StartZ=0 EndX=81 EndY=-51 EndZ=0
    g2: LineSegment StartX=81 StartY=-51 StartZ=0 EndX=49 EndY=-51 EndZ=0
    g3: LineSegment StartX=49 StartY=-51 StartZ=0 EndX=49 EndY=-19 EndZ=0
    g4: GeomPoint X=65 Y=-4 Z=0
    g5: LineSegment StartX=65 StartY=-4 StartZ=0 EndX=65 EndY=-19 EndZ=0
    g6: LineSegment StartX=37.5 StartY=-61 StartZ=0 EndX=92.5 EndY=-61 EndZ=0
    g7: LineSegment StartX=92.5 StartY=-61 StartZ=0 EndX=92.5 EndY=-71 EndZ=0
    g8: LineSegment StartX=92.5 StartY=-71 StartZ=0 EndX=37.5 EndY=-71 EndZ=0
    g9: LineSegment StartX=37.5 StartY=-71 StartZ=0 EndX=37.5 EndY=-61 EndZ=0
    g10: LineSegment StartX=65 StartY=-19 StartZ=0 EndX=65 EndY=-61 EndZ=0
  constraints (29):
    c: Coincident(g0,g1)
    c: Coincident(g1,g2)
    c: Coincident(g2,g3)
    c: Coincident(g3,g0)
    c: Horizontal(g0)
    c: Horizontal(g2)
    c: Vertical(g1)
    c: Vertical(g3)
    c: Coincident(g5,g4)
    c: Vertical(g5)
    c: Symmetric(g0,g0,g5)
    c: DistanceY(g5,g5) = 15
    c: DistanceY(g1,g1) = 32
    c: Equal(g1,g0)
    c: Coincident(g6,g7)
    c: Coincident(g7,g8)
    c: Coincident(g8,g9)
    c: Coincident(g9,g6)
    c: Horizontal(g6)
    c: Horizontal(g8)
    c: Vertical(g7)
    c: Vertical(g9)
    c: DistanceX(g6,g6) = 55
    c: DistanceY(g7,g7) = 10
    c: Coincident(g10,g5)
    c: Vertical(g10)
    c: Symmetric(g6,g6,g10)
    c: DistanceY(g6,g1) = 10
    c: Symmetric(g-3,g-3,g4)
FEATURE [PartDesign::Pocket] Pocket017  label="Platz OLED und LED-Strip002"
  BaseFeature = -> Pocket016
  Direction = (0,0,1)
  Length = 3
  Length2 = 100
  Profile = -> Sketch042
  Type = 0
FEATURE [Sketcher::SketchObject] Sketch041
  ExternalGeometry = -> [Sketch042,Pocket017]
  FullyConstrained = true
  MapMode = 5
  Placement = pos=(0,0,16) rot=(1,0,0;3.14159rad)
  Support = -> [Pocket017]
  sketch-geometry (10):
    g0: LineSegment StartX=51.75 StartY=-29.5 StartZ=0 EndX=78.25 EndY=-29.5 EndZ=0
    g1: LineSegment StartX=78.25 StartY=-29.5 StartZ=0 EndX=78.25 EndY=-44.5 EndZ=0
    g2: LineSegment StartX=78.25 StartY=-44.5 StartZ=0 EndX=51.75 EndY=-44.5 EndZ=0
    g3: LineSegment StartX=51.75 StartY=-44.5 StartZ=0 EndX=51.75 EndY=-29.5 EndZ=0
    g4: LineSegment StartX=38 StartY=-62 StartZ=0 EndX=92 EndY=-62 EndZ=0
    g5: LineSegment StartX=92 StartY=-62 StartZ=0 EndX=92 EndY=-67 EndZ=0
    g6: LineSegment StartX=92 StartY=-67 StartZ=0 EndX=38 EndY=-67 EndZ=0
    g7: LineSegment StartX=38 StartY=-67 StartZ=0 EndX=38 EndY=-62 EndZ=0
    g8: LineSegment StartX=65 StartY=-62 StartZ=0 EndX=65 EndY=-61 EndZ=0
    g9: LineSegment StartX=65 StartY=-29.5 StartZ=0 EndX=65 EndY=-19 EndZ=0
  constraints (28):
    c: Coincident(g0,g1)
    c: Coincident(g1,g2)
    c: Coincident(g2,g3)
    c: Coincident(g3,g0)
    c: Horizontal(g0)
    c: Horizontal(g2)
    c: Vertical(g1)
    c: Vertical(g3)
    c: DistanceX(g0,g0) = 26.5
    c: DistanceY(g1,g1) = 15
    c: Coincident(g4,g5)
    c: Coincident(g5,g6)
    c: Coincident(g6,g7)
    c: Coincident(g7,g4)
    c: Horizontal(g4)
    c: Horizontal(g6)
    c: Vertical(g5)
    c: Vertical(g7)
    c: DistanceX(g4,g-3) = 0.5
    c: Vertical(g8)
    c: Symmetric(g4,g4,g8)
    c: Symmetric(g-3,g-4,g8)
    c: DistanceY(g5,g5) = 5
    c: DistanceY(g4,g-3) = 1
    c: Vertical(g9)
    c: Symmetric(g0,g0,g9)
    c: DistanceY(g9,g9) = 10.5
    c: Symmetric(g-5,g-5,g9)
FEATURE [PartDesign::Pocket] Pocket018  label="Sichtausschnitt002"
  BaseFeature = -> Pocket017
  Direction = (0,0,1)
  Length = 1.01
  Length2 = 100
  Profile = -> Sketch041
  ReferenceAxis = -> Sketch041 [N_Axis]
  Type = 1
FEATURE [Sketcher::SketchObject] Sketch043  label="Sketch Halter OLED002"
  ExternalGeometry = -> [Sketch042]
  FullyConstrained = true
  MapMode = 5
  Placement = pos=(0,0,19) rot=(1,0,0;3.14159rad)
  Support = -> [Pocket018]
  sketch-geometry (9):
    g0: Circle CenterX=53.1 CenterY=-23.35 CenterZ=0 NormalX=0 NormalY=0 NormalZ=1 AngleXU=0 Radius=1
    g1: Circle CenterX=76.9 CenterY=-23.35 CenterZ=0 NormalX=0 NormalY=0 NormalZ=1 AngleXU=0 Radius=1
    g2: Circle CenterX=76.9 CenterY=-46.65 CenterZ=0 NormalX=0 NormalY=0 NormalZ=1 AngleXU=0 Radius=1
    g3: Circle CenterX=53.1 CenterY=-46.65 CenterZ=0 NormalX=0 NormalY=0 NormalZ=1 AngleXU=0 Radius=1
    g4: LineSegment StartX=53.1 StartY=-23.35 StartZ=0 EndX=76.9 EndY=-23.35 EndZ=0
    g5: LineSegment StartX=76.9 StartY=-23.35 StartZ=0 EndX=76.9 EndY=-46.65 EndZ=0
    g6: LineSegment StartX=76.9 StartY=-46.65 StartZ=0 EndX=53.1 EndY=-46.65 EndZ=0
    g7: LineSegment StartX=53.1 StartY=-46.65 StartZ=0 EndX=53.1 EndY=-23.35 EndZ=0
    g8: GeomPoint X=65 Y=-35 Z=0
  constraints (20):
    c: Coincident(g4,g5)
    c: Coincident(g5,g6)
    c: Coincident(g6,g7)
    c: Coincident(g7,g4)
    c: Horizontal(g4)
    c: Horizontal(g6)
    c: Vertical(g5)
    c: Vertical(g7)
    c: Coincident(g4,g0)
    c: Coincident(g5,g2)
    c: Coincident(g1,g4)
    c: Coincident(g3,g6)
    c: Equal(g0,g1)
    c: Equal(g1,g2)
    c: Equal(g2,g3)
    c: Diameter(g1) = 2
    c: DistanceX(g4,g4) = 23.8
    c: DistanceY(g5,g5) = 23.3
    c: Symmetric(g-4,g-6,g8)
    c: Symmetric(g3,g1,g8)
FEATURE [PartDesign::Pad] Pad011  label="Halter OLED002"
  BaseFeature = -> Pocket018
  Direction = (0,0,-1)
  Length = 5
  Length2 = 100
  Profile = -> Sketch043
  ReferenceAxis = -> Sketch043 [N_Axis]
  Type = 0
FEATURE [Sketcher::SketchObject] Sketch040
  ExternalGeometry = -> [Sketch042]
  FullyConstrained = true
  MapMode = 5
  Placement = pos=(0,0,16) rot=(1,0,0;3.14159rad)
  Support = -> [Pad011]
  sketch-geometry (26):
    g0: LineSegment StartX=50 StartY=-11 StartZ=0 EndX=80 EndY=-11 EndZ=0
    g1: LineSegment StartX=80 StartY=-11 StartZ=0 EndX=80 EndY=-18 EndZ=0
    g2: LineSegment StartX=80 StartY=-18 StartZ=0 EndX=50 EndY=-18 EndZ=0
    g3: LineSegment StartX=50 StartY=-18 StartZ=0 EndX=50 EndY=-11 EndZ=0
    g4: LineSegment StartX=82 StartY=-20 StartZ=0 EndX=89 EndY=-20 EndZ=0
    g5: LineSegment StartX=89 StartY=-20 StartZ=0 EndX=89 EndY=-50 EndZ=0
    g6: LineSegment StartX=89 StartY=-50 StartZ=0 EndX=82 EndY=-50 EndZ=0
    g7: LineSegment StartX=82 StartY=-50 StartZ=0 EndX=82 EndY=-20 EndZ=0
    g8: LineSegment StartX=41 StartY=-20 StartZ=0 EndX=48 EndY=-20 EndZ=0
    g9: LineSegment StartX=48 StartY=-20 StartZ=0 EndX=48 EndY=-50 EndZ=0
    g10: LineSegment StartX=48 StartY=-50 StartZ=0 EndX=41 EndY=-50 EndZ=0
    g11: LineSegment StartX=41 StartY=-50 StartZ=0 EndX=41 EndY=-20 EndZ=0
    g12: LineSegment StartX=50 StartY=-52 StartZ=0 EndX=80 EndY=-52 EndZ=0
    g13: LineSegment StartX=80 StartY=-52 StartZ=0 EndX=80 EndY=-59 EndZ=0
    g14: LineSegment StartX=80 StartY=-59 StartZ=0 EndX=50 EndY=-59 EndZ=0
    g15: LineSegment StartX=50 StartY=-59 StartZ=0 EndX=50 EndY=-52 EndZ=0
    g16: LineSegment StartX=48 StartY=-18 StartZ=0 EndX=82 EndY=-18 EndZ=0
    g17: LineSegment StartX=82 StartY=-18 StartZ=0 EndX=82 EndY=-52 EndZ=0
    g18: LineSegment StartX=82 StartY=-52 StartZ=0 EndX=48 EndY=-52 EndZ=0
    g19: LineSegment StartX=48 StartY=-52 StartZ=0 EndX=48 EndY=-18 EndZ=0
    g20: GeomPoint X=65 Y=-35 Z=0
    g21: GeomPoint X=48 Y=-35 Z=0
    g22: GeomPoint X=116 Y=-18 Z=0
    g23: GeomPoint X=82 Y=-35 Z=0
    g24: GeomPoint X=65 Y=-52 Z=0
    g25: GeomPoint X=65 Y=-18 Z=0
  constraints (61):
    c: Coincident(g0,g1)
    c: Coincident(g1,g2)
    c: Coincident(g2,g3)
    c: Coincident(g3,g0)
    c: Horizontal(g0)
    c: Horizontal(g2)
    c: Vertical(g1)
    c: Vertical(g3)
    c: Coincident(g4,g5)
    c: Coincident(g5,g6)
    c: Coincident(g6,g7)
    c: Coincident(g7,g4)
    c: Horizontal(g4)
    c: Horizontal(g6)
    c: Vertical(g5)
    c: Vertical(g7)
    c: Coincident(g8,g9)
    c: Coincident(g9,g10)
    c: Coincident(g10,g11)
    c: Coincident(g11,g8)
    c: Horizontal(g8)
    c: Horizontal(g10)
    c: Vertical(g9)
    c: Vertical(g11)
    c: Coincident(g12,g13)
    c: Coincident(g13,g14)
    c: Coincident(g14,g15)
    c: Coincident(g15,g12)
    c: Horizontal(g12)
    c: Horizontal(g14)
    c: Vertical(g13)
    c: Vertical(g15)
    c: Equal(g4,g1)
    c: Equal(g1,g8)
    c: Equal(g8,g13)
    c: Coincident(g16,g17)
    c: Coincident(g17,g18)
    c: Coincident(g18,g19)
    c: Coincident(g19,g16)
    c: DistanceX(g-4,g16) = 1
    c: DistanceY(g-4,g16) = 1
    c: Symmetric(g16,g18,g20)
    c: Symmetric(g-6,g-4,g20)
    c: DistanceY(g15,g15) = 7
    c: Vertical(g19)
    c: Horizontal(g16)
    c: PointOnObject(g12,g18)
    c: Vertical(g17)
    c: Equal(g0,g11)
    c: Equal(g11,g5)
    c: Equal(g5,g14)
    c: DistanceY(g11,g11) = 30
    c: Symmetric(g18,g17,g24)
    c: Symmetric(g6,g4,g23)
    c: Symmetric(g16,g22,g16)
    c: Symmetric(g16,g18,g21)
    c: Symmetric(g8,g9,g21)
    c: Symmetric(g17,g16,g23)
    c: Symmetric(g12,g12,g24)
    c: Symmetric(g2,g1,g25)
    c: Symmetric(g16,g16,g25)
FEATURE [PartDesign::Pocket] Pocket015  label="Ausschnitte  Touch002"
  BaseFeature = -> Pad011
  Direction = (0,0,1)
  Length = 3.5
  Length2 = 100
  Profile = -> Sketch040
  Type = 0
FEATURE [Sketcher::SketchObject] Sketch044
  ExternalGeometry = -> [Pocket015,Sketch041]
  FullyConstrained = true
  MapMode = 5
  Placement = pos=(0,0,19) rot=(1,0,0;3.14159rad)
  Support = -> [Pocket015]
  sketch-geometry (5):
    g0: Circle CenterX=51.5 CenterY=-69 CenterZ=0 NormalX=0 NormalY=0 NormalZ=1 AngleXU=0 Radius=1.35
    g1: Circle CenterX=78.5 CenterY=-69 CenterZ=0 NormalX=0 NormalY=0 NormalZ=1 AngleXU=0 Radius=1.35
    g2: LineSegment StartX=51.5 StartY=-69 StartZ=0 EndX=78.5 EndY=-69 EndZ=0
    g3: LineSegment StartX=65 StartY=-71 StartZ=0 EndX=65 EndY=-67 EndZ=0
    g4: GeomPoint X=65 Y=-69 Z=0
  constraints (11):
    c: Coincident(g2,g0)
    c: Coincident(g2,g1)
    c: Horizontal(g2)
    c: Equal(g1,g0)
    c: Diameter(g0) = 2.7
    c: DistanceX(g2,g2) = 27
    c: Vertical(g3)
    c: Symmetric(g0,g1,g4)
    c: Symmetric(g3,g3,g4)
    c: Symmetric(g-5,g-5,g3)
    c: PointOnObject(g3,g-6)
FEATURE [PartDesign::Pad] Pad012  label="Halter LED Strip002"
  BaseFeature = -> Pocket015
  Direction = (0,0,-1)
  Length = 5
  Length2 = 10
  Profile = -> Sketch044
  ReferenceAxis = -> Sketch044 [N_Axis]
  Type = 0
FEATURE [PartDesign::Fillet] Fillet002
  Base = -> Pad012 [Edge3,Edge19,Edge1,Edge6]
  BaseFeature = -> Pad012
  Radius = 7.5
  SupportTransform = false
FEATURE [Sketcher::SketchObject] Sketch045
  ExternalGeometry = -> [Fillet002]
  FullyConstrained = true
  MapMode = 5
  Placement = pos=(0,0,0) rot=(1,0,0;3.14159rad)
  Support = -> [Fillet002]
  sketch-geometry (17):
    g0: LineSegment StartX=6.65146 StartY=-6.65148 StartZ=0 EndX=123.349 EndY=-6.65148 EndZ=0
    g1: LineSegment StartX=123.349 StartY=-6.65148 StartZ=0 EndX=123.349 EndY=-78.3485 EndZ=0
    g2: LineSegment StartX=123.349 StartY=-78.3485 StartZ=0 EndX=6.65146 EndY=-78.3485 EndZ=0
    g3: LineSegment StartX=6.65146 StartY=-78.3485 StartZ=0 EndX=6.65146 EndY=-6.65148 EndZ=0
    g4: GeomPoint X=65 Y=-42.5 Z=0
    g5: Circle CenterX=123.349 CenterY=-6.65148 CenterZ=0 NormalX=0 NormalY=0 NormalZ=1 AngleXU=0 Radius=2.8
    g6: Circle CenterX=123.349 CenterY=-78.3485 CenterZ=0 NormalX=0 NormalY=0 NormalZ=1 AngleXU=0 Radius=2.8
    g7: Circle CenterX=6.65146 CenterY=-78.3485 CenterZ=0 NormalX=0 NormalY=0 NormalZ=1 AngleXU=0 Radius=2.8
    g8: Circle CenterX=6.65146 CenterY=-6.65148 CenterZ=0 NormalX=0 NormalY=0 NormalZ=1 AngleXU=0 Radius=2.8
    g9: LineSegment StartX=3.85146 StartY=-5.49168 StartZ=0 EndX=3.85146 EndY=-6.65148 EndZ=0
    g10: LineSegment StartX=3.85146 StartY=-5.49168 StartZ=0 EndX=9.34315 EndY=0 EndZ=0
    g11: LineSegment StartX=0 StartY=-4.3934 StartZ=0 EndX=4.3934 EndY=0 EndZ=0
    g12: LineSegment StartX=4.67157 StartY=-4.67157 StartZ=0 EndX=2.1967 EndY=-2.1967 EndZ=0
    g13: GeomPoint X=4.67157 Y=-4.67157 Z=0
    g14: GeomPoint X=2.1967 Y=-2.1967 Z=0
    g15: LineSegment StartX=11.0711 StartY=-11.0711 StartZ=0 EndX=22.1421 EndY=0 EndZ=0
    g16: LineSegment StartX=8.63137 StartY=-8.63137 StartZ=0 EndX=17.2627 EndY=0 EndZ=0
  constraints (45):
    c: Coincident(g0,g1)
    c: Coincident(g1,g2)
    c: Coincident(g2,g3)
    c: Coincident(g3,g0)
    c: Horizontal(g0)
    c: Horizontal(g2)
    c: Vertical(g1)
    c: Vertical(g3)
    c: Symmetric(g-3,g-4,g4)
    c: Symmetric(g2,g0,g4)
    c: Coincident(g5,g0)
    c: Coincident(g6,g1)
    c: Coincident(g7,g2)
    c: Diameter(g7) = 5.6
    c: Coincident(g8,g0)
    c: Equal(g5,g6)
    c: Equal(g6,g7)
    c: Equal(g7,g8)
    c: Vertical(g9)
    c: DistanceX(g-4,g9) = 3.85146
    c: Coincident(g10,g9)
    c: PointOnObject(g11,g-1)
    c: Parallel(g10,g11)
    c: Tangent(g-5,g11)
    c: Angle(g9,g10) = 2.35619
    c: PointOnObject(g11,g-2)
    c: Tangent(g10,g8)
    c: PointOnObject(g12,g10)
    c: PointOnObject(g12,g11)
    c: Perpendicular(g10,g12)
    c: Distance(g12) = 3.5
    c: PointOnObject(g10,g-1)
    c: PointOnObject(g13,g8)
    c: Coincident(g13,g12)
    c: PointOnObject(g14,g-5)
    c: Coincident(g12,g14)
    c: Tangent(g9,g8) = -1.5708
    c: PointOnObject(g15,g-1)
    c: Parallel(g15,g10)
    c: PointOnObject(g16,g8)
    c: PointOnObject(g16,g-1)
    c: Tangent(g16,g8)
    c: Parallel(g15,g16)
    c: Distance(g16,g15) = 3.45025
    c: Tangent(g15,g-6) = -1.5708
FEATURE [PartDesign::Pocket] Pocket020
  BaseFeature = -> Fillet002
  Direction = (0,0,1)
  Length = 10
  Length2 = 5
  Profile = -> Sketch045
  ReferenceAxis = -> Sketch045 [N_Axis]
  Type = 0
FEATURE [PartDesign::ShapeBinder] ShapeBinder002
  Support = -> [Pocket020]
  TraceSupport = true
FEATURE [Sketcher::SketchObject] Sketch046
  ExternalGeometry = -> [ShapeBinder002]
  FullyConstrained = true
  MapMode = 5
  Placement = pos=(0,0,0) rot=(1,0,0;3.14159rad)
  Support = -> [ShapeBinder002]
  sketch-geometry (23):
    g0: GeomPoint X=5 Y=-5 Z=0
    g1: GeomPoint X=125 Y=-80 Z=0
    g2: GeomPoint X=65 Y=-42.5 Z=0
    g3: ArcOfCircle CenterX=5 CenterY=-80 CenterZ=0 NormalX=0 NormalY=0 NormalZ=1 AngleXU=0 Radius=10 StartAngle=0.167448 EndAngle=1.40335
    g4: ArcOfCircle CenterX=7 CenterY=-68.1678 CenterZ=0 NormalX=0 NormalY=0 NormalZ=1 AngleXU=0 Radius=2 StartAngle=3.14159 EndAngle=4.54494
    g5: ArcOfCircle CenterX=5 CenterY=-5 CenterZ=0 NormalX=0 NormalY=0 NormalZ=1 AngleXU=0 Radius=10 StartAngle=4.87984 EndAngle=6.11574
    g6: ArcOfCircle CenterX=125 CenterY=-5 CenterZ=0 NormalX=0 NormalY=0 NormalZ=1 AngleXU=0 Radius=10 StartAngle=3.30904 EndAngle=4.54494
    g7: ArcOfCircle CenterX=125 CenterY=-80 CenterZ=0 NormalX=0 NormalY=0 NormalZ=1 AngleXU=0 Radius=10 StartAngle=1.73824 EndAngle=2.97414
    g8: LineSegment StartX=5 StartY=-80 StartZ=0 EndX=125 EndY=-80 EndZ=0
    g9: LineSegment StartX=125 StartY=-80 StartZ=0 EndX=125 EndY=-5 EndZ=0
    g10: LineSegment StartX=5 StartY=-5 StartZ=0 EndX=5 EndY=-80 EndZ=0
    g11: ArcOfCircle CenterX=7 CenterY=-16.8322 CenterZ=0 NormalX=0 NormalY=0 NormalZ=1 AngleXU=0 Radius=2 StartAngle=1.73824 EndAngle=3.14159
    g12: ArcOfCircle CenterX=123 CenterY=-16.8322 CenterZ=0 NormalX=0 NormalY=0 NormalZ=1 AngleXU=0 Radius=2 StartAngle=9e-16 EndAngle=1.40335
    g13: ArcOfCircle CenterX=16.8322 CenterY=-7 CenterZ=0 NormalX=0 NormalY=0 NormalZ=1 AngleXU=0 Radius=2 StartAngle=1.5708 EndAngle=2.97414
    g14: ArcOfCircle CenterX=113.168 CenterY=-7 CenterZ=0 NormalX=0 NormalY=0 NormalZ=1 AngleXU=0 Radius=2 StartAngle=0.167448 EndAngle=1.5708
    g15: ArcOfCircle CenterX=123 CenterY=-68.1678 CenterZ=0 NormalX=0 NormalY=0 NormalZ=1 AngleXU=0 Radius=2 StartAngle=4.87984 EndAngle=6.28319
    g16: ArcOfCircle CenterX=113.168 CenterY=-78 CenterZ=0 NormalX=0 NormalY=0 NormalZ=1 AngleXU=0 Radius=2 StartAngle=4.71239 EndAngle=6.11574
    g17: ArcOfCircle CenterX=16.8322 CenterY=-78 CenterZ=0 NormalX=0 NormalY=0 NormalZ=1 AngleXU=0 Radius=2 StartAngle=3.30904 EndAngle=4.71239
    g18: LineSegment StartX=5 StartY=-5 StartZ=0 EndX=125 EndY=-5 EndZ=0
    g19: LineSegment StartX=5 StartY=-16.8322 StartZ=0 EndX=5 EndY=-68.1678 EndZ=0
    g20: LineSegment StartX=125 StartY=-68.1678 StartZ=0 EndX=125 EndY=-16.8322 EndZ=0
    g21: LineSegment StartX=113.168 StartY=-5 StartZ=0 EndX=16.8322 EndY=-5 EndZ=0
    g22: LineSegment StartX=16.8322 StartY=-80 StartZ=0 EndX=113.168 EndY=-80 EndZ=0
  constraints (54):
    c: Tangent(g3,g4) = 1.5708
    c: Coincident(g7,g1)
    c: Coincident(g8,g9)
    c: Coincident(g10,g8)
    c: Horizontal(g8)
    c: Vertical(g9)
    c: Vertical(g10)
    c: Coincident(g8,g3)
    c: Coincident(g9,g6)
    c: Coincident(g0,g5)
    c: Symmetric(g3,g6,g2)
    c: Tangent(g5,g11) = 1.5708
    c: Tangent(g6,g12) = 1.5708
    c: Tangent(g5,g13) = 1.5708
    c: Tangent(g6,g14) = 1.5708
    c: Tangent(g7,g15) = 1.5708
    c: Tangent(g7,g16) = 1.5708
    c: Equal(g3,g5)
    c: Equal(g5,g6)
    c: Equal(g6,g7)
    c: Radius(g3) = 10
    c: Equal(g4,g13)
    c: Equal(g13,g11)
    c: Equal(g11,g14)
    c: Equal(g12,g15)
    c: Tangent(g16,g8) = -1.5708
    c: Tangent(g4,g10) = -1.5708
    c: Coincident(g8,g7)
    c: Tangent(g17,g8) = -1.5708
    c: Tangent(g17,g3) = 1.5708
    c: Radius(g17) = 2
    c: Tangent(g12,g9) = -1.5708
    c: Tangent(g15,g9) = -1.5708
    c: Tangent(g11,g10) = -1.5708
    c: Coincident(g18,g5)
    c: Horizontal(g18)
    c: Coincident(g18,g6)
    c: Coincident(g10,g5)
    c: Tangent(g13,g18) = 1.5708
    c: Tangent(g14,g18) = 1.5708
    c: Equal(g11,g12)
    c: Equal(g14,g17)
    c: Equal(g17,g16)
    c: Symmetric(g-3,g-5,g2)
    c: Coincident(g19,g11)
    c: Coincident(g19,g4)
    c: Coincident(g20,g15)
    c: Coincident(g20,g12)
    c: Coincident(g21,g14)
    c: Coincident(g21,g13)
    c: DistanceY(g5,g-4) = 1
    c: DistanceX(g-5,g11) = 1
    c: Coincident(g22,g17)
    c: Coincident(g22,g16)
FEATURE [Sketcher::SketchObject] Sketch047
  ExternalGeometry = -> [ShapeBinder002]
  FullyConstrained = true
  MapMode = 5
  Placement = pos=(0,0,0) rot=(1,0,0;3.14159rad)
  Support = -> [ShapeBinder002]
  sketch-geometry (12):
    g0: LineSegment StartX=7.5 StartY=0 StartZ=0 EndX=122.5 EndY=0 EndZ=0
    g1: LineSegment StartX=130 StartY=-7.5 StartZ=0 EndX=130 EndY=-77.5 EndZ=0
    g2: LineSegment StartX=122.5 StartY=-85 StartZ=0 EndX=7.5 EndY=-85 EndZ=0
    g3: LineSegment StartX=0 StartY=-77.5 StartZ=0 EndX=0 EndY=-7.5 EndZ=0
    g4: ArcOfCircle CenterX=7.5 CenterY=-7.5 CenterZ=0 NormalX=0 NormalY=0 NormalZ=1 AngleXU=0 Radius=7.5 StartAngle=1.5708 EndAngle=3.14159
    g5: GeomPoint X=0 Y=0 Z=0
    g6: ArcOfCircle CenterX=122.5 CenterY=-7.5 CenterZ=0 NormalX=0 NormalY=0 NormalZ=1 AngleXU=0 Radius=7.5 StartAngle=0 EndAngle=1.5708
    g7: GeomPoint X=130 Y=0 Z=0
    g8: ArcOfCircle CenterX=122.5 CenterY=-77.5 CenterZ=0 NormalX=0 NormalY=0 NormalZ=1 AngleXU=0 Radius=7.5 StartAngle=4.71239 EndAngle=6.28319
    g9: GeomPoint X=130 Y=-85 Z=0
    g10: ArcOfCircle CenterX=7.5 CenterY=-77.5 CenterZ=0 NormalX=0 NormalY=0 NormalZ=1 AngleXU=0 Radius=7.5 StartAngle=3.14159 EndAngle=4.71239
    g11: GeomPoint X=0 Y=-85 Z=0
  constraints (23):
    c: Horizontal(g0)
    c: Vertical(g1)
    c: Vertical(g3)
    c: Coincident(g5,g-1)
    c: PointOnObject(g5,g3)
    c: Tangent(g0,g4) = 1.5708
    c: Tangent(g3,g4) = 1.5708
    c: PointOnObject(g7,g1)
    c: PointOnObject(g7,g0)
    c: Tangent(g1,g6) = 1.5708
    c: Tangent(g0,g6) = 1.5708
    c: PointOnObject(g9,g1)
    c: PointOnObject(g9,g2)
    c: Tangent(g1,g8) = 1.5708
    c: Tangent(g2,g8) = 1.5708
    c: PointOnObject(g11,g2)
    c: PointOnObject(g11,g3)
    c: Tangent(g2,g10) = 1.5708
    c: Tangent(g3,g10) = 1.5708
    c: Coincident(g2,g-4)
    c: Coincident(g2,g-4)
    c: Coincident(g-3,g1)
    c: Coincident(g0,g-5)
FEATURE [PartDesign::Pad] Pad013
  Direction = (0,0,-1)
  Length = 10
  Length2 = 10
  Profile = -> Sketch047
  ReferenceAxis = -> Sketch047 [N_Axis]
  Type = 0
FEATURE [PartDesign::Pocket] Pocket021
  BaseFeature = -> Pad013
  Direction = (0,0,1)
  Length = 7
  Length2 = 5
  Profile = -> Sketch046
  ReferenceAxis = -> Sketch046 [N_Axis]
  Reversed = true
  Type = 0
FEATURE [Sketcher::SketchObject] Sketch048
  ExternalGeometry = -> [ShapeBinder002]
  FullyConstrained = true
  MapMode = 5
  Placement = pos=(0,0,-10) rot=(1,0,0;3.14159rad)
  Support = -> [Pocket021]
  sketch-geometry (4):
    g0: Circle CenterX=6.65146 CenterY=-6.65148 CenterZ=0 NormalX=0 NormalY=0 NormalZ=1 AngleXU=0 Radius=2.8
    g1: Circle CenterX=123.349 CenterY=-6.65148 CenterZ=0 NormalX=0 NormalY=0 NormalZ=1 AngleXU=0 Radius=2.8
    g2: Circle CenterX=123.349 CenterY=-78.3485 CenterZ=0 NormalX=0 NormalY=0 NormalZ=1 AngleXU=0 Radius=2.8
    g3: Circle CenterX=6.65146 CenterY=-78.3485 CenterZ=0 NormalX=0 NormalY=0 NormalZ=1 AngleXU=0 Radius=2.8
  constraints (8):
    c: Coincident(g1,g-4)
    c: Coincident(g2,g-5)
    c: Coincident(g3,g-6)
    c: Coincident(g0,g-3)
    c: Equal(g0,g-3)
    c: Equal(g0,g1)
    c: Equal(g1,g2)
    c: Equal(g2,g3)
FEATURE [PartDesign::Hole] Hole006
  BaseFeature = -> Pocket021
  CustomThreadClearance = 0
  Depth = 314.401
  DepthType = 1
  Diameter = 4.5
  DrillForDepth = false
  DrillPoint = 1
  DrillPointAngle = 118
  HoleCutCountersinkAngle = 90
  HoleCutCustomValues = false
  HoleCutDepth = 5.2
  HoleCutDiameter = 10
  HoleCutType = 12
  ModelThread = false
  Profile = -> Sketch048
  Tapered = false
  TaperedAngle = 90
  ThreadClass = 0
  ThreadDepth = 314.401
  ThreadDepthType = 0
  ThreadDirection = 0
  ThreadFit = 0
  ThreadSize = 11
  ThreadType = 1
  Threaded = false
  UseCustomThreadClearance = false
FEATURE [Sketcher::SketchObject] Sketch049
  ExternalGeometry = -> [ShapeBinder002]
  FullyConstrained = true
  MapMode = 5
  Placement = pos=(0,0,0) rot=(1,0,0;3.14159rad)
  Support = -> [ShapeBinder002]
  sketch-geometry (46):
    g0: GeomPoint X=5 Y=-5 Z=0
    g1: GeomPoint X=125 Y=-80 Z=0
    g2: GeomPoint X=65 Y=-42.5 Z=0
    g3: ArcOfCircle CenterX=5 CenterY=-80 CenterZ=0 NormalX=0 NormalY=0 NormalZ=1 AngleXU=0 Radius=10 StartAngle=0.167448 EndAngle=1.40335
    g4: ArcOfCircle CenterX=7 CenterY=-68.1678 CenterZ=0 NormalX=0 NormalY=0 NormalZ=1 AngleXU=0 Radius=2 StartAngle=3.14159 EndAngle=4.54494
    g5: ArcOfCircle CenterX=5 CenterY=-5 CenterZ=0 NormalX=0 NormalY=0 NormalZ=1 AngleXU=0 Radius=10 StartAngle=4.87984 EndAngle=6.11574
    g6: ArcOfCircle CenterX=125 CenterY=-5 CenterZ=0 NormalX=0 NormalY=0 NormalZ=1 AngleXU=0 Radius=10 StartAngle=3.30904 EndAngle=4.54494
    g7: ArcOfCircle CenterX=125 CenterY=-80 CenterZ=0 NormalX=0 NormalY=0 NormalZ=1 AngleXU=0 Radius=10 StartAngle=1.73824 EndAngle=2.97414
    g8: LineSegment StartX=5 StartY=-80 StartZ=0 EndX=125 EndY=-80 EndZ=0
    g9: LineSegment StartX=125 StartY=-80 StartZ=0 EndX=125 EndY=-5 EndZ=0
    g10: LineSegment StartX=5 StartY=-5 StartZ=0 EndX=5 EndY=-80 EndZ=0
    g11: ArcOfCircle CenterX=7 CenterY=-16.8322 CenterZ=0 NormalX=0 NormalY=0 NormalZ=1 AngleXU=0 Radius=2 StartAngle=1.73824 EndAngle=3.14159
    g12: ArcOfCircle CenterX=123 CenterY=-16.8322 CenterZ=0 NormalX=0 NormalY=0 NormalZ=1 AngleXU=0 Radius=2 StartAngle=-9e-16 EndAngle=1.40335
    g13: ArcOfCircle CenterX=16.8322 CenterY=-7 CenterZ=0 NormalX=0 NormalY=0 NormalZ=1 AngleXU=0 Radius=2 StartAngle=1.5708 EndAngle=2.97414
    g14: ArcOfCircle CenterX=113.168 CenterY=-7 CenterZ=0 NormalX=0 NormalY=0 NormalZ=1 AngleXU=0 Radius=2 StartAngle=0.167448 EndAngle=1.5708
    g15: ArcOfCircle CenterX=123 CenterY=-68.1678 CenterZ=0 NormalX=0 NormalY=0 NormalZ=1 AngleXU=0 Radius=2 StartAngle=4.87984 EndAngle=6.28319
    g16: ArcOfCircle CenterX=113.168 CenterY=-78 CenterZ=0 NormalX=0 NormalY=0 NormalZ=1 AngleXU=0 Radius=2 StartAngle=4.71239 EndAngle=6.11574
    g17: ArcOfCircle CenterX=16.8322 CenterY=-78 CenterZ=0 NormalX=0 NormalY=0 NormalZ=1 AngleXU=0 Radius=2 StartAngle=3.30904 EndAngle=4.71239
    g18: LineSegment StartX=5 StartY=-5 StartZ=0 EndX=125 EndY=-5 EndZ=0
    g19: LineSegment StartX=5 StartY=-16.8322 StartZ=0 EndX=5 EndY=-68.1678 EndZ=0
    g20: LineSegment StartX=125 StartY=-68.1678 StartZ=0 EndX=125 EndY=-16.8322 EndZ=0
    g21: LineSegment StartX=113.168 StartY=-5 StartZ=0 EndX=16.8322 EndY=-5 EndZ=0
    g22: LineSegment StartX=16.8322 StartY=-80 StartZ=0 EndX=113.168 EndY=-80 EndZ=0
    g23: GeomPoint X=4 Y=-4 Z=0
    g24: GeomPoint X=126 Y=-81 Z=0
    g25: GeomPoint X=65 Y=-42.5 Z=0
    g26: ArcOfCircle CenterX=4 CenterY=-81 CenterZ=0 NormalX=0 NormalY=0 NormalZ=1 AngleXU=0 Radius=10 StartAngle=0.167448 EndAngle=1.40335
    g27: ArcOfCircle CenterX=6 CenterY=-69.1678 CenterZ=0 NormalX=0 NormalY=0 NormalZ=1 AngleXU=0 Radius=2 StartAngle=3.14159 EndAngle=4.54494
    g28: ArcOfCircle CenterX=4 CenterY=-4 CenterZ=0 NormalX=0 NormalY=0 NormalZ=1 AngleXU=0 Radius=10 StartAngle=4.87984 EndAngle=6.11574
    g29: ArcOfCircle CenterX=126 CenterY=-4 CenterZ=0 NormalX=0 NormalY=0 NormalZ=1 AngleXU=0 Radius=10 StartAngle=3.30904 EndAngle=4.54494
    g30: ArcOfCircle CenterX=126 CenterY=-81 CenterZ=0 NormalX=0 NormalY=0 NormalZ=1 AngleXU=0 Radius=10 StartAngle=1.73824 EndAngle=2.97414
    g31: LineSegment StartX=4 StartY=-81 StartZ=0 EndX=126 EndY=-81 EndZ=0
    g32: LineSegment StartX=126 StartY=-81 StartZ=0 EndX=126 EndY=-4 EndZ=0
    g33: LineSegment StartX=4 StartY=-4 StartZ=0 EndX=4 EndY=-81 EndZ=0
    g34: ArcOfCircle CenterX=6 CenterY=-15.8322 CenterZ=0 NormalX=0 NormalY=0 NormalZ=1 AngleXU=0 Radius=2 StartAngle=1.73824 EndAngle=3.14159
    g35: ArcOfCircle CenterX=124 CenterY=-15.8322 CenterZ=0 NormalX=0 NormalY=0 NormalZ=1 AngleXU=0 Radius=2 StartAngle=3e-16 EndAngle=1.40335
    g36: ArcOfCircle CenterX=15.8322 CenterY=-6 CenterZ=0 NormalX=0 NormalY=0 NormalZ=1 AngleXU=0 Radius=2 StartAngle=1.5708 EndAngle=2.97414
    g37: ArcOfCircle CenterX=114.168 CenterY=-6 CenterZ=0 NormalX=0 NormalY=0 NormalZ=1 AngleXU=0 Radius=2 StartAngle=0.167448 EndAngle=1.5708
    g38: ArcOfCircle CenterX=124 CenterY=-69.1678 CenterZ=0 NormalX=0 NormalY=0 NormalZ=1 AngleXU=0 Radius=2 StartAngle=4.87984 EndAngle=6.28319
    g39: ArcOfCircle CenterX=114.168 CenterY=-79 CenterZ=0 NormalX=0 NormalY=0 NormalZ=1 AngleXU=0 Radius=2 StartAngle=4.71239 EndAngle=6.11574
    g40: ArcOfCircle CenterX=15.8322 CenterY=-79 CenterZ=0 NormalX=0 NormalY=0 NormalZ=1 AngleXU=0 Radius=2 StartAngle=3.30904 EndAngle=4.71239
    g41: LineSegment StartX=4 StartY=-4 StartZ=0 EndX=126 EndY=-4 EndZ=0
    g42: LineSegment StartX=4 StartY=-15.8322 StartZ=0 EndX=4 EndY=-69.1678 EndZ=0
    g43: LineSegment StartX=126 StartY=-69.1678 StartZ=0 EndX=126 EndY=-15.8322 EndZ=0
    g44: LineSegment StartX=114.168 StartY=-4 StartZ=0 EndX=15.8322 EndY=-4 EndZ=0
    g45: LineSegment StartX=15.8322 StartY=-81 StartZ=0 EndX=114.168 EndY=-81 EndZ=0
  constraints (107):
    c: Tangent(g3,g4) = 1.5708
    c: Coincident(g7,g1)
    c: Coincident(g8,g9)
    c: Coincident(g10,g8)
    c: Horizontal(g8)
    c: Vertical(g9)
    c: Vertical(g10)
    c: Coincident(g8,g3)
    c: Coincident(g9,g6)
    c: Coincident(g0,g5)
    c: Symmetric(g3,g6,g2)
    c: Tangent(g5,g11) = 1.5708
    c: Tangent(g6,g12) = 1.5708
    c: Tangent(g5,g13) = 1.5708
    c: Tangent(g6,g14) = 1.5708
    c: Tangent(g7,g15) = 1.5708
    c: Tangent(g7,g16) = 1.5708
    c: Equal(g3,g5)
    c: Equal(g5,g6)
    c: Equal(g6,g7)
    c: Radius(g3) = 10
    c: Equal(g4,g13)
    c: Equal(g13,g11)
    c: Equal(g11,g14)
    c: Equal(g12,g15)
    c: Tangent(g16,g8) = -1.5708
    c: Tangent(g4,g10) = -1.5708
    c: Coincident(g8,g7)
    c: Tangent(g17,g8) = -1.5708
    c: Tangent(g17,g3) = 1.5708
    c: Radius(g17) = 2
    c: Tangent(g12,g9) = -1.5708
    c: Tangent(g15,g9) = -1.5708
    c: Tangent(g11,g10) = -1.5708
    c: Coincident(g18,g5)
    c: Horizontal(g18)
    c: Coincident(g18,g6)
    c: Coincident(g10,g5)
    c: Tangent(g13,g18) = 1.5708
    c: Tangent(g14,g18) = 1.5708
    c: Equal(g11,g12)
    c: Equal(g14,g17)
    c: Equal(g17,g16)
    c: Coincident(g19,g11)
    c: Coincident(g19,g4)
    c: Coincident(g20,g15)
    c: Coincident(g20,g12)
    c: Coincident(g21,g14)
    c: Coincident(g21,g13)
    c: Coincident(g22,g17)
    c: Coincident(g22,g16)
    c: Tangent(g26,g27) = 1.5708
    c: Coincident(g30,g24)
    c: Coincident(g31,g32)
    c: Coincident(g33,g31)
    c: Horizontal(g31)
    c: Vertical(g32)
    c: Vertical(g33)
    c: Coincident(g31,g26)
    c: Coincident(g32,g29)
    c: Coincident(g23,g28)
    c: Symmetric(g26,g29,g25)
    c: Tangent(g28,g34) = 1.5708
    c: Tangent(g29,g35) = 1.5708
    c: Tangent(g28,g36) = 1.5708
    c: Tangent(g29,g37) = 1.5708
    c: Tangent(g30,g38) = 1.5708
    c: Tangent(g30,g39) = 1.5708
    c: Equal(g26,g28)
    c: Equal(g28,g29)
    c: Equal(g29,g30)
    c: Radius(g26) = 10
    c: Equal(g27,g36)
    c: Equal(g36,g34)
    c: Equal(g34,g37)
    c: Equal(g35,g38)
    c: Tangent(g39,g31) = -1.5708
    c: Tangent(g27,g33) = -1.5708
    c: Coincident(g31,g30)
    c: Tangent(g40,g31) = -1.5708
    c: Tangent(g40,g26) = 1.5708
    c: Radius(g40) = 2
    c: Tangent(g35,g32) = -1.5708
    c: Tangent(g38,g32) = -1.5708
    c: Tangent(g34,g33) = -1.5708
    c: Coincident(g41,g28)
    c: Horizontal(g41)
    c: Coincident(g41,g29)
    c: Coincident(g33,g28)
    c: Tangent(g36,g41) = 1.5708
    c: Tangent(g37,g41) = 1.5708
    c: Equal(g34,g35)
    c: Equal(g37,g40)
    c: Equal(g40,g39)
    c: Coincident(g42,g34)
    c: Coincident(g42,g27)
    c: Coincident(g43,g38)
    c: Coincident(g43,g35)
    c: Coincident(g44,g37)
    c: Coincident(g44,g36)
    c: Coincident(g45,g40)
    c: Coincident(g45,g39)
    c: Symmetric(g28,g30,g2)
    c: Coincident(g34,g-3)
    c: Coincident(g38,g-4)
    c: DistanceX(g27,g4) = 1
    c: DistanceY(g40,g17) = 1
FEATURE [PartDesign::Pad] Pad014
  BaseFeature = -> Hole006
  Direction = (0,0,-1)
  Length = 10
  Length2 = 10
  Profile = -> Sketch049
  ReferenceAxis = -> Sketch049 [N_Axis]
  Reversed = true
  Type = 0
FEATURE [PartDesign::Line] HoleAxis_008
  AttacherType = Attacher::AttachEngineLine
  Length = 4.79083
  MapMode = 19
  Placement = pos=(123.349,78.3485,-4.8) rot=(0,1,0;3.14159rad)
  ResizeMode = 1
  Support = -> [Pad014]
FEATURE [PartDesign::Line] HoleAxis_009
  AttacherType = Attacher::AttachEngineLine
  Length = 4.79083
  MapMode = 19
  Placement = pos=(6.65146,6.65148,-4.8) rot=(0,1,0;3.14159rad)
  ResizeMode = 1
  Support = -> [Pad014]
FEATURE [Sketcher::SketchObject] Sketch052
  ExternalGeometry = -> [Pad014]
  FullyConstrained = true
  MapMode = 5
  Placement = pos=(0,0,-7) rot=(0,0,1;0rad)
  Support = -> [Pad014]
  sketch-geometry (3):
    g0: Circle CenterX=65 CenterY=20 CenterZ=0 NormalX=0 NormalY=0 NormalZ=1 AngleXU=0 Radius=6
    g1: GeomPoint X=65 Y=0 Z=0
    g2: LineSegment StartX=65 StartY=0 StartZ=0 EndX=65 EndY=20 EndZ=0
  constraints (6):
    c: Diameter(g0) = 12
    c: Symmetric(g-3,g-3,g1)
    c: Coincident(g2,g1)
    c: Coincident(g2,g0)
    c: Vertical(g2)
    c: DistanceY(g2,g2) = 20
FEATURE [PartDesign::Hole] Hole008
  BaseFeature = -> Pad014
  CustomThreadClearance = 0
  Depth = 25
  DepthType = 0
  Diameter = 12.1
  DrillForDepth = false
  DrillPoint = 1
  DrillPointAngle = 118
  HoleCutCountersinkAngle = 90
  HoleCutCustomValues = false
  HoleCutDepth = 0
  HoleCutDiameter = 13.6
  HoleCutType = 0
  ModelThread = false
  Profile = -> Sketch052
  Refine = true
  Tapered = false
  TaperedAngle = 90
  ThreadClass = 0
  ThreadDepth = 25
  ThreadDepthType = 0
  ThreadDirection = 0
  ThreadFit = 0
  ThreadSize = 19
  ThreadType = 1
  Threaded = false
  UseCustomThreadClearance = false
FEATURE [Sketcher::SketchObject] Sketch053
  ExternalGeometry = -> [HoleAxis_008,HoleAxis_009]
  FullyConstrained = true
  MapMode = 5
  Placement = pos=(0,0,-7) rot=(0,0,1;0rad)
  Support = -> [Hole008]
  sketch-geometry (24):
    g0: ArcOfCircle CenterX=23.5 CenterY=46.5 CenterZ=0 NormalX=0 NormalY=0 NormalZ=1 AngleXU=0 Radius=2 StartAngle=1.5708 EndAngle=3.14159
    g1: LineSegment StartX=23.5 StartY=48.5 StartZ=0 EndX=31.5 EndY=48.5 EndZ=0
    g2: ArcOfCircle CenterX=31.5 CenterY=46.5 CenterZ=0 NormalX=0 NormalY=0 NormalZ=1 AngleXU=0 Radius=2 StartAngle=0 EndAngle=1.5708
    g3: LineSegment StartX=33.5 StartY=46.5 StartZ=0 EndX=33.5 EndY=38.5 EndZ=0
    g4: ArcOfCircle CenterX=31.5 CenterY=38.5 CenterZ=0 NormalX=0 NormalY=0 NormalZ=1 AngleXU=0 Radius=2 StartAngle=4.71239 EndAngle=6.28319
    g5: LineSegment StartX=31.5 StartY=36.5 StartZ=0 EndX=23.5 EndY=36.5 EndZ=0
    g6: ArcOfCircle CenterX=23.5 CenterY=38.5 CenterZ=0 NormalX=0 NormalY=0 NormalZ=1 AngleXU=0 Radius=2 StartAngle=3.14159 EndAngle=4.71239
    g7: LineSegment StartX=21.5 StartY=38.5 StartZ=0 EndX=21.5 EndY=46.5 EndZ=0
    g8: GeomPoint X=21.5 Y=48.5 Z=0
    g9: GeomPoint X=33.5 Y=36.5 Z=0
    g10: ArcOfCircle CenterX=98.5 CenterY=46.5 CenterZ=0 NormalX=0 NormalY=0 NormalZ=1 AngleXU=0 Radius=2 StartAngle=1.5708 EndAngle=3.14159
    g11: LineSegment StartX=98.5 StartY=48.5 StartZ=0 EndX=106.5 EndY=48.5 EndZ=0
    g12: ArcOfCircle CenterX=106.5 CenterY=46.5 CenterZ=0 NormalX=0 NormalY=0 NormalZ=1 AngleXU=0 Radius=2 StartAngle=6e-16 EndAngle=1.5708
    g13: LineSegment StartX=108.5 StartY=46.5 StartZ=0 EndX=108.5 EndY=38.5 EndZ=0
    g14: ArcOfCircle CenterX=106.5 CenterY=38.5 CenterZ=0 NormalX=0 NormalY=0 NormalZ=1 AngleXU=0 Radius=2 StartAngle=4.71239 EndAngle=6.28319
    g15: LineSegment StartX=106.5 StartY=36.5 StartZ=0 EndX=98.5 EndY=36.5 EndZ=0
    g16: ArcOfCircle CenterX=98.5 CenterY=38.5 CenterZ=0 NormalX=0 NormalY=0 NormalZ=1 AngleXU=0 Radius=2 StartAngle=3.14159 EndAngle=4.71239
    g17: LineSegment StartX=96.5 StartY=38.5 StartZ=0 EndX=96.5 EndY=46.5 EndZ=0
    g18: GeomPoint X=96.5 Y=48.5 Z=0
    g19: GeomPoint X=108.5 Y=36.5 Z=0
    g20: GeomPoint X=27.5 Y=42.5 Z=0
    g21: GeomPoint X=102.5 Y=42.5 Z=0
    g22: GeomPoint X=65 Y=42.5 Z=0
    g23: LineSegment StartX=27.5 StartY=42.5 StartZ=0 EndX=102.5 EndY=42.5 EndZ=0
  constraints (53):
    c: Tangent(g0,g1) = 1.5708
    c: Tangent(g1,g2) = 1.5708
    c: Tangent(g2,g3) = 1.5708
    c: Tangent(g3,g4) = 1.5708
    c: Tangent(g4,g5) = 1.5708
    c: Tangent(g5,g6) = 1.5708
    c: Tangent(g6,g7) = 1.5708
    c: Tangent(g7,g0) = 1.5708
    c: Horizontal(g1)
    c: Horizontal(g5)
    c: Vertical(g3)
    c: Vertical(g7)
    c: Equal(g2,g4)
    c: Equal(g4,g6)
    c: PointOnObject(g8,g1)
    c: PointOnObject(g8,g7)
    c: PointOnObject(g9,g3)
    c: PointOnObject(g9,g5)
    c: Tangent(g10,g11) = 1.5708
    c: Tangent(g11,g12) = 1.5708
    c: Tangent(g12,g13) = 1.5708
    c: Tangent(g13,g14) = 1.5708
    c: Tangent(g14,g15) = 1.5708
    c: Tangent(g15,g16) = 1.5708
    c: Tangent(g16,g17) = 1.5708
    c: Tangent(g17,g10) = 1.5708
    c: Horizontal(g11)
    c: Horizontal(g15)
    c: Vertical(g13)
    c: Vertical(g17)
    c: Equal(g10,g12)
    c: Equal(g12,g14)
    c: Equal(g14,g16)
    c: PointOnObject(g18,g11)
    c: PointOnObject(g18,g17)
    c: PointOnObject(g19,g13)
    c: PointOnObject(g19,g15)
    c: Symmetric(g16,g12,g21)
    c: Symmetric(g2,g6,g20)
    c: Equal(g1,g11)
    c: Equal(g3,g13)
    c: Symmetric(g-4,g-3,g22)
    c: Symmetric(g21,g20,g22)
    c: Coincident(g23,g20)
    c: Coincident(g23,g21)
    c: Horizontal(g23)
    c: Equal(g2,g0)
    c: Equal(g6,g16)
    c: Radius(g4) = 2
    c: DistanceX(g8,g9) = 12  'Breite Klickfixadapter'
    c: DistanceY(g9,g8) = 12
    c: DistanceX(g23,g23) = 75
    c: DistanceX(g8,g19) = 87
FEATURE [PartDesign::Pad] Pad015
  BaseFeature = -> Hole008
  Direction = (0,0,1)
  Length = 5
  Length2 = 10
  Profile = -> Sketch053
  ReferenceAxis = -> Sketch053 [N_Axis]
  Refine = true
  Type = 0
FEATURE [Sketcher::SketchObject] Sketch054
  ExternalGeometry = -> [Pad015]
  FullyConstrained = true
  MapMode = 5
  Placement = pos=(0,0,-10) rot=(1,0,0;3.14159rad)
  Support = -> [Pad015]
  sketch-geometry (22):
    g0: ArcOfCircle CenterX=24.5 CenterY=-39.5 CenterZ=0 NormalX=0 NormalY=0 NormalZ=1 AngleXU=0 Radius=2 StartAngle=1.5708 EndAngle=3.14159
    g1: LineSegment StartX=24.5 StartY=-37.5 StartZ=0 EndX=30.5 EndY=-37.5 EndZ=0
    g2: ArcOfCircle CenterX=30.5 CenterY=-39.5 CenterZ=0 NormalX=0 NormalY=0 NormalZ=1 AngleXU=0 Radius=2 StartAngle=-2.7e-15 EndAngle=1.5708
    g3: LineSegment StartX=32.5 StartY=-39.5 StartZ=0 EndX=32.5 EndY=-45.5 EndZ=0
    g4: ArcOfCircle CenterX=30.5 CenterY=-45.5 CenterZ=0 NormalX=0 NormalY=0 NormalZ=1 AngleXU=0 Radius=2 StartAngle=4.71239 EndAngle=6.28319
    g5: LineSegment StartX=30.5 StartY=-47.5 StartZ=0 EndX=24.5 EndY=-47.5 EndZ=0
    g6: ArcOfCircle CenterX=24.5 CenterY=-45.5 CenterZ=0 NormalX=0 NormalY=0 NormalZ=1 AngleXU=0 Radius=2 StartAngle=3.14159 EndAngle=4.71239
    g7: LineSegment StartX=22.5 StartY=-45.5 StartZ=0 EndX=22.5 EndY=-39.5 EndZ=0
    g8: GeomPoint X=22.5 Y=-37.5 Z=0
    g9: GeomPoint X=32.5 Y=-47.5 Z=0
    g10: ArcOfCircle CenterX=99.5 CenterY=-39.5 CenterZ=0 NormalX=0 NormalY=0 NormalZ=1 AngleXU=0 Radius=2 StartAngle=1.5708 EndAngle=3.14159
    g11: LineSegment StartX=99.5 StartY=-37.5 StartZ=0 EndX=105.5 EndY=-37.5 EndZ=0
    g12: ArcOfCircle CenterX=105.5 CenterY=-39.5 CenterZ=0 NormalX=0 NormalY=0 NormalZ=1 AngleXU=0 Radius=2 StartAngle=-7.1e-15 EndAngle=1.5708
    g13: LineSegment StartX=107.5 StartY=-39.5 StartZ=0 EndX=107.5 EndY=-45.5 EndZ=0
    g14: ArcOfCircle CenterX=105.5 CenterY=-45.5 CenterZ=0 NormalX=0 NormalY=0 NormalZ=1 AngleXU=0 Radius=2 StartAngle=4.71239 EndAngle=6.28319
    g15: LineSegment StartX=105.5 StartY=-47.5 StartZ=0 EndX=99.5 EndY=-47.5 EndZ=0
    g16: ArcOfCircle CenterX=99.5 CenterY=-45.5 CenterZ=0 NormalX=0 NormalY=0 NormalZ=1 AngleXU=0 Radius=2 StartAngle=3.14159 EndAngle=4.71239
    g17: LineSegment StartX=97.5 StartY=-45.5 StartZ=0 EndX=97.5 EndY=-39.5 EndZ=0
    g18: GeomPoint X=97.5 Y=-37.5 Z=0
    g19: GeomPoint X=107.5 Y=-47.5 Z=0
    g20: GeomPoint X=27.5 Y=-42.5 Z=0
    g21: GeomPoint X=102.5 Y=-42.5 Z=0
  constraints (49):
    c: Equal(g4,g6)
    c: PointOnObject(g8,g1)
    c: PointOnObject(g8,g7)
    c: PointOnObject(g9,g3)
    c: PointOnObject(g9,g5)
    c: Tangent(g10,g11) = 1.5708
    c: Tangent(g11,g12) = 1.5708
    c: Tangent(g12,g13) = 1.5708
    c: Tangent(g13,g14) = 1.5708
    c: Tangent(g14,g15) = 1.5708
    c: Tangent(g15,g16) = 1.5708
    c: Tangent(g16,g17) = 1.5708
    c: Tangent(g17,g10) = 1.5708
    c: Horizontal(g11)
    c: Horizontal(g15)
    c: Vertical(g13)
    c: Vertical(g17)
    c: Equal(g10,g12)
    c: Equal(g12,g14)
    c: Equal(g14,g16)
    c: PointOnObject(g18,g11)
    c: PointOnObject(g18,g17)
    c: PointOnObject(g19,g13)
    c: PointOnObject(g19,g15)
    c: Equal(g10,g4)
    c: Horizontal(g1)
    c: Vertical(g3)
    c: Vertical(g7)
    c: Horizontal(g5)
    c: Tangent(g6,g7) = 1.5708
    c: Tangent(g3,g4) = 1.5708
    c: Tangent(g1,g2) = 1.5708
    c: Tangent(g0,g7) = 1.5708
    c: Tangent(g0,g1) = 1.5708
    c: Tangent(g3,g2) = 1.5708
    c: Tangent(g5,g4) = 1.5708
    c: Tangent(g5,g6) = 1.5708
    c: Equal(g6,g0)
    c: Equal(g0,g2)
    c: Radius(g0) = 2
    c: DistanceX(g0,g2) = 10
    c: DistanceY(g4,g1) = 10
    c: Symmetric(g6,g2,g20)
    c: Symmetric(g-4,g-3,g20)
    c: Equal(g3,g13)
    c: Symmetric(g16,g12,g21)
    c: Symmetric(g-5,g-6,g21)
    c: Equal(g13,g11)
    c: DistanceX(g6,g13) = 85
FEATURE [PartDesign::Pocket] Pocket019
  BaseFeature = -> Pad015
  Direction = (0,0,1)
  Length = 3
  Length2 = 5
  Profile = -> Sketch054
  ReferenceAxis = -> Sketch054 [N_Axis]
  Refine = true
  Type = 0
FEATURE [Sketcher::SketchObject] Sketch050
  ExternalGeometry = -> [Pad015]
  FullyConstrained = true
  MapMode = 5
  Placement = pos=(0,0,-2) rot=(0,0,1;0rad)
  Support = -> [Pocket019]
  sketch-geometry (2):
    g0: Circle CenterX=27.5 CenterY=42.5 CenterZ=0 NormalX=0 NormalY=0 NormalZ=1 AngleXU=0 Radius=2
    g1: Circle CenterX=102.5 CenterY=42.5 CenterZ=0 NormalX=0 NormalY=0 NormalZ=1 AngleXU=0 Radius=2
  constraints (4):
    c: Equal(g0,g1)
    c: Symmetric(g-5,g-6,g0)
    c: Symmetric(g-4,g-3,g1)
    c: Diameter(g0) = 4
FEATURE [PartDesign::Hole] Hole007
  BaseFeature = -> Pocket019
  CustomThreadClearance = 0
  Depth = 8
  DepthType = 0
  Diameter = 4.5
  DrillForDepth = false
  DrillPoint = 1
  DrillPointAngle = 118
  HoleCutCountersinkAngle = 90
  HoleCutCustomValues = false
  HoleCutDepth = 3.2
  HoleCutDiameter = 8
  HoleCutType = 6
  ModelThread = false
  Profile = -> Sketch050
  Refine = true
  Tapered = false
  TaperedAngle = 90
  ThreadClass = 0
  ThreadDepth = 8
  ThreadDepthType = 0
  ThreadDirection = 0
  ThreadFit = 0
  ThreadSize = 11
  ThreadType = 1
  Threaded = false
  UseCustomThreadClearance = false
FEATURE [Sketcher::SketchObject] Sketch051  label="Stabilisierung - Pfad002"
  ExternalGeometry = -> [Hole007]
  FullyConstrained = true
  MapMode = 5
  Placement = pos=(0,0,-7) rot=(0,0,1;0rad)
  Support = -> [Hole007]
  sketch-geometry (13):
    g0: LineSegment StartX=14.6316 StartY=70.3684 StartZ=0 EndX=10.7634 EndY=74.2366 EndZ=0
    g1: LineSegment StartX=15.0973 StartY=69.6369 StartZ=0 EndX=22.9672 EndY=47.9672 EndZ=0
    g2: LineSegment StartX=12.0711 StartY=72.9289 StartZ=0 EndX=14.8601 EndY=78.3333 EndZ=0
    g3: LineSegment StartX=12.0711 StartY=72.9289 StartZ=0 EndX=6.66667 EndY=70.1399 EndZ=0
    g4: ArcOfCircle CenterX=13.2174 CenterY=68.9542 CenterZ=0 NormalX=0 NormalY=0 NormalZ=1 AngleXU=0 Radius=2 StartAngle=0.348363 EndAngle=0.785398
    g5: GeomPoint X=14.9457 Y=70.0543 Z=0
    g6: LineSegment StartX=10.7634 StartY=74.2366 StartZ=0 EndX=22.9672 EndY=47.9672 EndZ=0
    g7: LineSegment StartX=21.5 StartY=46.5 StartZ=0 EndX=23.5 EndY=48.5 EndZ=0
    g8: LineSegment StartX=6.66667 StartY=70.1399 StartZ=0 EndX=14.8601 EndY=78.3333 EndZ=0
    g9: LineSegment StartX=22.7885 StartY=37.2115 StartZ=0 EndX=9.10088 EndY=12.4259 EndZ=0
    g10: LineSegment StartX=6.66667 StartY=14.8601 StartZ=0 EndX=14.8601 EndY=6.66667 EndZ=0
    g11: LineSegment StartX=22.7885 StartY=37.2115 StartZ=0 EndX=22.9672 EndY=47.9672 EndZ=0
    g12: LineSegment StartX=21.5 StartY=38.5 StartZ=0 EndX=23.5 EndY=36.5 EndZ=0
  constraints (32):
    c: Perpendicular(g-4,g1)
    c: Coincident(g2,g-3)
    c: Coincident(g3,g-3)
    c: Equal(g3,g2)
    c: PointOnObject(g5,g0)
    c: PointOnObject(g5,g1)
    c: Tangent(g0,g4) = -1.5708
    c: Tangent(g1,g4) = 1.5708
    c: Radius(g4) = 2
    c: PointOnObject(g4,g6)
    c: Coincident(g6,g1)
    c: Coincident(g8,g3)
    c: Coincident(g8,g2)
    c: Coincident(g6,g0)
    c: PointOnObject(g0,g8)
    c: Coincident(g2,g3)
    c: PointOnObject(g2,g0)
    c: PointOnObject(g2,g-3)
    c: Perpendicular(g0,g-3,g2) = 4.71239
    c: PointOnObject(g1,g7)
    c: Coincident(g7,g-4)
    c: Coincident(g7,g-4)
    c: Coincident(g10,g-5)
    c: Coincident(g10,g-5)
    c: PointOnObject(g9,g10)
    c: Perpendicular(g-5,g9)
    c: Coincident(g11,g9)
    c: Coincident(g11,g1)
    c: Perpendicular(g-6,g9)
    c: Coincident(g12,g-6)
    c: Coincident(g12,g-6)
    c: PointOnObject(g9,g12)
FEATURE [Sketcher::SketchObject] Sketch055  label="Stabilisierung - Profil002"
  FullyConstrained = true
  MapMode = 7
  Placement = pos=(78.9909,68.3317,-7) rot=(0.879973,0.335893,0.335893;1.69831rad)
  Support = -> [Sketch021]
  sketch-geometry (7):
    g0: LineSegment StartX=-1 StartY=0 StartZ=0 EndX=1 EndY=0 EndZ=0
    g1: ArcOfCircle CenterX=0 CenterY=0.522986 CenterZ=0 NormalX=0 NormalY=0 NormalZ=1 AngleXU=0 Radius=0.477014 StartAngle=0.261799 EndAngle=2.87979
    g2: ArcOfCircle CenterX=1 CenterY=0.477014 CenterZ=0 NormalX=0 NormalY=0 NormalZ=1 AngleXU=0 Radius=0.477014 StartAngle=3.40339 EndAngle=4.71239
    g3: LineSegment StartX=0.53924 StartY=0.353553 StartZ=0 EndX=0.46076 EndY=0.646447 EndZ=0
    g4: LineSegment StartX=-0.53924 StartY=0.353553 StartZ=0 EndX=-0.46076 EndY=0.646447 EndZ=0
    g5: ArcOfCircle CenterX=-1 CenterY=0.477014 CenterZ=0 NormalX=0 NormalY=0 NormalZ=1 AngleXU=0 Radius=0.477014 StartAngle=4.71239 EndAngle=6.02139
    g6: GeomPoint X=0 Y=1 Z=0
  constraints (16):
    c: PointOnObject(g0,g-1)
    c: Symmetric(g0,g0,g-1)
    c: PointOnObject(g1,g-2)
    c: Tangent(g3,g1) = -1.5708
    c: Tangent(g3,g2) = 1.5708
    c: Tangent(g2,g0) = -1.5708
    c: Tangent(g4,g5) = -1.5708
    c: Tangent(g1,g4) = 1.5708
    c: Equal(g4,g3)
    c: PointOnObject(g6,g-2)
    c: PointOnObject(g6,g1)
    c: DistanceY(g-1,g6) = 1
    c: DistanceX(g0,g0) = 2
    c: Tangent(g0,g5) = -1.5708
    c: Angle(g-2,g3) = 0.261799
    c: Equal(g1,g5)
FEATURE [PartDesign::AdditivePipe] AdditivePipe001
  AuxilleryCurvelinear = true
  AuxillerySpineTangent = false
  BaseFeature = -> Mirrored
  Binormal = (0,0,0)
  Mode = 1
  Profile = -> Sketch055
  Refine = true
  Spine = -> Sketch021
  SpineTangent = false
  Transformation = 0
  Transition = 0
FEATURE [PartDesign::Body] Body  label="Base"
  Group = -> [ShapeBinder,Sketch010,Sketch011,Pad003,Pocket005,Sketch012,Hole,Sketch013,Pad004,LCS_1,HoleAxis_1,HoleAxis_2,HoleAxis_3,HoleAxis_4,Sketch014,Hole001,Sketch015,Pad005,Sketch016,Sketch017,Pocket007,Hole002,Sketch019,Sketch020,AdditivePipe,DatumLine,DatumPlane,Mirrored,Sketch021,Sketch055,AdditivePipe001]
  Origin = -> Origin
  Tip = -> AdditivePipe001
FEATURE [App::DocumentObjectGroup] Parts
  Group = -> [Tela_OLed_128x64_v15,Body,Part,Part001,Part002,PG7]
